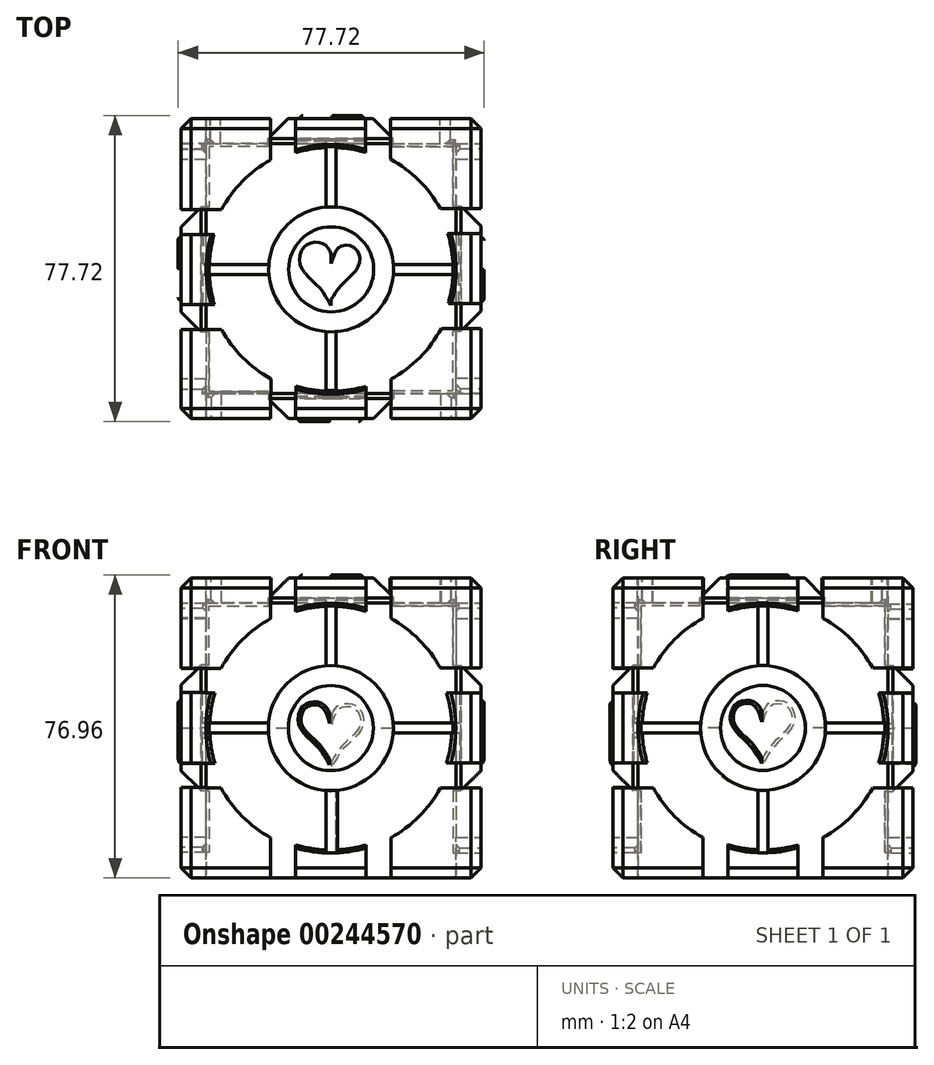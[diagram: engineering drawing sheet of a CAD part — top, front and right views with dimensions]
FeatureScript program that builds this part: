
annotation { "Feature Type Name" : "Feature", "Feature Type Description" : "" }
export const myFeature = defineFeature(function(context is Context, id is Id, definition is map)
    precondition{}
    {
        {
            var Q0;
            Q0=qCreatedBy(makeId("Front.planeOp"),FACE);
            var sketch = newSketch(context, id + "F0", { "sketchPlane" : qUnion([Q0])});
            skLineSegment(sketch, "E0.bottom", {"start": v(38.1, 38.1) * mm, "end": v(-38.1, 38.1) * mm});
            skLineSegment(sketch, "E0.top", {"start": v(38.1, -38.1) * mm, "end": v(-38.1, -38.1) * mm});
            skLineSegment(sketch, "E0.left", {"start": v(38.1, 38.1) * mm, "end": v(38.1, -38.1) * mm});
            skLineSegment(sketch, "E0.right", {"start": v(-38.1, 38.1) * mm, "end": v(-38.1, -38.1) * mm});
            skPoint(sketch, "E0.middle", {"position": v(0, 0) * mm});
            skSolve(sketch);
        }
        {
            var Q0;
            Q0=makeQuery(id+"F0.imprint","IMPRINT",FACE,{"disambiguationData":[TD([[makeQuery(id+"F0.imprint","IMPRINT",EDGE,{"derivedFrom":sQuery(id+"F0.wireOp",EDGE,"E0.bottom")}),1.0]])]});
            extrude(context, id + "F1", {"entities" : qUnion([Q0]), "depth" : 76.2 * mm});
        }
        {
            var Q0;
            Q0=makeQuery(id+"F1.opExtrude","SWEPT_FACE",FACE,{"disambiguationData":[OSD([sQuery(id+"F0.wireOp",EDGE,"E0.left")])]});
            var sketch = newSketch(context, id + "F2", { "sketchPlane" : qUnion([Q0])});
            skLineSegment(sketch, "E1.bottom", {"start": v(-76.2, 38.1) * mm, "end": v(-53.34, 38.1) * mm});
            skLineSegment(sketch, "E1.top", {"start": v(-76.2, 15.24) * mm, "end": v(-65.95, 15.24) * mm});
            skLineSegment(sketch, "E1.left", {"start": v(-76.2, 38.1) * mm, "end": v(-76.2, 15.24) * mm});
            skLineSegment(sketch, "E1.right", {"start": v(-53.34, 38.1) * mm, "end": v(-53.34, 27.85) * mm});
            skLineSegment(sketch, "E2.bottom", {"start": v(-76.2, 8.89) * mm, "end": v(-68.58, 8.89) * mm});
            skLineSegment(sketch, "E2.top", {"start": v(-76.2, -8.9) * mm, "end": v(-68.58, -8.9) * mm});
            skLineSegment(sketch, "E2.left", {"start": v(-76.2, 8.89) * mm, "end": v(-76.2, -8.9) * mm});
            skLineSegment(sketch, "E3.bottom", {"start": v(-76.2, -38.1) * mm, "end": v(-53.34, -38.1) * mm});
            skLineSegment(sketch, "E3.top", {"start": v(-76.2, -15.24) * mm, "end": v(-65.95, -15.24) * mm});
            skLineSegment(sketch, "E3.left", {"start": v(-76.2, -38.1) * mm, "end": v(-76.2, -15.24) * mm});
            skLineSegment(sketch, "E3.right", {"start": v(-53.34, -38.1) * mm, "end": v(-53.34, -27.85) * mm});
            skLineSegment(sketch, "E4.bottom", {"start": v(-47, 38.1) * mm, "end": v(-29.21, 38.1) * mm});
            skLineSegment(sketch, "E4.left", {"start": v(-47, 38.1) * mm, "end": v(-47, 30.48) * mm});
            skLineSegment(sketch, "E4.right", {"start": v(-29.21, 38.1) * mm, "end": v(-29.21, 30.48) * mm});
            skLineSegment(sketch, "E5.bottom", {"start": v(0, 38.1) * mm, "end": v(-22.86, 38.1) * mm});
            skLineSegment(sketch, "E5.top", {"start": v(0, 15.24) * mm, "end": v(-10.25, 15.24) * mm});
            skLineSegment(sketch, "E5.left", {"start": v(0, 38.1) * mm, "end": v(0, 15.24) * mm});
            skLineSegment(sketch, "E5.right", {"start": v(-22.86, 38.1) * mm, "end": v(-22.86, 27.85) * mm});
            skLineSegment(sketch, "E6.bottom", {"start": v(0, -38.1) * mm, "end": v(-22.86, -38.1) * mm});
            skLineSegment(sketch, "E6.top", {"start": v(0, -15.24) * mm, "end": v(-10.25, -15.24) * mm});
            skLineSegment(sketch, "E6.left", {"start": v(0, -38.1) * mm, "end": v(0, -15.24) * mm});
            skLineSegment(sketch, "E6.right", {"start": v(-22.86, -38.1) * mm, "end": v(-22.86, -27.85) * mm});
            skLineSegment(sketch, "E7.top", {"start": v(-47, -38.1) * mm, "end": v(-29.21, -38.1) * mm});
            skLineSegment(sketch, "E7.left", {"start": v(-47, -30.48) * mm, "end": v(-47, -38.1) * mm});
            skLineSegment(sketch, "E7.right", {"start": v(-29.21, -30.48) * mm, "end": v(-29.21, -38.1) * mm});
            skLineSegment(sketch, "E8.bottom", {"start": v(-7.62, 8.89) * mm, "end": v(0, 8.89) * mm});
            skLineSegment(sketch, "E8.top", {"start": v(-7.62, -8.9) * mm, "end": v(0, -8.9) * mm});
            skLineSegment(sketch, "E8.right", {"start": v(0, 8.89) * mm, "end": v(0, -8.9) * mm});
            skArc(sketch, "E9", {"start": v(-53.34, 27.85) * mm, "mid": v(-60.55, 22.45) * mm, "end": v(-65.95, 15.24) * mm});
            skCircle(sketch, "E10", {"center": v(-38.1, 0) * mm, "radius": 15.88 * mm});
            skLineSegment(sketch, "E11", {"start": v(-38.1, 15.88) * mm, "end": v(-38.1, -15.88) * mm, "construction": true});
            skArc(sketch, "E12.trimOffspring", {"start": v(-29.2, 30.48) * mm, "mid": v(-38.1, 31.75) * mm, "end": v(-47, 30.48) * mm});
            skArc(sketch, "E13.trimOffspring", {"start": v(-10.25, 15.24) * mm, "mid": v(-15.65, 22.45) * mm, "end": v(-22.86, 27.85) * mm});
            skArc(sketch, "E14.trimOffspring", {"start": v(-68.58, 8.89) * mm, "mid": v(-69.85, 0) * mm, "end": v(-68.58, -8.89) * mm});
            skArc(sketch, "E15.trimOffspring", {"start": v(-65.95, -15.24) * mm, "mid": v(-60.55, -22.45) * mm, "end": v(-53.34, -27.85) * mm});
            skArc(sketch, "E16.trimOffspring", {"start": v(-7.62, -8.9) * mm, "mid": v(-6.35, 0) * mm, "end": v(-7.62, 8.89) * mm});
            skArc(sketch, "E17.trimOffspring", {"start": v(-22.86, -27.85) * mm, "mid": v(-15.65, -22.45) * mm, "end": v(-10.25, -15.24) * mm});
            skArc(sketch, "E18.trimOffspring", {"start": v(-47, -30.48) * mm, "mid": v(-38.1, -31.75) * mm, "end": v(-29.21, -30.48) * mm});
            skSolve(sketch);
        }
        {
            var Q0;
            {var subQ20=sQuery(id+"F2.wireOp",EDGE,"E1.top");Q0=makeQuery(id+"F2.imprint","IMPRINT",FACE,{"disambiguationData":[TD([[makeQuery(id+"F2.imprint","IMPRINT",EDGE,{"derivedFrom":subQ20}),-1.0]])]});}
            extrude(context, id + "F3", {"entities" : qUnion([Q0]), "operationType" : NewBodyOperationType.REMOVE, "oppositeDirection" : true, "depth" : 6.35 * mm});
        }
        {
            var Q0;
            Q0=makeQuery(id+"F1.opExtrude","CAP_FACE",FACE,{"disambiguationData":[OSD([sQuery(id+"F0.wireOp",EDGE,"E0.bottom"),sQuery(id+"F0.wireOp",EDGE,"E0.top"),sQuery(id+"F0.wireOp",EDGE,"E0.left"),sQuery(id+"F0.wireOp",EDGE,"E0.right")])],"isStart":true});
            var sketch = newSketch(context, id + "F4", { "sketchPlane" : qUnion([Q0])});
            skLineSegment(sketch, "E19.bottom", {"start": v(-37.9, 38.1) * mm, "end": v(-15.05, 38.1) * mm});
            skLineSegment(sketch, "E19.left", {"start": v(-37.9, 38.1) * mm, "end": v(-37.9, 37.9) * mm});
            skLineSegment(sketch, "E19.right", {"start": v(-15.05, 38.1) * mm, "end": v(-15.05, 27.85) * mm});
            skLineSegment(sketch, "E20.left", {"start": v(-37.9, 8.89) * mm, "end": v(-37.9, 8.7) * mm});
            skLineSegment(sketch, "E21.bottom", {"start": v(-37.9, -38.1) * mm, "end": v(-15.05, -38.1) * mm});
            skLineSegment(sketch, "E21.left", {"start": v(-37.9, -15.43) * mm, "end": v(-37.9, -15.24) * mm});
            skLineSegment(sketch, "E21.right", {"start": v(-15.05, -38.1) * mm, "end": v(-15.05, -27.85) * mm});
            skLineSegment(sketch, "E22.bottom", {"start": v(-8.7, 38.1) * mm, "end": v(9.08, 38.1) * mm});
            skLineSegment(sketch, "E22.left", {"start": v(-8.7, 38.1) * mm, "end": v(-8.7, 30.48) * mm});
            skLineSegment(sketch, "E22.right", {"start": v(9.08, 38.1) * mm, "end": v(9.08, 30.48) * mm});
            skLineSegment(sketch, "E23.bottom", {"start": v(38.3, 38.1) * mm, "end": v(15.43, 38.1) * mm});
            skLineSegment(sketch, "E23.top", {"start": v(38.3, 15.24) * mm, "end": v(28.04, 15.24) * mm});
            skLineSegment(sketch, "E23.left", {"start": v(38.3, 38.1) * mm, "end": v(38.3, 15.24) * mm});
            skLineSegment(sketch, "E23.right", {"start": v(15.43, 38.1) * mm, "end": v(15.43, 27.85) * mm});
            skLineSegment(sketch, "E24.bottom", {"start": v(38.3, -38.1) * mm, "end": v(15.43, -38.1) * mm});
            skLineSegment(sketch, "E24.top", {"start": v(38.3, -15.24) * mm, "end": v(28.04, -15.24) * mm});
            skLineSegment(sketch, "E24.left", {"start": v(38.3, -38.1) * mm, "end": v(38.3, -15.24) * mm});
            skLineSegment(sketch, "E24.right", {"start": v(15.43, -38.1) * mm, "end": v(15.43, -27.85) * mm});
            skLineSegment(sketch, "E25.top", {"start": v(-8.7, -38.1) * mm, "end": v(9.08, -38.1) * mm});
            skLineSegment(sketch, "E25.left", {"start": v(-8.7, -30.48) * mm, "end": v(-8.7, -38.1) * mm});
            skLineSegment(sketch, "E25.right", {"start": v(9.08, -30.48) * mm, "end": v(9.08, -38.1) * mm});
            skLineSegment(sketch, "E26.bottom", {"start": v(30.67, 8.9) * mm, "end": v(38.3, 8.9) * mm});
            skLineSegment(sketch, "E26.top", {"start": v(30.67, -8.89) * mm, "end": v(38.3, -8.89) * mm});
            skLineSegment(sketch, "E26.right", {"start": v(38.3, 8.9) * mm, "end": v(38.3, -8.89) * mm});
            skArc(sketch, "E27", {"start": v(-15.05, 27.85) * mm, "mid": v(-22.26, 22.45) * mm, "end": v(-27.66, 15.24) * mm});
            skCircle(sketch, "E28", {"center": v(0.2, 0) * mm, "radius": 15.88 * mm});
            skLineSegment(sketch, "E29", {"start": v(0.2, 15.88) * mm, "end": v(0.2, -15.87) * mm, "construction": true});
            skArc(sketch, "E30.trimOffspring", {"start": v(9.08, 30.48) * mm, "mid": v(0.2, 31.75) * mm, "end": v(-8.7, 30.48) * mm});
            skArc(sketch, "E31.trimOffspring", {"start": v(28.04, 15.24) * mm, "mid": v(22.64, 22.45) * mm, "end": v(15.43, 27.85) * mm});
            skArc(sketch, "E32.trimOffspring", {"start": v(-30.29, 8.9) * mm, "mid": v(-31.56, 0) * mm, "end": v(-30.29, -8.89) * mm});
            skArc(sketch, "E33.trimOffspring", {"start": v(-27.66, -15.24) * mm, "mid": v(-22.26, -22.45) * mm, "end": v(-15.05, -27.85) * mm});
            skArc(sketch, "E34.trimOffspring", {"start": v(30.67, -8.89) * mm, "mid": v(31.94, 0) * mm, "end": v(30.67, 8.9) * mm});
            skArc(sketch, "E35.trimOffspring", {"start": v(15.43, -27.85) * mm, "mid": v(22.64, -22.45) * mm, "end": v(28.04, -15.24) * mm});
            skArc(sketch, "E36.trimOffspring", {"start": v(-8.7, -30.48) * mm, "mid": v(0.2, -31.75) * mm, "end": v(9.08, -30.48) * mm});
            skLineSegment(sketch, "E37.bottom", {"start": v(-37.9, 37.9) * mm, "end": v(-15.05, 37.9) * mm});
            skLineSegment(sketch, "E37.left", {"start": v(-37.9, 15.24) * mm, "end": v(-37.9, 15.05) * mm});
            skLineSegment(sketch, "E37.right", {"start": v(-15.05, 37.9) * mm, "end": v(-15.05, 27.66) * mm});
            skLineSegment(sketch, "E38.bottom", {"start": v(-30.34, 8.7) * mm, "end": v(-30.29, 8.7) * mm});
            skLineSegment(sketch, "E38.left", {"start": v(-37.9, -8.9) * mm, "end": v(-37.9, -9.08) * mm});
            skLineSegment(sketch, "E39.bottom", {"start": v(-37.9, -38.3) * mm, "end": v(-15.05, -38.3) * mm});
            skLineSegment(sketch, "E39.left", {"start": v(-37.9, -38.3) * mm, "end": v(-37.9, -38.1) * mm});
            skLineSegment(sketch, "E39.right", {"start": v(-15.05, -38.3) * mm, "end": v(-15.05, -28.04) * mm});
            skLineSegment(sketch, "E40.bottom", {"start": v(-8.7, 37.9) * mm, "end": v(9.08, 37.9) * mm});
            skLineSegment(sketch, "E40.left", {"start": v(-8.7, 37.9) * mm, "end": v(-8.7, 30.29) * mm});
            skLineSegment(sketch, "E40.right", {"start": v(9.08, 37.9) * mm, "end": v(9.08, 30.29) * mm});
            skLineSegment(sketch, "E41.bottom", {"start": v(38.3, 37.9) * mm, "end": v(15.43, 37.9) * mm});
            skLineSegment(sketch, "E41.top", {"start": v(38.3, 15.05) * mm, "end": v(28.04, 15.05) * mm});
            skLineSegment(sketch, "E41.left", {"start": v(38.3, 37.9) * mm, "end": v(38.3, 15.05) * mm});
            skLineSegment(sketch, "E41.right", {"start": v(15.43, 37.9) * mm, "end": v(15.43, 27.66) * mm});
            skLineSegment(sketch, "E42.bottom", {"start": v(38.3, -38.3) * mm, "end": v(15.43, -38.3) * mm});
            skLineSegment(sketch, "E42.top", {"start": v(38.3, -15.43) * mm, "end": v(28.04, -15.43) * mm});
            skLineSegment(sketch, "E42.left", {"start": v(38.3, -38.3) * mm, "end": v(38.3, -15.43) * mm});
            skLineSegment(sketch, "E42.right", {"start": v(15.43, -38.3) * mm, "end": v(15.43, -28.04) * mm});
            skLineSegment(sketch, "E43.top", {"start": v(-8.7, -38.3) * mm, "end": v(9.08, -38.3) * mm});
            skLineSegment(sketch, "E43.left", {"start": v(-8.7, -30.67) * mm, "end": v(-8.7, -38.3) * mm});
            skLineSegment(sketch, "E43.right", {"start": v(9.08, -30.67) * mm, "end": v(9.08, -38.3) * mm});
            skLineSegment(sketch, "E44.bottom", {"start": v(30.67, 8.7) * mm, "end": v(38.3, 8.7) * mm});
            skLineSegment(sketch, "E44.top", {"start": v(30.67, -9.08) * mm, "end": v(38.3, -9.08) * mm});
            skLineSegment(sketch, "E44.right", {"start": v(38.3, 8.7) * mm, "end": v(38.3, -9.08) * mm});
            skArc(sketch, "E45", {"start": v(-15.05, 27.66) * mm, "mid": v(-22.26, 22.26) * mm, "end": v(-27.66, 15.05) * mm});
            skCircle(sketch, "E46", {"center": v(0.2, -0.2) * mm, "radius": 15.88 * mm});
            skLineSegment(sketch, "E47", {"start": v(0.2, 15.68) * mm, "end": v(0.2, -16.07) * mm, "construction": true});
            skArc(sketch, "E48.trimOffspring", {"start": v(9.08, 30.29) * mm, "mid": v(0.2, 31.56) * mm, "end": v(-8.7, 30.29) * mm});
            skArc(sketch, "E49.trimOffspring", {"start": v(28.04, 15.05) * mm, "mid": v(22.64, 22.26) * mm, "end": v(15.43, 27.66) * mm});
            skArc(sketch, "E50.trimOffspring", {"start": v(-30.29, 8.7) * mm, "mid": v(-31.56, -0.2) * mm, "end": v(-30.29, -9.08) * mm});
            skArc(sketch, "E51.trimOffspring", {"start": v(-27.66, -15.43) * mm, "mid": v(-22.26, -22.64) * mm, "end": v(-15.05, -28.04) * mm});
            skArc(sketch, "E52.trimOffspring", {"start": v(30.67, -9.08) * mm, "mid": v(31.94, -0.2) * mm, "end": v(30.67, 8.7) * mm});
            skArc(sketch, "E53.trimOffspring", {"start": v(15.43, -28.04) * mm, "mid": v(22.64, -22.64) * mm, "end": v(28.04, -15.43) * mm});
            skArc(sketch, "E54.trimOffspring", {"start": v(-8.7, -30.67) * mm, "mid": v(0.2, -31.94) * mm, "end": v(9.08, -30.67) * mm});
            skPoint(sketch, "E19.top.start.orphan", {"position": v(-37.9, 15.24) * mm});
            skPoint(sketch, "E55.orphan", {"position": v(-37.9, -8.9) * mm});
            skLineSegment(sketch, "E56", {"start": v(-31.75, 8.9) * mm, "end": v(-30.29, 8.9) * mm});
            skLineSegment(sketch, "E57", {"start": v(-31.75, 15.24) * mm, "end": v(-27.66, 15.24) * mm});
            skLineSegment(sketch, "E58", {"start": v(-31.75, 8.9) * mm, "end": v(-31.75, 15.24) * mm});
            skLineSegment(sketch, "E59", {"start": v(-30.29, -8.89) * mm, "end": v(-31.75, -8.89) * mm});
            skLineSegment(sketch, "E60", {"start": v(-31.75, -8.89) * mm, "end": v(-31.75, -15.24) * mm});
            skLineSegment(sketch, "E61", {"start": v(-31.75, -15.24) * mm, "end": v(-27.66, -15.24) * mm});
            skSolve(sketch);
        }
        {
            var Q0;
            {var subQ58=sQuery(id+"F4.wireOp",EDGE,"E19.right");Q0=makeQuery(id+"F4.imprint","IMPRINT",FACE,{"disambiguationData":[TD([[makeQuery(id+"F4.imprint","IMPRINT",EDGE,{"derivedFrom":subQ58}),1.0]])]});}
            extrude(context, id + "F5", {"entities" : qUnion([Q0]), "operationType" : NewBodyOperationType.REMOVE, "oppositeDirection" : true, "depth" : 6.35 * mm});
        }
        {
            var Q0;
            Q0=makeQuery(id+"F1.opExtrude","SWEPT_FACE",FACE,{"disambiguationData":[OSD([sQuery(id+"F0.wireOp",EDGE,"E0.right")])]});
            var sketch = newSketch(context, id + "F6", { "sketchPlane" : qUnion([Q0])});
            skLineSegment(sketch, "E62", {"start": v(0, 0) * mm, "end": v(38.1, 0) * mm, "construction": true});
            skPoint(sketch, "E62.endSnap0", {"position": v(38.1, 38.1) * mm});
            skLineSegment(sketch, "E63.bottom", {"start": v(0.2, 38.18) * mm, "end": v(23.07, 38.18) * mm});
            skLineSegment(sketch, "E63.left", {"start": v(0.2, 38.18) * mm, "end": v(0.2, 37.99) * mm});
            skLineSegment(sketch, "E63.right", {"start": v(23.07, 38.18) * mm, "end": v(23.07, 27.93) * mm});
            skLineSegment(sketch, "E64.left", {"start": v(0.2, 8.97) * mm, "end": v(0.2, 8.78) * mm});
            skLineSegment(sketch, "E65.bottom", {"start": v(0.2, -38.02) * mm, "end": v(23.07, -38.02) * mm});
            skLineSegment(sketch, "E65.left", {"start": v(0.2, -15.35) * mm, "end": v(0.2, -15.16) * mm});
            skLineSegment(sketch, "E65.right", {"start": v(23.07, -38.02) * mm, "end": v(23.07, -27.77) * mm});
            skLineSegment(sketch, "E66.bottom", {"start": v(29.42, 38.18) * mm, "end": v(47.2, 38.18) * mm});
            skLineSegment(sketch, "E66.left", {"start": v(29.42, 38.18) * mm, "end": v(29.42, 30.56) * mm});
            skLineSegment(sketch, "E66.right", {"start": v(47.2, 38.18) * mm, "end": v(47.2, 30.56) * mm});
            skLineSegment(sketch, "E67.bottom", {"start": v(76.4, 38.18) * mm, "end": v(53.55, 38.18) * mm});
            skLineSegment(sketch, "E67.top", {"start": v(76.4, 15.32) * mm, "end": v(66.16, 15.32) * mm});
            skLineSegment(sketch, "E67.left", {"start": v(76.4, 38.18) * mm, "end": v(76.4, 15.32) * mm});
            skLineSegment(sketch, "E67.right", {"start": v(53.55, 38.18) * mm, "end": v(53.55, 27.93) * mm});
            skLineSegment(sketch, "E68.bottom", {"start": v(76.4, -38.02) * mm, "end": v(53.55, -38.02) * mm});
            skLineSegment(sketch, "E68.top", {"start": v(76.4, -15.16) * mm, "end": v(66.16, -15.16) * mm});
            skLineSegment(sketch, "E68.left", {"start": v(76.4, -38.02) * mm, "end": v(76.4, -15.16) * mm});
            skLineSegment(sketch, "E68.right", {"start": v(53.55, -38.02) * mm, "end": v(53.55, -27.77) * mm});
            skLineSegment(sketch, "E69.top", {"start": v(29.42, -38.02) * mm, "end": v(47.2, -38.02) * mm});
            skLineSegment(sketch, "E69.left", {"start": v(29.42, -30.4) * mm, "end": v(29.42, -38.02) * mm});
            skLineSegment(sketch, "E69.right", {"start": v(47.2, -30.4) * mm, "end": v(47.2, -38.02) * mm});
            skLineSegment(sketch, "E70.bottom", {"start": v(68.79, 8.97) * mm, "end": v(76.4, 8.97) * mm});
            skLineSegment(sketch, "E70.top", {"start": v(68.79, -8.81) * mm, "end": v(76.4, -8.81) * mm});
            skLineSegment(sketch, "E70.right", {"start": v(76.4, 8.97) * mm, "end": v(76.4, -8.81) * mm});
            skArc(sketch, "E71", {"start": v(23.07, 27.93) * mm, "mid": v(15.86, 22.53) * mm, "end": v(10.45, 15.32) * mm});
            skCircle(sketch, "E72", {"center": v(38.3, 0.08) * mm, "radius": 15.88 * mm});
            skLineSegment(sketch, "E73", {"start": v(38.3, 15.95) * mm, "end": v(38.3, -15.8) * mm, "construction": true});
            skArc(sketch, "E74.trimOffspring", {"start": v(47.2, 30.56) * mm, "mid": v(38.3, 31.83) * mm, "end": v(29.42, 30.56) * mm});
            skArc(sketch, "E75.trimOffspring", {"start": v(66.16, 15.32) * mm, "mid": v(60.76, 22.53) * mm, "end": v(53.55, 27.93) * mm});
            skArc(sketch, "E76.trimOffspring", {"start": v(7.83, 8.97) * mm, "mid": v(6.56, 0.08) * mm, "end": v(7.83, -8.81) * mm});
            skArc(sketch, "E77.trimOffspring", {"start": v(10.45, -15.16) * mm, "mid": v(15.86, -22.37) * mm, "end": v(23.07, -27.77) * mm});
            skArc(sketch, "E78.trimOffspring", {"start": v(68.79, -8.81) * mm, "mid": v(70.06, 0.08) * mm, "end": v(68.79, 8.97) * mm});
            skArc(sketch, "E79.trimOffspring", {"start": v(53.55, -27.77) * mm, "mid": v(60.76, -22.37) * mm, "end": v(66.16, -15.16) * mm});
            skArc(sketch, "E80.trimOffspring", {"start": v(29.42, -30.4) * mm, "mid": v(38.3, -31.67) * mm, "end": v(47.2, -30.4) * mm});
            skLineSegment(sketch, "E81.bottom", {"start": v(0.2, 37.99) * mm, "end": v(23.07, 37.99) * mm});
            skLineSegment(sketch, "E81.left", {"start": v(0.2, 15.32) * mm, "end": v(0.2, 15.13) * mm});
            skLineSegment(sketch, "E81.right", {"start": v(23.07, 37.99) * mm, "end": v(23.07, 27.74) * mm});
            skLineSegment(sketch, "E82.bottom", {"start": v(7.77, 8.78) * mm, "end": v(7.83, 8.78) * mm});
            skLineSegment(sketch, "E82.left", {"start": v(0.2, -8.81) * mm, "end": v(0.2, -9) * mm});
            skLineSegment(sketch, "E83.bottom", {"start": v(0.2, -38.21) * mm, "end": v(23.07, -38.21) * mm});
            skLineSegment(sketch, "E83.left", {"start": v(0.2, -38.21) * mm, "end": v(0.2, -38.02) * mm});
            skLineSegment(sketch, "E83.right", {"start": v(23.07, -38.21) * mm, "end": v(23.07, -27.96) * mm});
            skLineSegment(sketch, "E84.bottom", {"start": v(29.42, 37.99) * mm, "end": v(47.2, 37.99) * mm});
            skLineSegment(sketch, "E84.left", {"start": v(29.42, 37.99) * mm, "end": v(29.42, 30.37) * mm});
            skLineSegment(sketch, "E84.right", {"start": v(47.2, 37.99) * mm, "end": v(47.2, 30.37) * mm});
            skLineSegment(sketch, "E85.bottom", {"start": v(76.4, 37.99) * mm, "end": v(53.55, 37.99) * mm});
            skLineSegment(sketch, "E85.top", {"start": v(76.4, 15.13) * mm, "end": v(66.16, 15.13) * mm});
            skLineSegment(sketch, "E85.left", {"start": v(76.4, 37.99) * mm, "end": v(76.4, 15.13) * mm});
            skLineSegment(sketch, "E85.right", {"start": v(53.55, 37.99) * mm, "end": v(53.55, 27.74) * mm});
            skLineSegment(sketch, "E86.bottom", {"start": v(76.4, -38.21) * mm, "end": v(53.55, -38.21) * mm});
            skLineSegment(sketch, "E86.top", {"start": v(76.4, -15.35) * mm, "end": v(66.16, -15.35) * mm});
            skLineSegment(sketch, "E86.left", {"start": v(76.4, -38.21) * mm, "end": v(76.4, -15.35) * mm});
            skLineSegment(sketch, "E86.right", {"start": v(53.55, -38.21) * mm, "end": v(53.55, -27.96) * mm});
            skLineSegment(sketch, "E87.top", {"start": v(29.42, -38.21) * mm, "end": v(47.2, -38.21) * mm});
            skLineSegment(sketch, "E87.left", {"start": v(29.42, -30.6) * mm, "end": v(29.42, -38.21) * mm});
            skLineSegment(sketch, "E87.right", {"start": v(47.2, -30.6) * mm, "end": v(47.2, -38.21) * mm});
            skLineSegment(sketch, "E88.bottom", {"start": v(68.79, 8.78) * mm, "end": v(76.4, 8.78) * mm});
            skLineSegment(sketch, "E88.top", {"start": v(68.79, -9) * mm, "end": v(76.4, -9) * mm});
            skLineSegment(sketch, "E88.right", {"start": v(76.4, 8.78) * mm, "end": v(76.4, -9) * mm});
            skArc(sketch, "E89", {"start": v(23.07, 27.74) * mm, "mid": v(15.86, 22.34) * mm, "end": v(10.45, 15.13) * mm});
            skCircle(sketch, "E90", {"center": v(38.3, -0.11) * mm, "radius": 15.88 * mm});
            skLineSegment(sketch, "E91", {"start": v(38.3, 15.76) * mm, "end": v(38.3, -15.99) * mm, "construction": true});
            skArc(sketch, "E92.trimOffspring", {"start": v(47.2, 30.37) * mm, "mid": v(38.3, 31.64) * mm, "end": v(29.42, 30.37) * mm});
            skArc(sketch, "E93.trimOffspring", {"start": v(66.16, 15.13) * mm, "mid": v(60.76, 22.34) * mm, "end": v(53.55, 27.74) * mm});
            skArc(sketch, "E94.trimOffspring", {"start": v(7.83, 8.78) * mm, "mid": v(6.56, -0.11) * mm, "end": v(7.83, -9) * mm});
            skArc(sketch, "E95.trimOffspring", {"start": v(10.45, -15.35) * mm, "mid": v(15.86, -22.56) * mm, "end": v(23.07, -27.96) * mm});
            skArc(sketch, "E96.trimOffspring", {"start": v(68.79, -9) * mm, "mid": v(70.06, -0.11) * mm, "end": v(68.79, 8.78) * mm});
            skArc(sketch, "E97.trimOffspring", {"start": v(53.55, -27.96) * mm, "mid": v(60.76, -22.56) * mm, "end": v(66.16, -15.35) * mm});
            skArc(sketch, "E98.trimOffspring", {"start": v(29.42, -30.6) * mm, "mid": v(38.3, -31.86) * mm, "end": v(47.2, -30.6) * mm});
            skPoint(sketch, "E63.top.start.orphan", {"position": v(0.2, 15.32) * mm});
            skPoint(sketch, "E99.orphan", {"position": v(0.2, -8.81) * mm});
            skLineSegment(sketch, "E100", {"start": v(6.37, 8.97) * mm, "end": v(7.83, 8.97) * mm});
            skLineSegment(sketch, "E101", {"start": v(6.37, 15.32) * mm, "end": v(10.45, 15.32) * mm});
            skLineSegment(sketch, "E102", {"start": v(6.37, 8.97) * mm, "end": v(6.37, 15.32) * mm});
            skLineSegment(sketch, "E103", {"start": v(7.83, -8.81) * mm, "end": v(6.37, -8.81) * mm});
            skLineSegment(sketch, "E104", {"start": v(6.37, -8.81) * mm, "end": v(6.37, -15.16) * mm});
            skLineSegment(sketch, "E105", {"start": v(6.37, -15.16) * mm, "end": v(10.45, -15.16) * mm});
            skSolve(sketch);
        }
        {
            var Q0;
            {var subQ55=sQuery(id+"F6.wireOp",EDGE,"E65.right");Q0=makeQuery(id+"F6.imprint","IMPRINT",FACE,{"disambiguationData":[TD([[makeQuery(id+"F6.imprint","IMPRINT",EDGE,{"derivedFrom":subQ55}),-1.0]])]});}
            extrude(context, id + "F7", {"entities" : qUnion([Q0]), "operationType" : NewBodyOperationType.REMOVE, "oppositeDirection" : true, "depth" : 6.35 * mm});
        }
        {
            var Q0;
            Q0=makeQuery(id+"F1.opExtrude","CAP_FACE",FACE,{"disambiguationData":[OSD([sQuery(id+"F0.wireOp",EDGE,"E0.bottom"),sQuery(id+"F0.wireOp",EDGE,"E0.top"),sQuery(id+"F0.wireOp",EDGE,"E0.left"),sQuery(id+"F0.wireOp",EDGE,"E0.right")])],"isStart":false});
            var sketch = newSketch(context, id + "F8", { "sketchPlane" : qUnion([Q0])});
            skArc(sketch, "E106", {"start": v(-15.33, 27.8) * mm, "mid": v(-22.59, 22.36) * mm, "end": v(-28, 15.08) * mm});
            skCircle(sketch, "E107", {"center": v(-0.1, -0.05) * mm, "radius": 15.87 * mm});
            skLineSegment(sketch, "E108", {"start": v(-38.2, 38.05) * mm, "end": v(-15.33, 38.05) * mm});
            skLineSegment(sketch, "E109", {"start": v(38, 38.05) * mm, "end": v(15.15, 38.05) * mm});
            skLineSegment(sketch, "E110", {"start": v(-15.33, 38.05) * mm, "end": v(-15.33, 27.8) * mm});
            skLineSegment(sketch, "E111", {"start": v(15.15, 38.05) * mm, "end": v(15.15, 27.8) * mm});
            skLineSegment(sketch, "E112", {"start": v(-15.33, -27.9) * mm, "end": v(-15.33, -38.15) * mm});
            skLineSegment(sketch, "E113", {"start": v(-15.33, -38.15) * mm, "end": v(-38.2, -38.15) * mm});
            skLineSegment(sketch, "E114", {"start": v(15.15, -27.9) * mm, "end": v(15.15, -38.15) * mm});
            skLineSegment(sketch, "E115", {"start": v(15.15, -38.15) * mm, "end": v(38, -38.15) * mm});
            skLineSegment(sketch, "E116", {"start": v(-15.33, -38.15) * mm, "end": v(-8.98, -38.15) * mm});
            skLineSegment(sketch, "E117", {"start": v(-8.98, -38.15) * mm, "end": v(-8.98, -30.53) * mm});
            skLineSegment(sketch, "E118", {"start": v(-15.33, 38.05) * mm, "end": v(-8.98, 38.05) * mm});
            skLineSegment(sketch, "E119", {"start": v(-8.98, 38.05) * mm, "end": v(-8.98, 30.43) * mm});
            skLineSegment(sketch, "E120", {"start": v(15.15, 38.05) * mm, "end": v(8.8, 38.05) * mm});
            skLineSegment(sketch, "E121", {"start": v(8.8, 38.05) * mm, "end": v(8.8, 30.43) * mm});
            skLineSegment(sketch, "E122", {"start": v(15.15, -38.15) * mm, "end": v(8.8, -38.15) * mm});
            skLineSegment(sketch, "E123", {"start": v(8.8, -38.15) * mm, "end": v(8.8, -30.53) * mm});
            skLineSegment(sketch, "E124", {"start": v(-31.84, 15.08) * mm, "end": v(-28, 15.08) * mm});
            skLineSegment(sketch, "E125", {"start": v(-31.84, 8.92) * mm, "end": v(-31.84, 15.08) * mm});
            skLineSegment(sketch, "E126", {"start": v(-31.84, 8.92) * mm, "end": v(-30.55, 8.92) * mm});
            skLineSegment(sketch, "E127", {"start": v(-28, -15.2) * mm, "end": v(-31.84, -15.2) * mm});
            skLineSegment(sketch, "E128", {"start": v(-31.84, -15.2) * mm, "end": v(-31.84, -9.05) * mm});
            skLineSegment(sketch, "E129", {"start": v(-31.84, -9.05) * mm, "end": v(-30.54, -9.05) * mm});
            skLineSegment(sketch, "E130", {"start": v(27.76, 15.2) * mm, "end": v(31.66, 15.2) * mm});
            skLineSegment(sketch, "E131", {"start": v(31.66, 15.2) * mm, "end": v(31.66, 8.84) * mm});
            skLineSegment(sketch, "E132", {"start": v(31.66, 8.84) * mm, "end": v(30.39, 8.84) * mm});
            skLineSegment(sketch, "E133", {"start": v(27.76, -15.29) * mm, "end": v(31.66, -15.29) * mm});
            skLineSegment(sketch, "E134", {"start": v(31.66, -15.29) * mm, "end": v(31.66, -8.94) * mm});
            skLineSegment(sketch, "E135", {"start": v(31.66, -8.94) * mm, "end": v(30.39, -8.94) * mm});
            skArc(sketch, "E136.trimOffspring", {"start": v(8.8, 30.43) * mm, "mid": v(-0.1, 31.7) * mm, "end": v(-8.98, 30.43) * mm});
            skArc(sketch, "E137.trimOffspring", {"start": v(-30.55, 8.92) * mm, "mid": v(-31.84, -0.06) * mm, "end": v(-30.54, -9.05) * mm});
            skArc(sketch, "E138.trimOffspring", {"start": v(-28, -15.2) * mm, "mid": v(-22.58, -22.46) * mm, "end": v(-15.33, -27.9) * mm});
            skArc(sketch, "E139.trimOffspring", {"start": v(27.76, 15.2) * mm, "mid": v(22.36, 22.4) * mm, "end": v(15.15, 27.8) * mm});
            skArc(sketch, "E140.trimOffspring", {"start": v(-8.98, -30.53) * mm, "mid": v(-0.1, -31.8) * mm, "end": v(8.8, -30.53) * mm});
            skArc(sketch, "E141.trimOffspring", {"start": v(15.15, -27.9) * mm, "mid": v(22.36, -22.5) * mm, "end": v(27.76, -15.29) * mm});
            skArc(sketch, "E142.trimOffspring", {"start": v(30.39, -8.94) * mm, "mid": v(31.66, -0.05) * mm, "end": v(30.39, 8.84) * mm});
            skSolve(sketch);
        }
        {
            var Q0;
            {var subQ25=sQuery(id+"F8.wireOp",EDGE,"E106");Q0=makeQuery(id+"F8.imprint","IMPRINT",FACE,{"disambiguationData":[TD([[makeQuery(id+"F8.imprint","IMPRINT",EDGE,{"derivedFrom":subQ25}),1.0]])]});}
            extrude(context, id + "F9", {"entities" : qUnion([Q0]), "operationType" : NewBodyOperationType.REMOVE, "oppositeDirection" : true, "depth" : 6.35 * mm});
        }
        {
            var Q0;
            Q0=makeQuery(id+"F9.boolean.opBoolean","COPY",FACE,{"derivedFrom":makeQuery(id+"F9.opExtrude","SWEPT_FACE",FACE,{"disambiguationData":[OSD([sQuery(id+"F8.wireOp",EDGE,"E131")])]})});
            var sketch = newSketch(context, id + "F10", { "sketchPlane" : qUnion([Q0])});
            skLineSegment(sketch, "E143", {"start": v(69.85, 15.2) * mm, "end": v(76.2, 15.2) * mm});
            skLineSegment(sketch, "E144", {"start": v(76.2, 15.2) * mm, "end": v(76.2, 8.84) * mm});
            skLineSegment(sketch, "E145", {"start": v(76.2, 8.84) * mm, "end": v(69.85, 8.84) * mm});
            skLineSegment(sketch, "E146", {"start": v(69.85, 8.84) * mm, "end": v(69.85, 15.2) * mm});
            skSolve(sketch);
        }
        {
            var Q0;
            Q0=makeQuery(id+"F10.imprint","IMPRINT",FACE,{"disambiguationData":[TD([[makeQuery(id+"F10.imprint","IMPRINT",EDGE,{"derivedFrom":sQuery(id+"F10.wireOp",EDGE,"E143")}),-1.0]])]});
            var Q1;
            Q1 = qSketchRegion(id + "F10", true);
            extrude(context, id + "F11", {"entities" : qUnion([Q0, Q1]), "operationType" : NewBodyOperationType.REMOVE, "oppositeDirection" : true, "depth" : 25.4 * mm});
        }
        {
            var Q0;
            Q0=makeQuery(id+"F9.boolean.opBoolean","COPY",FACE,{"derivedFrom":makeQuery(id+"F9.opExtrude","SWEPT_FACE",FACE,{"disambiguationData":[OSD([sQuery(id+"F8.wireOp",EDGE,"E134")])]})});
            var sketch = newSketch(context, id + "F12", { "sketchPlane" : qUnion([Q0])});
            skLineSegment(sketch, "E147", {"start": v(69.85, -8.94) * mm, "end": v(76.2, -8.94) * mm});
            skLineSegment(sketch, "E148", {"start": v(76.2, -8.94) * mm, "end": v(76.2, -15.29) * mm});
            skLineSegment(sketch, "E149", {"start": v(76.2, -15.29) * mm, "end": v(69.85, -15.29) * mm});
            skLineSegment(sketch, "E150", {"start": v(69.85, -15.29) * mm, "end": v(69.85, -8.94) * mm});
            skSolve(sketch);
        }
        {
            var Q0;
            Q0=makeQuery(id+"F12.imprint","IMPRINT",FACE,{"disambiguationData":[TD([[makeQuery(id+"F12.imprint","IMPRINT",EDGE,{"derivedFrom":sQuery(id+"F12.wireOp",EDGE,"E147")}),-1.0]])]});
            extrude(context, id + "F13", {"entities" : qUnion([Q0]), "operationType" : NewBodyOperationType.REMOVE, "oppositeDirection" : true, "depth" : 25.4 * mm});
        }
        {
            var Q0;
            Q0=makeQuery(id+"F7.boolean.opBoolean","COPY",FACE,{"derivedFrom":makeQuery(id+"F7.opExtrude","SWEPT_FACE",FACE,{"disambiguationData":[OSD([sQuery(id+"F6.wireOp",EDGE,"E102")])]})});
            var sketch = newSketch(context, id + "F14", { "sketchPlane" : qUnion([Q0])});
            skLineSegment(sketch, "E151", {"start": v(-31.75, 15.32) * mm, "end": v(-38.1, 15.32) * mm});
            skLineSegment(sketch, "E152", {"start": v(-38.1, 15.32) * mm, "end": v(-38.1, 8.97) * mm});
            skLineSegment(sketch, "E153", {"start": v(-38.1, 8.97) * mm, "end": v(-31.75, 8.97) * mm});
            skLineSegment(sketch, "E154", {"start": v(-31.75, 8.97) * mm, "end": v(-31.75, 15.32) * mm});
            skSolve(sketch);
        }
        {
            var Q0;
            Q0=makeQuery(id+"F14.imprint","IMPRINT",FACE,{"disambiguationData":[TD([[makeQuery(id+"F14.imprint","IMPRINT",EDGE,{"derivedFrom":sQuery(id+"F14.wireOp",EDGE,"E151")}),1.0]])]});
            extrude(context, id + "F15", {"entities" : qUnion([Q0]), "operationType" : NewBodyOperationType.REMOVE, "oppositeDirection" : true, "depth" : 25.4 * mm});
        }
        {
            var Q0;
            Q0=makeQuery(id+"F7.boolean.opBoolean","COPY",FACE,{"derivedFrom":makeQuery(id+"F7.opExtrude","SWEPT_FACE",FACE,{"disambiguationData":[OSD([sQuery(id+"F6.wireOp",EDGE,"E104")])]})});
            var sketch = newSketch(context, id + "F16", { "sketchPlane" : qUnion([Q0])});
            skLineSegment(sketch, "E155", {"start": v(-38.1, -8.81) * mm, "end": v(-38.1, -15.16) * mm});
            skLineSegment(sketch, "E156", {"start": v(-38.1, -15.16) * mm, "end": v(-31.75, -15.16) * mm});
            skLineSegment(sketch, "E157", {"start": v(-31.75, -15.16) * mm, "end": v(-31.75, -8.81) * mm});
            skLineSegment(sketch, "E158", {"start": v(-31.75, -8.81) * mm, "end": v(-38.1, -8.81) * mm});
            skSolve(sketch);
        }
        {
            var Q0;
            Q0=makeQuery(id+"F16.imprint","IMPRINT",FACE,{"disambiguationData":[TD([[makeQuery(id+"F16.imprint","IMPRINT",EDGE,{"derivedFrom":sQuery(id+"F16.wireOp",EDGE,"E155")}),1.0]])]});
            extrude(context, id + "F17", {"entities" : qUnion([Q0]), "operationType" : NewBodyOperationType.REMOVE, "oppositeDirection" : true, "depth" : 25.4 * mm});
        }
        {
            var Q0;
            Q0=makeQuery(id+"F9.boolean.opBoolean","COPY",FACE,{"derivedFrom":makeQuery(id+"F9.opExtrude","SWEPT_FACE",FACE,{"disambiguationData":[OSD([sQuery(id+"F8.wireOp",EDGE,"E118")])]})});
            var sketch = newSketch(context, id + "F18", { "sketchPlane" : qUnion([Q0])});
            skLineSegment(sketch, "E159", {"start": v(-15.33, 76.2) * mm, "end": v(-15.33, 69.85) * mm});
            skLineSegment(sketch, "E160", {"start": v(-15.33, 69.85) * mm, "end": v(-8.98, 69.85) * mm});
            skLineSegment(sketch, "E161", {"start": v(-8.98, 69.85) * mm, "end": v(-8.98, 76.2) * mm});
            skLineSegment(sketch, "E162", {"start": v(-8.98, 76.2) * mm, "end": v(-15.33, 76.2) * mm});
            skSolve(sketch);
        }
        {
            var Q0;
            Q0=makeQuery(id+"F18.imprint","IMPRINT",FACE,{"disambiguationData":[TD([[makeQuery(id+"F18.imprint","IMPRINT",EDGE,{"derivedFrom":sQuery(id+"F18.wireOp",EDGE,"E159")}),-1.0]])]});
            extrude(context, id + "F19", {"entities" : qUnion([Q0]), "operationType" : NewBodyOperationType.REMOVE, "oppositeDirection" : true, "depth" : 25.4 * mm});
        }
        {
            var Q0;
            Q0=makeQuery(id+"F9.boolean.opBoolean","COPY",FACE,{"derivedFrom":makeQuery(id+"F9.opExtrude","SWEPT_FACE",FACE,{"disambiguationData":[OSD([sQuery(id+"F8.wireOp",EDGE,"E120")])]})});
            var sketch = newSketch(context, id + "F20", { "sketchPlane" : qUnion([Q0])});
            skLineSegment(sketch, "E163", {"start": v(8.8, 76.2) * mm, "end": v(8.8, 69.85) * mm});
            skLineSegment(sketch, "E164", {"start": v(8.8, 69.85) * mm, "end": v(15.15, 69.85) * mm});
            skLineSegment(sketch, "E165", {"start": v(15.15, 69.85) * mm, "end": v(15.15, 76.2) * mm});
            skLineSegment(sketch, "E166", {"start": v(15.15, 76.2) * mm, "end": v(8.8, 76.2) * mm});
            skSolve(sketch);
        }
        {
            var Q0;
            Q0=makeQuery(id+"F20.imprint","IMPRINT",FACE,{"disambiguationData":[TD([[makeQuery(id+"F20.imprint","IMPRINT",EDGE,{"derivedFrom":sQuery(id+"F20.wireOp",EDGE,"E163")}),-1.0]])]});
            extrude(context, id + "F21", {"entities" : qUnion([Q0]), "operationType" : NewBodyOperationType.REMOVE, "oppositeDirection" : true, "depth" : 25.4 * mm});
        }
        {
            var Q0;
            Q0=makeQuery(id+"F1.opExtrude","SWEPT_FACE",FACE,{"disambiguationData":[OSD([sQuery(id+"F0.wireOp",EDGE,"E0.bottom")])]});
            var sketch = newSketch(context, id + "F22", { "sketchPlane" : qUnion([Q0])});
            skLineSegment(sketch, "E167", {"start": v(0, -38.3) * mm, "end": v(0, 0) * mm, "construction": true});
            skPoint(sketch, "E167.startSnap0", {"position": v(-38.1, -38.3) * mm});
            skCircle(sketch, "E168", {"center": v(0.02, -38.25) * mm, "radius": 15.88 * mm});
            skPoint(sketch, "E168.centerSnap0", {"position": v(-38.08, -38.25) * mm});
            skArc(sketch, "E169", {"start": v(-15.32, -10.45) * mm, "mid": v(-22.47, -15.83) * mm, "end": v(-27.84, -23) * mm});
            skLineSegment(sketch, "E170", {"start": v(-15.32, -10.45) * mm, "end": v(-15.32, -6.7) * mm});
            skLineSegment(sketch, "E171", {"start": v(-15.32, -6.7) * mm, "end": v(-8.97, -6.7) * mm});
            skLineSegment(sketch, "E172", {"start": v(-8.97, -6.7) * mm, "end": v(-8.97, -7.8) * mm});
            skLineSegment(sketch, "E173", {"start": v(15.16, -10.34) * mm, "end": v(15.16, -6.7) * mm});
            skLineSegment(sketch, "E174", {"start": v(15.16, -6.7) * mm, "end": v(8.81, -6.7) * mm});
            skLineSegment(sketch, "E175", {"start": v(8.81, -6.7) * mm, "end": v(8.81, -7.74) * mm});
            skLineSegment(sketch, "E176", {"start": v(-30.46, -29.36) * mm, "end": v(-31.73, -29.36) * mm});
            skLineSegment(sketch, "E177", {"start": v(-31.73, -29.36) * mm, "end": v(-31.73, -23) * mm});
            skLineSegment(sketch, "E178", {"start": v(-31.73, -23) * mm, "end": v(-27.84, -23) * mm});
            skLineSegment(sketch, "E179", {"start": v(-30.46, -47.14) * mm, "end": v(-31.73, -47.14) * mm});
            skLineSegment(sketch, "E180", {"start": v(-31.73, -47.14) * mm, "end": v(-31.73, -53.49) * mm});
            skLineSegment(sketch, "E181", {"start": v(-31.73, -53.49) * mm, "end": v(-27.84, -53.49) * mm});
            skLineSegment(sketch, "E182", {"start": v(-15.41, -66) * mm, "end": v(-15.41, -70.2) * mm});
            skLineSegment(sketch, "E183", {"start": v(-15.41, -70.2) * mm, "end": v(-9.06, -70.2) * mm});
            skLineSegment(sketch, "E184", {"start": v(-9.06, -70.2) * mm, "end": v(-9.06, -68.67) * mm});
            skLineSegment(sketch, "E185", {"start": v(15.07, -66.2) * mm, "end": v(15.07, -70.2) * mm});
            skLineSegment(sketch, "E186", {"start": v(15.07, -70.2) * mm, "end": v(8.72, -70.2) * mm});
            skLineSegment(sketch, "E187", {"start": v(8.72, -70.2) * mm, "end": v(8.72, -68.78) * mm});
            skLineSegment(sketch, "E188", {"start": v(27.76, -53.7) * mm, "end": v(31.77, -53.7) * mm});
            skLineSegment(sketch, "E189", {"start": v(31.77, -53.7) * mm, "end": v(31.77, -47.35) * mm});
            skLineSegment(sketch, "E190", {"start": v(31.77, -47.35) * mm, "end": v(30.44, -47.35) * mm});
            skLineSegment(sketch, "E191", {"start": v(27.98, -23.22) * mm, "end": v(31.77, -23.22) * mm});
            skLineSegment(sketch, "E192", {"start": v(31.77, -23.22) * mm, "end": v(31.77, -29.57) * mm});
            skLineSegment(sketch, "E193", {"start": v(31.77, -29.57) * mm, "end": v(30.56, -29.57) * mm});
            skArc(sketch, "E194.trimOffspring", {"start": v(-30.46, -29.36) * mm, "mid": v(-31.73, -38.25) * mm, "end": v(-30.46, -47.14) * mm});
            skArc(sketch, "E195.trimOffspring", {"start": v(-27.84, -53.49) * mm, "mid": v(-22.5, -60.62) * mm, "end": v(-15.41, -66) * mm});
            skArc(sketch, "E196.trimOffspring", {"start": v(-9.06, -68.67) * mm, "mid": v(-0.18, -70) * mm, "end": v(8.72, -68.78) * mm});
            skArc(sketch, "E197.trimOffspring", {"start": v(15.07, -66.2) * mm, "mid": v(22.3, -60.86) * mm, "end": v(27.76, -53.7) * mm});
            skArc(sketch, "E198.trimOffspring", {"start": v(30.44, -47.35) * mm, "mid": v(31.77, -38.46) * mm, "end": v(30.56, -29.57) * mm});
            skArc(sketch, "E199.trimOffspring", {"start": v(27.98, -23.22) * mm, "mid": v(22.51, -15.84) * mm, "end": v(15.16, -10.34) * mm});
            skArc(sketch, "E200.trimOffspring", {"start": v(8.81, -7.74) * mm, "mid": v(-0.08, -6.5) * mm, "end": v(-8.97, -7.8) * mm});
            skSolve(sketch);
        }
        {
            var Q0;
            Q0=makeQuery(id+"F22.imprint","IMPRINT",FACE,{"disambiguationData":[TD([[makeQuery(id+"F22.imprint","IMPRINT",EDGE,{"derivedFrom":sQuery(id+"F22.wireOp",EDGE,"E168")}),-1.0]])]});
            extrude(context, id + "F23", {"entities" : qUnion([Q0]), "operationType" : NewBodyOperationType.ADD, "oppositeDirection" : true, "depth" : 6.35 * mm});
        }
        {
            var Q0;
            Q0=makeQuery(id+"F1.opExtrude","SWEPT_FACE",FACE,{"disambiguationData":[OSD([sQuery(id+"F0.wireOp",EDGE,"E0.bottom")])]});
            var sketch = newSketch(context, id + "F24", { "sketchPlane" : qUnion([Q0])});
            skCircle(sketch, "E201", {"center": v(0, -38.3) * mm, "radius": 15.88 * mm});
            skPoint(sketch, "E201.centerSnap0", {"position": v(-37.63, -38.3) * mm});
            skArc(sketch, "E202", {"start": v(-15.4, -10.55) * mm, "mid": v(-22.52, -15.93) * mm, "end": v(-27.86, -23.08) * mm});
            skLineSegment(sketch, "E203", {"start": v(-15.4, -10.55) * mm, "end": v(-15.4, -6.33) * mm});
            skLineSegment(sketch, "E204", {"start": v(-15.4, -6.33) * mm, "end": v(-9.05, -6.33) * mm});
            skLineSegment(sketch, "E205", {"start": v(-9.05, -6.33) * mm, "end": v(-9.05, -7.88) * mm});
            skLineSegment(sketch, "E206", {"start": v(15.04, -10.35) * mm, "end": v(15.04, -6.37) * mm});
            skLineSegment(sketch, "E207", {"start": v(15.04, -6.37) * mm, "end": v(8.73, -6.37) * mm});
            skLineSegment(sketch, "E208", {"start": v(8.73, -6.37) * mm, "end": v(8.73, -7.78) * mm});
            skLineSegment(sketch, "E209", {"start": v(-30.48, -29.43) * mm, "end": v(-31.76, -29.43) * mm});
            skLineSegment(sketch, "E210", {"start": v(-31.76, -29.43) * mm, "end": v(-31.76, -23.08) * mm});
            skLineSegment(sketch, "E211", {"start": v(-31.76, -23.08) * mm, "end": v(-27.86, -23.08) * mm});
            skLineSegment(sketch, "E212", {"start": v(-30.48, -47.21) * mm, "end": v(-31.76, -47.21) * mm});
            skLineSegment(sketch, "E213", {"start": v(-31.76, -47.21) * mm, "end": v(-31.76, -53.56) * mm});
            skLineSegment(sketch, "E214", {"start": v(-31.76, -53.56) * mm, "end": v(-27.85, -53.56) * mm});
            skLineSegment(sketch, "E215", {"start": v(-15.32, -66.12) * mm, "end": v(-15.32, -69.76) * mm});
            skLineSegment(sketch, "E216", {"start": v(-15.32, -69.76) * mm, "end": v(-8.98, -69.76) * mm});
            skLineSegment(sketch, "E217", {"start": v(-8.98, -69.76) * mm, "end": v(-8.98, -68.76) * mm});
            skLineSegment(sketch, "E218", {"start": v(15.15, -66.21) * mm, "end": v(15.15, -69.8) * mm});
            skLineSegment(sketch, "E219", {"start": v(15.15, -69.8) * mm, "end": v(8.8, -69.8) * mm});
            skLineSegment(sketch, "E220", {"start": v(8.8, -69.8) * mm, "end": v(8.8, -68.81) * mm});
            skLineSegment(sketch, "E221", {"start": v(27.99, -53.3) * mm, "end": v(31.75, -53.3) * mm});
            skLineSegment(sketch, "E222", {"start": v(31.75, -53.3) * mm, "end": v(31.75, -46.98) * mm});
            skLineSegment(sketch, "E223", {"start": v(31.75, -46.98) * mm, "end": v(30.54, -46.98) * mm});
            skLineSegment(sketch, "E224", {"start": v(27.73, -22.84) * mm, "end": v(31.78, -22.84) * mm});
            skLineSegment(sketch, "E225", {"start": v(31.78, -22.84) * mm, "end": v(31.78, -29.2) * mm});
            skLineSegment(sketch, "E226", {"start": v(31.78, -29.2) * mm, "end": v(30.41, -29.2) * mm});
            skArc(sketch, "E227.trimOffspring", {"start": v(-30.48, -29.43) * mm, "mid": v(-31.75, -38.32) * mm, "end": v(-30.48, -47.21) * mm});
            skArc(sketch, "E228.trimOffspring", {"start": v(-27.85, -53.56) * mm, "mid": v(-22.48, -60.73) * mm, "end": v(-15.32, -66.12) * mm});
            skArc(sketch, "E229.trimOffspring", {"start": v(-8.98, -68.76) * mm, "mid": v(-0.1, -70.06) * mm, "end": v(8.8, -68.81) * mm});
            skArc(sketch, "E230.trimOffspring", {"start": v(15.15, -66.21) * mm, "mid": v(22.51, -60.7) * mm, "end": v(27.99, -53.3) * mm});
            skArc(sketch, "E231.trimOffspring", {"start": v(30.54, -46.98) * mm, "mid": v(31.75, -38.08) * mm, "end": v(30.41, -29.2) * mm});
            skArc(sketch, "E232.trimOffspring", {"start": v(27.73, -22.84) * mm, "mid": v(22.28, -15.69) * mm, "end": v(15.04, -10.35) * mm});
            skArc(sketch, "E233.trimOffspring", {"start": v(8.73, -7.78) * mm, "mid": v(-0.17, -6.56) * mm, "end": v(-9.05, -7.88) * mm});
            skPoint(sketch, "E234", {"position": v(-38.1, -38.3) * mm});
            skSolve(sketch);
        }
        {
            var Q0;
            Q0=makeQuery(id+"F24.imprint","IMPRINT",FACE,{"disambiguationData":[TD([[makeQuery(id+"F24.imprint","IMPRINT",EDGE,{"derivedFrom":sQuery(id+"F24.wireOp",EDGE,"E201")}),-1.0]])]});
            extrude(context, id + "F25", {"entities" : qUnion([Q0]), "operationType" : NewBodyOperationType.REMOVE, "oppositeDirection" : true, "depth" : 6.35 * mm});
        }
        {
            var Q0;
            Q0=makeQuery(id+"F25.boolean.opBoolean","COPY",FACE,{"derivedFrom":makeQuery(id+"F25.opExtrude","SWEPT_FACE",FACE,{"disambiguationData":[OSD([sQuery(id+"F24.wireOp",EDGE,"E216")])]})});
            var sketch = newSketch(context, id + "F26", { "sketchPlane" : qUnion([Q0])});
            skLineSegment(sketch, "E235", {"start": v(15.32, 38.1) * mm, "end": v(15.32, 31.75) * mm});
            skLineSegment(sketch, "E236", {"start": v(15.32, 31.75) * mm, "end": v(8.98, 31.75) * mm});
            skLineSegment(sketch, "E237", {"start": v(8.98, 31.75) * mm, "end": v(8.98, 38.1) * mm});
            skLineSegment(sketch, "E238", {"start": v(8.98, 38.1) * mm, "end": v(15.32, 38.1) * mm});
            skSolve(sketch);
        }
        {
            var Q0;
            Q0=makeQuery(id+"F26.imprint","IMPRINT",FACE,{"disambiguationData":[TD([[makeQuery(id+"F26.imprint","IMPRINT",EDGE,{"derivedFrom":sQuery(id+"F26.wireOp",EDGE,"E235")}),1.0]])]});
            extrude(context, id + "F27", {"entities" : qUnion([Q0]), "operationType" : NewBodyOperationType.REMOVE, "oppositeDirection" : true, "depth" : 25.4 * mm});
        }
        {
            var Q0;
            Q0=makeQuery(id+"F25.boolean.opBoolean","COPY",FACE,{"derivedFrom":makeQuery(id+"F25.opExtrude","SWEPT_FACE",FACE,{"disambiguationData":[OSD([sQuery(id+"F24.wireOp",EDGE,"E219")])]})});
            var sketch = newSketch(context, id + "F28", { "sketchPlane" : qUnion([Q0])});
            skLineSegment(sketch, "E239", {"start": v(-15.15, 38.1) * mm, "end": v(-15.15, 31.75) * mm});
            skLineSegment(sketch, "E240", {"start": v(-15.15, 31.75) * mm, "end": v(-8.8, 31.75) * mm});
            skLineSegment(sketch, "E241", {"start": v(-8.8, 31.75) * mm, "end": v(-8.8, 38.1) * mm});
            skLineSegment(sketch, "E242", {"start": v(-8.8, 38.1) * mm, "end": v(-15.15, 38.1) * mm});
            skSolve(sketch);
        }
        {
            var Q0;
            Q0=makeQuery(id+"F28.imprint","IMPRINT",FACE,{"disambiguationData":[TD([[makeQuery(id+"F28.imprint","IMPRINT",EDGE,{"derivedFrom":sQuery(id+"F28.wireOp",EDGE,"E239")}),-1.0]])]});
            extrude(context, id + "F29", {"entities" : qUnion([Q0]), "operationType" : NewBodyOperationType.REMOVE, "oppositeDirection" : true, "depth" : 25.4 * mm});
        }
        {
            var Q0;
            Q0=makeQuery(id+"F25.boolean.opBoolean","COPY",FACE,{"derivedFrom":makeQuery(id+"F25.opExtrude","SWEPT_FACE",FACE,{"disambiguationData":[OSD([sQuery(id+"F24.wireOp",EDGE,"E207")])]})});
            var sketch = newSketch(context, id + "F30", { "sketchPlane" : qUnion([Q0])});
            skLineSegment(sketch, "E243", {"start": v(8.73, 31.75) * mm, "end": v(8.73, 38.1) * mm});
            skLineSegment(sketch, "E244", {"start": v(8.73, 38.1) * mm, "end": v(15, 38.1) * mm});
            skLineSegment(sketch, "E245", {"start": v(15, 38.1) * mm, "end": v(15, 31.75) * mm});
            skLineSegment(sketch, "E246", {"start": v(15, 31.75) * mm, "end": v(8.73, 31.75) * mm});
            skSolve(sketch);
        }
        {
            var Q0;
            Q0=makeQuery(id+"F30.imprint","IMPRINT",FACE,{"disambiguationData":[TD([[makeQuery(id+"F30.imprint","IMPRINT",EDGE,{"derivedFrom":sQuery(id+"F30.wireOp",EDGE,"E243")}),-1.0]])]});
            extrude(context, id + "F31", {"entities" : qUnion([Q0]), "operationType" : NewBodyOperationType.REMOVE, "oppositeDirection" : true, "depth" : 25.4 * mm});
        }
        {
            var Q0;
            {var subQ0=sQuery(id+"F0.wireOp",EDGE,"E0.bottom");var subQ1=sQuery(id+"F0.wireOp",EDGE,"E0.right");Q0=makeQuery(id+"F7.boolean.opBoolean","SPLIT",EDGE,{"disambiguationData":[TD([makeQuery(id+"F1.opExtrude","SWEPT_FACE",FACE,{"disambiguationData":[OSD([subQ0])]})])],"derivedFrom":makeQuery(id+"F1.opExtrude","CAP_EDGE",EDGE,{"disambiguationData":[OSD([subQ1])],"isStart":false})});}
            var Q1;
            {var subQ0=sQuery(id+"F0.wireOp",EDGE,"E0.right");Q1=makeQuery(id+"F7.boolean.opBoolean","SPLIT",EDGE,{"disambiguationData":[TD([makeQuery(id+"F7.opExtrude","SWEPT_FACE",FACE,{"disambiguationData":[OSD([sQuery(id+"F6.wireOp",EDGE,"E70.bottom")])]})])],"derivedFrom":makeQuery(id+"F1.opExtrude","CAP_EDGE",EDGE,{"disambiguationData":[OSD([subQ0])],"isStart":false})});}
            var Q2;
            {var subQ0=sQuery(id+"F0.wireOp",EDGE,"E0.right");var subQ1=sQuery(id+"F0.wireOp",EDGE,"E0.top");Q2=makeQuery(id+"F7.boolean.opBoolean","SPLIT",EDGE,{"disambiguationData":[TD([makeQuery(id+"F1.opExtrude","SWEPT_FACE",FACE,{"disambiguationData":[OSD([subQ1])]})])],"derivedFrom":makeQuery(id+"F1.opExtrude","CAP_EDGE",EDGE,{"disambiguationData":[OSD([subQ0])],"isStart":false})});}
            var Q3;
            {var subQ0=sQuery(id+"F0.wireOp",EDGE,"E0.right");var subQ1=sQuery(id+"F0.wireOp",EDGE,"E0.bottom");Q3=makeQuery(id+"F19.boolean.opBoolean","SPLIT",EDGE,{"disambiguationData":[TD([makeQuery(id+"F1.opExtrude","SWEPT_FACE",FACE,{"disambiguationData":[OSD([subQ0])]})])],"derivedFrom":makeQuery(id+"F1.opExtrude","CAP_EDGE",EDGE,{"disambiguationData":[OSD([subQ1])],"isStart":false})});}
            var Q4;
            {var subQ0=sQuery(id+"F0.wireOp",EDGE,"E0.bottom");var subQ1=sQuery(id+"F0.wireOp",EDGE,"E0.right");Q4=makeQuery(id+"F7.boolean.opBoolean","SPLIT",EDGE,{"disambiguationData":[TD([makeQuery(id+"F7.opExtrude","SWEPT_FACE",FACE,{"disambiguationData":[OSD([sQuery(id+"F6.wireOp",EDGE,"E67.right"),sQuery(id+"F6.wireOp",EDGE,"E85.right")])]})])],"derivedFrom":makeQuery(id+"F1.opExtrude","SWEPT_EDGE",EDGE,{"disambiguationData":[OSD([subQ0,subQ1])]})});}
            var Q5;
            {var subQ0=makeQuery(id+"F9.boolean.opBoolean","COPY",FACE,{"derivedFrom":makeQuery(id+"F9.opExtrude","SWEPT_FACE",FACE,{"disambiguationData":[OSD([sQuery(id+"F8.wireOp",EDGE,"E119")])]})});var subQ1=sQuery(id+"F0.wireOp",EDGE,"E0.left");var subQ2=sQuery(id+"F0.wireOp",EDGE,"E0.bottom");Q5=makeQuery(id+"F21.boolean.opBoolean","SPLIT",EDGE,{"disambiguationData":[TD([subQ0])],"derivedFrom":makeQuery(id+"F19.boolean.opBoolean","SPLIT",EDGE,{"disambiguationData":[TD([makeQuery(id+"F1.opExtrude","SWEPT_FACE",FACE,{"disambiguationData":[OSD([subQ1])]})])],"derivedFrom":makeQuery(id+"F1.opExtrude","CAP_EDGE",EDGE,{"disambiguationData":[OSD([subQ2])],"isStart":false})})});}
            var Q6;
            {var subQ0=sQuery(id+"F0.wireOp",EDGE,"E0.left");var subQ1=makeQuery(id+"F1.opExtrude","SWEPT_FACE",FACE,{"disambiguationData":[OSD([subQ0])]});var subQ2=sQuery(id+"F0.wireOp",EDGE,"E0.bottom");Q6=makeQuery(id+"F21.boolean.opBoolean","SPLIT",EDGE,{"disambiguationData":[TD([subQ1])],"derivedFrom":makeQuery(id+"F19.boolean.opBoolean","SPLIT",EDGE,{"disambiguationData":[TD([subQ1])],"derivedFrom":makeQuery(id+"F1.opExtrude","CAP_EDGE",EDGE,{"disambiguationData":[OSD([subQ2])],"isStart":false})})});}
            var Q7;
            {var subQ0=sQuery(id+"F0.wireOp",EDGE,"E0.bottom");var subQ1=sQuery(id+"F0.wireOp",EDGE,"E0.right");Q7=makeQuery(id+"F7.boolean.opBoolean","SPLIT",EDGE,{"disambiguationData":[TD([makeQuery(id+"F7.opExtrude","SWEPT_FACE",FACE,{"disambiguationData":[OSD([sQuery(id+"F6.wireOp",EDGE,"E66.left"),sQuery(id+"F6.wireOp",EDGE,"E84.left")])]})])],"derivedFrom":makeQuery(id+"F1.opExtrude","SWEPT_EDGE",EDGE,{"disambiguationData":[OSD([subQ0,subQ1])]})});}
            var Q8;
            {var subQ0=sQuery(id+"F0.wireOp",EDGE,"E0.bottom");var subQ1=sQuery(id+"F0.wireOp",EDGE,"E0.right");Q8=makeQuery(id+"F7.boolean.opBoolean","SPLIT",EDGE,{"disambiguationData":[TD([makeQuery(id+"F7.opExtrude","SWEPT_FACE",FACE,{"disambiguationData":[OSD([sQuery(id+"F6.wireOp",EDGE,"E63.right"),sQuery(id+"F6.wireOp",EDGE,"E81.right")])]})])],"derivedFrom":makeQuery(id+"F1.opExtrude","SWEPT_EDGE",EDGE,{"disambiguationData":[OSD([subQ0,subQ1])]})});}
            var Q9;
            {var subQ0=sQuery(id+"F0.wireOp",EDGE,"E0.right");Q9=makeQuery(id+"F5.boolean.opBoolean","SPLIT",EDGE,{"disambiguationData":[TD([makeQuery(id+"F5.opExtrude","SWEPT_FACE",FACE,{"disambiguationData":[OSD([sQuery(id+"F4.wireOp",EDGE,"E26.bottom")])]})])],"derivedFrom":makeQuery(id+"F1.opExtrude","CAP_EDGE",EDGE,{"disambiguationData":[OSD([subQ0])],"isStart":true})});}
            var Q10;
            {var subQ0=sQuery(id+"F0.wireOp",EDGE,"E0.right");var subQ1=sQuery(id+"F0.wireOp",EDGE,"E0.top");Q10=makeQuery(id+"F5.boolean.opBoolean","SPLIT",EDGE,{"disambiguationData":[TD([makeQuery(id+"F1.opExtrude","SWEPT_FACE",FACE,{"disambiguationData":[OSD([subQ1])]})])],"derivedFrom":makeQuery(id+"F1.opExtrude","CAP_EDGE",EDGE,{"disambiguationData":[OSD([subQ0])],"isStart":true})});}
            var Q11;
            {var subQ0=sQuery(id+"F0.wireOp",EDGE,"E0.top");var subQ1=sQuery(id+"F0.wireOp",EDGE,"E0.right");Q11=makeQuery(id+"F7.boolean.opBoolean","SPLIT",EDGE,{"disambiguationData":[TD([makeQuery(id+"F7.opExtrude","SWEPT_FACE",FACE,{"disambiguationData":[OSD([sQuery(id+"F6.wireOp",EDGE,"E69.left"),sQuery(id+"F6.wireOp",EDGE,"E87.left")])]})])],"derivedFrom":makeQuery(id+"F1.opExtrude","SWEPT_EDGE",EDGE,{"disambiguationData":[OSD([subQ0,subQ1])]})});}
            var Q12;
            {var subQ0=sQuery(id+"F0.wireOp",EDGE,"E0.right");var subQ1=sQuery(id+"F0.wireOp",EDGE,"E0.top");Q12=makeQuery(id+"F7.boolean.opBoolean","SPLIT",EDGE,{"disambiguationData":[TD([makeQuery(id+"F7.opExtrude","SWEPT_FACE",FACE,{"disambiguationData":[OSD([sQuery(id+"F6.wireOp",EDGE,"E68.right"),sQuery(id+"F6.wireOp",EDGE,"E86.right")])]})])],"derivedFrom":makeQuery(id+"F1.opExtrude","SWEPT_EDGE",EDGE,{"disambiguationData":[OSD([subQ1,subQ0])]})});}
            var Q13;
            {var subQ0=sQuery(id+"F0.wireOp",EDGE,"E0.right");var subQ1=sQuery(id+"F0.wireOp",EDGE,"E0.top");Q13=makeQuery(id+"F9.boolean.opBoolean","SPLIT",EDGE,{"disambiguationData":[TD([makeQuery(id+"F1.opExtrude","SWEPT_FACE",FACE,{"disambiguationData":[OSD([subQ0])]})])],"derivedFrom":makeQuery(id+"F1.opExtrude","CAP_EDGE",EDGE,{"disambiguationData":[OSD([subQ1])],"isStart":false})});}
            var Q14;
            {var subQ0=sQuery(id+"F0.wireOp",EDGE,"E0.right");var subQ1=sQuery(id+"F0.wireOp",EDGE,"E0.top");Q14=makeQuery(id+"F7.boolean.opBoolean","SPLIT",EDGE,{"disambiguationData":[TD([makeQuery(id+"F7.opExtrude","SWEPT_FACE",FACE,{"disambiguationData":[OSD([sQuery(id+"F6.wireOp",EDGE,"E65.right"),sQuery(id+"F6.wireOp",EDGE,"E83.right")])]})])],"derivedFrom":makeQuery(id+"F1.opExtrude","SWEPT_EDGE",EDGE,{"disambiguationData":[OSD([subQ1,subQ0])]})});}
            var Q15;
            {var subQ0=sQuery(id+"F0.wireOp",EDGE,"E0.top");Q15=makeQuery(id+"F9.boolean.opBoolean","SPLIT",EDGE,{"disambiguationData":[TD([makeQuery(id+"F9.opExtrude","SWEPT_FACE",FACE,{"disambiguationData":[OSD([sQuery(id+"F8.wireOp",EDGE,"E117")])]})])],"derivedFrom":makeQuery(id+"F1.opExtrude","CAP_EDGE",EDGE,{"disambiguationData":[OSD([subQ0])],"isStart":false})});}
            var Q16;
            {var subQ0=sQuery(id+"F0.wireOp",EDGE,"E0.left");var subQ1=sQuery(id+"F0.wireOp",EDGE,"E0.top");Q16=makeQuery(id+"F9.boolean.opBoolean","SPLIT",EDGE,{"disambiguationData":[TD([makeQuery(id+"F1.opExtrude","SWEPT_FACE",FACE,{"disambiguationData":[OSD([subQ0])]})])],"derivedFrom":makeQuery(id+"F1.opExtrude","CAP_EDGE",EDGE,{"disambiguationData":[OSD([subQ1])],"isStart":false})});}
            var Q17;
            {var subQ0=sQuery(id+"F0.wireOp",EDGE,"E0.left");var subQ1=sQuery(id+"F0.wireOp",EDGE,"E0.top");Q17=makeQuery(id+"F3.boolean.opBoolean","SPLIT",EDGE,{"disambiguationData":[TD([makeQuery(id+"F1.opExtrude","SWEPT_FACE",FACE,{"disambiguationData":[OSD([subQ1])]})])],"derivedFrom":makeQuery(id+"F1.opExtrude","CAP_EDGE",EDGE,{"disambiguationData":[OSD([subQ0])],"isStart":false})});}
            var Q18;
            {var subQ0=sQuery(id+"F0.wireOp",EDGE,"E0.left");Q18=makeQuery(id+"F3.boolean.opBoolean","SPLIT",EDGE,{"disambiguationData":[TD([makeQuery(id+"F3.opExtrude","SWEPT_FACE",FACE,{"disambiguationData":[OSD([sQuery(id+"F2.wireOp",EDGE,"E2.bottom")])]})])],"derivedFrom":makeQuery(id+"F1.opExtrude","CAP_EDGE",EDGE,{"disambiguationData":[OSD([subQ0])],"isStart":false})});}
            var Q19;
            {var subQ0=sQuery(id+"F0.wireOp",EDGE,"E0.bottom");var subQ1=sQuery(id+"F0.wireOp",EDGE,"E0.left");Q19=makeQuery(id+"F3.boolean.opBoolean","SPLIT",EDGE,{"disambiguationData":[TD([makeQuery(id+"F1.opExtrude","SWEPT_FACE",FACE,{"disambiguationData":[OSD([subQ0])]})])],"derivedFrom":makeQuery(id+"F1.opExtrude","CAP_EDGE",EDGE,{"disambiguationData":[OSD([subQ1])],"isStart":false})});}
            var Q20;
            {var subQ0=sQuery(id+"F0.wireOp",EDGE,"E0.left");var subQ1=sQuery(id+"F0.wireOp",EDGE,"E0.top");Q20=makeQuery(id+"F3.boolean.opBoolean","SPLIT",EDGE,{"disambiguationData":[TD([makeQuery(id+"F3.opExtrude","SWEPT_FACE",FACE,{"disambiguationData":[OSD([sQuery(id+"F2.wireOp",EDGE,"E3.right")])]})])],"derivedFrom":makeQuery(id+"F1.opExtrude","SWEPT_EDGE",EDGE,{"disambiguationData":[OSD([subQ1,subQ0])]})});}
            var Q21;
            {var subQ0=sQuery(id+"F0.wireOp",EDGE,"E0.bottom");var subQ1=sQuery(id+"F0.wireOp",EDGE,"E0.left");Q21=makeQuery(id+"F3.boolean.opBoolean","SPLIT",EDGE,{"disambiguationData":[TD([makeQuery(id+"F3.opExtrude","SWEPT_FACE",FACE,{"disambiguationData":[OSD([sQuery(id+"F2.wireOp",EDGE,"E1.right")])]})])],"derivedFrom":makeQuery(id+"F1.opExtrude","SWEPT_EDGE",EDGE,{"disambiguationData":[OSD([subQ0,subQ1])]})});}
            var Q22;
            {var subQ0=sQuery(id+"F0.wireOp",EDGE,"E0.bottom");var subQ1=sQuery(id+"F0.wireOp",EDGE,"E0.left");Q22=makeQuery(id+"F3.boolean.opBoolean","SPLIT",EDGE,{"disambiguationData":[TD([makeQuery(id+"F3.opExtrude","SWEPT_FACE",FACE,{"disambiguationData":[OSD([sQuery(id+"F2.wireOp",EDGE,"E4.left")])]})])],"derivedFrom":makeQuery(id+"F1.opExtrude","SWEPT_EDGE",EDGE,{"disambiguationData":[OSD([subQ0,subQ1])]})});}
            var Q23;
            {var subQ0=sQuery(id+"F0.wireOp",EDGE,"E0.bottom");var subQ1=sQuery(id+"F0.wireOp",EDGE,"E0.left");Q23=makeQuery(id+"F3.boolean.opBoolean","SPLIT",EDGE,{"disambiguationData":[TD([makeQuery(id+"F3.opExtrude","SWEPT_FACE",FACE,{"disambiguationData":[OSD([sQuery(id+"F2.wireOp",EDGE,"E5.right")])]})])],"derivedFrom":makeQuery(id+"F1.opExtrude","SWEPT_EDGE",EDGE,{"disambiguationData":[OSD([subQ0,subQ1])]})});}
            var Q24;
            {var subQ0=sQuery(id+"F0.wireOp",EDGE,"E0.bottom");var subQ1=sQuery(id+"F0.wireOp",EDGE,"E0.left");Q24=makeQuery(id+"F3.boolean.opBoolean","SPLIT",EDGE,{"disambiguationData":[TD([makeQuery(id+"F1.opExtrude","SWEPT_FACE",FACE,{"disambiguationData":[OSD([subQ0])]})])],"derivedFrom":makeQuery(id+"F1.opExtrude","CAP_EDGE",EDGE,{"disambiguationData":[OSD([subQ1])],"isStart":true})});}
            var Q25;
            {var subQ0=sQuery(id+"F0.wireOp",EDGE,"E0.bottom");var subQ1=sQuery(id+"F0.wireOp",EDGE,"E0.left");Q25=makeQuery(id+"F5.boolean.opBoolean","SPLIT",EDGE,{"disambiguationData":[TD([makeQuery(id+"F1.opExtrude","SWEPT_FACE",FACE,{"disambiguationData":[OSD([subQ1])]})])],"derivedFrom":makeQuery(id+"F1.opExtrude","CAP_EDGE",EDGE,{"disambiguationData":[OSD([subQ0])],"isStart":true})});}
            var Q26;
            {var subQ0=sQuery(id+"F0.wireOp",EDGE,"E0.left");Q26=makeQuery(id+"F3.boolean.opBoolean","SPLIT",EDGE,{"disambiguationData":[TD([makeQuery(id+"F3.opExtrude","SWEPT_FACE",FACE,{"disambiguationData":[OSD([sQuery(id+"F2.wireOp",EDGE,"E8.bottom")])]})])],"derivedFrom":makeQuery(id+"F1.opExtrude","CAP_EDGE",EDGE,{"disambiguationData":[OSD([subQ0])],"isStart":true})});}
            var Q27;
            {var subQ0=sQuery(id+"F0.wireOp",EDGE,"E0.left");var subQ1=sQuery(id+"F0.wireOp",EDGE,"E0.top");Q27=makeQuery(id+"F3.boolean.opBoolean","SPLIT",EDGE,{"disambiguationData":[TD([makeQuery(id+"F1.opExtrude","SWEPT_FACE",FACE,{"disambiguationData":[OSD([subQ1])]})])],"derivedFrom":makeQuery(id+"F1.opExtrude","CAP_EDGE",EDGE,{"disambiguationData":[OSD([subQ0])],"isStart":true})});}
            var Q28;
            {var subQ0=sQuery(id+"F0.wireOp",EDGE,"E0.left");var subQ1=sQuery(id+"F0.wireOp",EDGE,"E0.top");Q28=makeQuery(id+"F3.boolean.opBoolean","SPLIT",EDGE,{"disambiguationData":[TD([makeQuery(id+"F3.opExtrude","SWEPT_FACE",FACE,{"disambiguationData":[OSD([sQuery(id+"F2.wireOp",EDGE,"E6.right")])]})])],"derivedFrom":makeQuery(id+"F1.opExtrude","SWEPT_EDGE",EDGE,{"disambiguationData":[OSD([subQ1,subQ0])]})});}
            var Q29;
            {var subQ0=sQuery(id+"F0.wireOp",EDGE,"E0.left");var subQ1=sQuery(id+"F0.wireOp",EDGE,"E0.top");Q29=makeQuery(id+"F5.boolean.opBoolean","SPLIT",EDGE,{"disambiguationData":[TD([makeQuery(id+"F1.opExtrude","SWEPT_FACE",FACE,{"disambiguationData":[OSD([subQ0])]})])],"derivedFrom":makeQuery(id+"F1.opExtrude","CAP_EDGE",EDGE,{"disambiguationData":[OSD([subQ1])],"isStart":true})});}
            var Q30;
            {var subQ0=sQuery(id+"F0.wireOp",EDGE,"E0.top");var subQ1=sQuery(id+"F0.wireOp",EDGE,"E0.left");Q30=makeQuery(id+"F3.boolean.opBoolean","SPLIT",EDGE,{"disambiguationData":[TD([makeQuery(id+"F3.opExtrude","SWEPT_FACE",FACE,{"disambiguationData":[OSD([sQuery(id+"F2.wireOp",EDGE,"E7.left")])]})])],"derivedFrom":makeQuery(id+"F1.opExtrude","SWEPT_EDGE",EDGE,{"disambiguationData":[OSD([subQ0,subQ1])]})});}
            var Q31;
            {var subQ0=sQuery(id+"F0.wireOp",EDGE,"E0.top");Q31=makeQuery(id+"F5.boolean.opBoolean","SPLIT",EDGE,{"disambiguationData":[TD([makeQuery(id+"F5.opExtrude","SWEPT_FACE",FACE,{"disambiguationData":[OSD([sQuery(id+"F4.wireOp",EDGE,"E25.left"),sQuery(id+"F4.wireOp",EDGE,"E43.left")])]})])],"derivedFrom":makeQuery(id+"F1.opExtrude","CAP_EDGE",EDGE,{"disambiguationData":[OSD([subQ0])],"isStart":true})});}
            var Q32;
            {var subQ0=sQuery(id+"F0.wireOp",EDGE,"E0.right");var subQ1=sQuery(id+"F0.wireOp",EDGE,"E0.top");Q32=makeQuery(id+"F5.boolean.opBoolean","SPLIT",EDGE,{"disambiguationData":[TD([makeQuery(id+"F1.opExtrude","SWEPT_FACE",FACE,{"disambiguationData":[OSD([subQ0])]})])],"derivedFrom":makeQuery(id+"F1.opExtrude","CAP_EDGE",EDGE,{"disambiguationData":[OSD([subQ1])],"isStart":true})});}
            var Q33;
            {var subQ0=sQuery(id+"F0.wireOp",EDGE,"E0.bottom");var subQ1=sQuery(id+"F0.wireOp",EDGE,"E0.right");Q33=makeQuery(id+"F5.boolean.opBoolean","SPLIT",EDGE,{"disambiguationData":[TD([makeQuery(id+"F1.opExtrude","SWEPT_FACE",FACE,{"disambiguationData":[OSD([subQ0])]})])],"derivedFrom":makeQuery(id+"F1.opExtrude","CAP_EDGE",EDGE,{"disambiguationData":[OSD([subQ1])],"isStart":true})});}
            var Q34;
            {var subQ0=sQuery(id+"F0.wireOp",EDGE,"E0.bottom");var subQ1=sQuery(id+"F0.wireOp",EDGE,"E0.right");Q34=makeQuery(id+"F5.boolean.opBoolean","SPLIT",EDGE,{"disambiguationData":[TD([makeQuery(id+"F1.opExtrude","SWEPT_FACE",FACE,{"disambiguationData":[OSD([subQ1])]})])],"derivedFrom":makeQuery(id+"F1.opExtrude","CAP_EDGE",EDGE,{"disambiguationData":[OSD([subQ0])],"isStart":true})});}
            var Q35;
            {var subQ0=sQuery(id+"F0.wireOp",EDGE,"E0.bottom");Q35=makeQuery(id+"F5.boolean.opBoolean","SPLIT",EDGE,{"disambiguationData":[TD([makeQuery(id+"F5.opExtrude","SWEPT_FACE",FACE,{"disambiguationData":[OSD([sQuery(id+"F4.wireOp",EDGE,"E22.left"),sQuery(id+"F4.wireOp",EDGE,"E40.left")])]})])],"derivedFrom":makeQuery(id+"F1.opExtrude","CAP_EDGE",EDGE,{"disambiguationData":[OSD([subQ0])],"isStart":true})});}
            chamfer(context, id + "F32", {"entities" : qUnion([Q0, Q1, Q2, Q3, Q4, Q5, Q6, Q7, Q8, Q9, Q10, Q11, Q12, Q13, Q14, Q15, Q16, Q17, Q18, Q19, Q20, Q21, Q22, Q23, Q24, Q25, Q26, Q27, Q28, Q29, Q30, Q31, Q32, Q33, Q34, Q35]), "width" : 2.54 * mm, "tangentPropagation" : true});
        }
        {
            var Q0;
            Q0=makeQuery(id+"F25.boolean.opBoolean","SPLIT",FACE,{"disambiguationData":[TD([makeQuery(id+"F25.opExtrude","SWEPT_FACE",FACE,{"disambiguationData":[OSD([sQuery(id+"F24.wireOp",EDGE,"E201")])]})])],"derivedFrom":makeQuery(id+"F1.opExtrude","SWEPT_FACE",FACE,{"disambiguationData":[OSD([sQuery(id+"F0.wireOp",EDGE,"E0.bottom")])]})});
            var sketch = newSketch(context, id + "F33", { "sketchPlane" : qUnion([Q0])});
            skLineSegment(sketch, "E247", {"start": v(0, 0) * mm, "end": v(0, -76.54) * mm, "construction": true});
            skLineSegment(sketch, "E248", {"start": v(0, -38.3) * mm, "end": v(38.35, -38.3) * mm, "construction": true});
            skLineSegment(sketch, "E249", {"start": v(0, -28.66) * mm, "end": v(0, -50.25) * mm, "construction": true});
            skFitSpline(sketch, "E250", {"points": [v(0, -34.43) * mm, v(-1.02, -32.59) * mm, v(-2.74, -31.55) * mm, v(-5.28, -31.62) * mm, v(-7.4, -33.37) * mm, v(-7.96, -36.93) * mm, v(-5.55, -40.48) * mm, v(-2.4, -43.66) * mm, v(0, -47.5) * mm], "startDerivative": vector(-5.07, 15.4) * mm, "endDerivative": vector(17.71, -27.95) * mm});
            skFitSpline(sketch, "E251.MirrorCS", {"points": [v(0, -34.43) * mm, v(1.02, -32.59) * mm, v(2.74, -31.55) * mm, v(5.28, -31.62) * mm, v(7.4, -33.37) * mm, v(7.96, -36.93) * mm, v(5.55, -40.48) * mm, v(2.4, -43.66) * mm, v(0, -47.5) * mm], "startDerivative": vector(5.07, 15.4) * mm, "endDerivative": vector(-17.71, -27.95) * mm});
            skSolve(sketch);
        }
        {
            var Q0;
            Q0 = qSketchRegion(id + "F33", true);
            extrude(context, id + "F34", {"entities" : qUnion([Q0]), "operationType" : NewBodyOperationType.ADD, "depth" : 0.76 * mm});
        }
        {
            var Q0;
            Q0=makeQuery(id+"F9.boolean.opBoolean","SPLIT",FACE,{"disambiguationData":[TD([makeQuery(id+"F9.opExtrude","SWEPT_FACE",FACE,{"disambiguationData":[OSD([sQuery(id+"F8.wireOp",EDGE,"E107")])]})])],"derivedFrom":makeQuery(id+"F1.opExtrude","CAP_FACE",FACE,{"disambiguationData":[OSD([sQuery(id+"F0.wireOp",EDGE,"E0.bottom"),sQuery(id+"F0.wireOp",EDGE,"E0.top"),sQuery(id+"F0.wireOp",EDGE,"E0.left"),sQuery(id+"F0.wireOp",EDGE,"E0.right")])],"isStart":false})});
            var sketch = newSketch(context, id + "F35", { "sketchPlane" : qUnion([Q0])});
            skLineSegment(sketch, "E252", {"start": v(-0.38, 9.4) * mm, "end": v(-0.38, -12.19) * mm, "construction": true});
            skFitSpline(sketch, "E253", {"points": [v(-0.38, 3.63) * mm, v(-1.4, 5.47) * mm, v(-3.12, 6.5) * mm, v(-5.67, 6.44) * mm, v(-7.79, 4.69) * mm, v(-8.34, 1.13) * mm, v(-5.93, -2.42) * mm, v(-2.78, -5.6) * mm, v(-0.38, -9.44) * mm], "startDerivative": vector(-5.07, 15.4) * mm, "endDerivative": vector(17.71, -27.95) * mm});
            skFitSpline(sketch, "E254.MirrorCS", {"points": [v(-0.38, 3.63) * mm, v(0.64, 5.47) * mm, v(2.36, 6.5) * mm, v(4.9, 6.44) * mm, v(7.02, 4.69) * mm, v(7.58, 1.13) * mm, v(5.16, -2.42) * mm, v(2.02, -5.6) * mm, v(-0.38, -9.44) * mm], "startDerivative": vector(5.07, 15.4) * mm, "endDerivative": vector(-17.71, -27.95) * mm});
            skSolve(sketch);
        }
        {
            var Q0;
            Q0=makeQuery(id+"F35.imprint","IMPRINT",FACE,{"disambiguationData":[TD([[makeQuery(id+"F35.imprint","IMPRINT",EDGE,{"derivedFrom":sQuery(id+"F35.wireOp",EDGE,"E253")}),1.0]])]});
            extrude(context, id + "F36", {"entities" : qUnion([Q0]), "operationType" : NewBodyOperationType.ADD, "depth" : 0.76 * mm});
        }
        {
            var Q0;
            Q0=makeQuery(id+"F5.boolean.opBoolean","SPLIT",FACE,{"disambiguationData":[TD([makeQuery(id+"F5.opExtrude","SWEPT_FACE",FACE,{"disambiguationData":[OSD([sQuery(id+"F4.wireOp",EDGE,"E28")])]})])],"derivedFrom":makeQuery(id+"F1.opExtrude","CAP_FACE",FACE,{"disambiguationData":[OSD([sQuery(id+"F0.wireOp",EDGE,"E0.bottom"),sQuery(id+"F0.wireOp",EDGE,"E0.top"),sQuery(id+"F0.wireOp",EDGE,"E0.left"),sQuery(id+"F0.wireOp",EDGE,"E0.right")])],"isStart":true})});
            var sketch = newSketch(context, id + "F37", { "sketchPlane" : qUnion([Q0])});
            skLineSegment(sketch, "E255", {"start": v(-0.18, 9.04) * mm, "end": v(-0.18, -12.55) * mm, "construction": true});
            skFitSpline(sketch, "E256", {"points": [v(-0.18, 3.27) * mm, v(-1.2, 5.1) * mm, v(-2.93, 6.15) * mm, v(-5.47, 6.08) * mm, v(-7.59, 4.33) * mm, v(-8.14, 0.77) * mm, v(-5.73, -2.78) * mm, v(-2.58, -5.96) * mm, v(-0.18, -9.8) * mm], "startDerivative": vector(-5.07, 15.4) * mm, "endDerivative": vector(17.71, -27.95) * mm});
            skFitSpline(sketch, "E257.MirrorCS", {"points": [v(-0.18, 3.27) * mm, v(0.84, 5.1) * mm, v(2.56, 6.15) * mm, v(5.1, 6.08) * mm, v(7.22, 4.33) * mm, v(7.77, 0.77) * mm, v(5.36, -2.78) * mm, v(2.21, -5.96) * mm, v(-0.18, -9.8) * mm], "startDerivative": vector(5.07, 15.4) * mm, "endDerivative": vector(-17.71, -27.95) * mm});
            skSolve(sketch);
        }
        {
            var Q0;
            Q0=makeQuery(id+"F37.imprint","IMPRINT",FACE,{"disambiguationData":[TD([[makeQuery(id+"F37.imprint","IMPRINT",EDGE,{"derivedFrom":sQuery(id+"F37.wireOp",EDGE,"E256")}),1.0]])]});
            extrude(context, id + "F38", {"entities" : qUnion([Q0]), "operationType" : NewBodyOperationType.ADD, "depth" : 0.76 * mm});
        }
        {
            var Q0;
            Q0=makeQuery(id+"F3.boolean.opBoolean","SPLIT",FACE,{"disambiguationData":[TD([makeQuery(id+"F3.opExtrude","SWEPT_FACE",FACE,{"disambiguationData":[OSD([sQuery(id+"F2.wireOp",EDGE,"E10")])]})])],"derivedFrom":makeQuery(id+"F1.opExtrude","SWEPT_FACE",FACE,{"disambiguationData":[OSD([sQuery(id+"F0.wireOp",EDGE,"E0.left")])]})});
            var sketch = newSketch(context, id + "F39", { "sketchPlane" : qUnion([Q0])});
            skLineSegment(sketch, "E258", {"start": v(-38.36, 9.78) * mm, "end": v(-38.36, -11.81) * mm, "construction": true});
            skFitSpline(sketch, "E259", {"points": [v(-38.36, 4) * mm, v(-39.38, 5.85) * mm, v(-41.1, 6.88) * mm, v(-43.64, 6.82) * mm, v(-45.76, 5.06) * mm, v(-46.32, 1.5) * mm, v(-43.9, -2.05) * mm, v(-40.76, -5.23) * mm, v(-38.36, -9.07) * mm], "startDerivative": vector(-5.07, 15.4) * mm, "endDerivative": vector(17.71, -27.95) * mm});
            skFitSpline(sketch, "E260.MirrorCS", {"points": [v(-38.36, 4) * mm, v(-37.34, 5.85) * mm, v(-35.62, 6.88) * mm, v(-33.07, 6.82) * mm, v(-30.95, 5.06) * mm, v(-30.4, 1.5) * mm, v(-32.81, -2.05) * mm, v(-35.96, -5.23) * mm, v(-38.36, -9.07) * mm], "startDerivative": vector(5.07, 15.4) * mm, "endDerivative": vector(-17.71, -27.95) * mm});
            skSolve(sketch);
        }
        {
            var Q0;
            Q0=makeQuery(id+"F39.imprint","IMPRINT",FACE,{"disambiguationData":[TD([[makeQuery(id+"F39.imprint","IMPRINT",EDGE,{"derivedFrom":sQuery(id+"F39.wireOp",EDGE,"E259")}),1.0]])]});
            extrude(context, id + "F40", {"entities" : qUnion([Q0]), "operationType" : NewBodyOperationType.ADD, "depth" : 0.76 * mm});
        }
        {
            var Q0;
            Q0=makeQuery(id+"F7.boolean.opBoolean","SPLIT",FACE,{"disambiguationData":[TD([makeQuery(id+"F7.opExtrude","SWEPT_FACE",FACE,{"disambiguationData":[OSD([sQuery(id+"F6.wireOp",EDGE,"E72")])]})])],"derivedFrom":makeQuery(id+"F1.opExtrude","SWEPT_FACE",FACE,{"disambiguationData":[OSD([sQuery(id+"F0.wireOp",EDGE,"E0.right")])]})});
            var sketch = newSketch(context, id + "F41", { "sketchPlane" : qUnion([Q0])});
            skLineSegment(sketch, "E261", {"start": v(38.12, 9.76) * mm, "end": v(38.12, -11.83) * mm, "construction": true});
            skFitSpline(sketch, "E262", {"points": [v(38.12, 4) * mm, v(37.1, 5.83) * mm, v(35.38, 6.87) * mm, v(32.84, 6.8) * mm, v(30.72, 5.05) * mm, v(30.16, 1.5) * mm, v(32.58, -2.06) * mm, v(35.73, -5.24) * mm, v(38.12, -9.08) * mm], "startDerivative": vector(-5.07, 15.4) * mm, "endDerivative": vector(17.71, -27.95) * mm});
            skFitSpline(sketch, "E263.MirrorCS", {"points": [v(38.12, 4) * mm, v(39.15, 5.83) * mm, v(40.87, 6.87) * mm, v(43.4, 6.8) * mm, v(45.53, 5.05) * mm, v(46.08, 1.5) * mm, v(43.67, -2.06) * mm, v(40.52, -5.24) * mm, v(38.12, -9.08) * mm], "startDerivative": vector(5.07, 15.4) * mm, "endDerivative": vector(-17.71, -27.95) * mm});
            skSolve(sketch);
        }
        {
            var Q0;
            Q0=makeQuery(id+"F41.imprint","IMPRINT",FACE,{"disambiguationData":[TD([[makeQuery(id+"F41.imprint","IMPRINT",EDGE,{"derivedFrom":sQuery(id+"F41.wireOp",EDGE,"E262")}),1.0]])]});
            extrude(context, id + "F42", {"entities" : qUnion([Q0]), "operationType" : NewBodyOperationType.ADD, "depth" : 0.76 * mm});
        }
        {
            var Q0;
            Q0=makeQuery(id+"F42.opExtrude","CAP_FACE",FACE,{"disambiguationData":[OSD([sQuery(id+"F41.wireOp",EDGE,"E262"),sQuery(id+"F41.wireOp",EDGE,"E263.MirrorCS")])],"isStart":false});
            fillet(context, id + "F43", {"entities" : qUnion([Q0]), "radius" : 0.76 * mm, "tangentPropagation" : true, "allowEdgeOverflow" : false});
        }
        {
            var Q0;
            Q0=makeQuery(id+"F40.opExtrude","CAP_FACE",FACE,{"disambiguationData":[OSD([sQuery(id+"F39.wireOp",EDGE,"E259"),sQuery(id+"F39.wireOp",EDGE,"E260.MirrorCS")])],"isStart":false});
            fillet(context, id + "F44", {"entities" : qUnion([Q0]), "radius" : 0.76 * mm, "tangentPropagation" : true, "allowEdgeOverflow" : false});
        }
        {
            var Q0;
            Q0=makeQuery(id+"F38.opExtrude","CAP_FACE",FACE,{"disambiguationData":[OSD([sQuery(id+"F37.wireOp",EDGE,"E256"),sQuery(id+"F37.wireOp",EDGE,"E257.MirrorCS")])],"isStart":false});
            fillet(context, id + "F45", {"entities" : qUnion([Q0]), "radius" : 0.76 * mm, "tangentPropagation" : true, "allowEdgeOverflow" : false});
        }
        {
            var Q0;
            Q0=makeQuery(id+"F36.opExtrude","CAP_FACE",FACE,{"disambiguationData":[OSD([sQuery(id+"F35.wireOp",EDGE,"E253"),sQuery(id+"F35.wireOp",EDGE,"E254.MirrorCS")])],"isStart":false});
            fillet(context, id + "F46", {"entities" : qUnion([Q0]), "radius" : 0.76 * mm, "tangentPropagation" : true, "allowEdgeOverflow" : false});
        }
        {
            var Q0;
            Q0=makeQuery(id+"F21.boolean.opBoolean","MERGE",FACE,{"derivedFrom":[makeQuery(id+"F19.boolean.opBoolean","MERGE",FACE,{"derivedFrom":[makeQuery(id+"F13.boolean.opBoolean","MERGE",FACE,{"derivedFrom":[makeQuery(id+"F11.boolean.opBoolean","MERGE",FACE,{"derivedFrom":[makeQuery(id+"F9.boolean.opBoolean","COPY",FACE,{"derivedFrom":makeQuery(id+"F9.opExtrude","CAP_FACE",FACE,{"disambiguationData":[OSD([sQuery(id+"F0.wireOp",EDGE,"E0.top"),sQuery(id+"F0.wireOp",EDGE,"E0.right"),sQuery(id+"F6.wireOp",EDGE,"E68.top"),sQuery(id+"F6.wireOp",EDGE,"E70.bottom"),sQuery(id+"F8.wireOp",EDGE,"E106"),sQuery(id+"F8.wireOp",EDGE,"E107"),sQuery(id+"F8.wireOp",EDGE,"E110"),sQuery(id+"F8.wireOp",EDGE,"E111"),sQuery(id+"F8.wireOp",EDGE,"E112"),sQuery(id+"F8.wireOp",EDGE,"E114"),sQuery(id+"F8.wireOp",EDGE,"E117"),sQuery(id+"F8.wireOp",EDGE,"E118"),sQuery(id+"F8.wireOp",EDGE,"E119"),sQuery(id+"F8.wireOp",EDGE,"E120"),sQuery(id+"F8.wireOp",EDGE,"E121"),sQuery(id+"F8.wireOp",EDGE,"E123"),sQuery(id+"F8.wireOp",EDGE,"E124"),sQuery(id+"F8.wireOp",EDGE,"E125"),sQuery(id+"F8.wireOp",EDGE,"E126"),sQuery(id+"F8.wireOp",EDGE,"E127"),sQuery(id+"F8.wireOp",EDGE,"E128"),sQuery(id+"F8.wireOp",EDGE,"E129"),sQuery(id+"F8.wireOp",EDGE,"E130"),sQuery(id+"F8.wireOp",EDGE,"E131"),sQuery(id+"F8.wireOp",EDGE,"E132"),sQuery(id+"F8.wireOp",EDGE,"E133"),sQuery(id+"F8.wireOp",EDGE,"E134"),sQuery(id+"F8.wireOp",EDGE,"E135"),sQuery(id+"F8.wireOp",EDGE,"E136.trimOffspring"),sQuery(id+"F8.wireOp",EDGE,"E137.trimOffspring"),sQuery(id+"F8.wireOp",EDGE,"E138.trimOffspring"),sQuery(id+"F8.wireOp",EDGE,"E139.trimOffspring"),sQuery(id+"F8.wireOp",EDGE,"E140.trimOffspring"),sQuery(id+"F8.wireOp",EDGE,"E141.trimOffspring"),sQuery(id+"F8.wireOp",EDGE,"E142.trimOffspring")])],"isStart":false})}),makeQuery(id+"F11.opExtrude","SWEPT_FACE",FACE,{"disambiguationData":[OSD([sQuery(id+"F10.wireOp",EDGE,"E146")])]})]}),makeQuery(id+"F13.opExtrude","SWEPT_FACE",FACE,{"disambiguationData":[OSD([sQuery(id+"F12.wireOp",EDGE,"E150")])]})]}),makeQuery(id+"F19.opExtrude","SWEPT_FACE",FACE,{"disambiguationData":[OSD([sQuery(id+"F18.wireOp",EDGE,"E160")])]})]}),makeQuery(id+"F21.opExtrude","SWEPT_FACE",FACE,{"disambiguationData":[OSD([sQuery(id+"F20.wireOp",EDGE,"E164")])]})]});
            var sketch = newSketch(context, id + "F47", { "sketchPlane" : qUnion([Q0])});
            skLineSegment(sketch, "E264", {"start": v(-31.75, 1.27) * mm, "end": v(-15.91, 1.27) * mm});
            skLineSegment(sketch, "E265", {"start": v(-15.92, -1.27) * mm, "end": v(-31.75, -1.27) * mm});
            skArc(sketch, "E266", {"start": v(-15.91, 1.27) * mm, "mid": v(-15.97, 0) * mm, "end": v(-15.92, -1.27) * mm});
            skPoint(sketch, "E267.end.orphan", {"position": v(-31.75, 0) * mm});
            skLineSegment(sketch, "E268", {"start": v(-31.75, -1.27) * mm, "end": v(-31.75, 1.27) * mm});
            skSolve(sketch);
        }
        {
            var Q0;
            Q0=makeQuery(id+"F47.imprint","IMPRINT",FACE,{"disambiguationData":[TD([[makeQuery(id+"F47.imprint","IMPRINT",EDGE,{"derivedFrom":sQuery(id+"F47.wireOp",EDGE,"E264")}),-1.0]])]});
            extrude(context, id + "F48", {"entities" : qUnion([Q0]), "operationType" : NewBodyOperationType.REMOVE, "oppositeDirection" : true, "depth" : 0.5 * mm});
        }
        {
            var Q0;
            Q0=makeQuery(id+"F21.boolean.opBoolean","MERGE",FACE,{"derivedFrom":[makeQuery(id+"F19.boolean.opBoolean","MERGE",FACE,{"derivedFrom":[makeQuery(id+"F13.boolean.opBoolean","MERGE",FACE,{"derivedFrom":[makeQuery(id+"F11.boolean.opBoolean","MERGE",FACE,{"derivedFrom":[makeQuery(id+"F9.boolean.opBoolean","COPY",FACE,{"derivedFrom":makeQuery(id+"F9.opExtrude","CAP_FACE",FACE,{"disambiguationData":[OSD([sQuery(id+"F0.wireOp",EDGE,"E0.top"),sQuery(id+"F0.wireOp",EDGE,"E0.right"),sQuery(id+"F6.wireOp",EDGE,"E68.top"),sQuery(id+"F6.wireOp",EDGE,"E70.bottom"),sQuery(id+"F8.wireOp",EDGE,"E106"),sQuery(id+"F8.wireOp",EDGE,"E107"),sQuery(id+"F8.wireOp",EDGE,"E110"),sQuery(id+"F8.wireOp",EDGE,"E111"),sQuery(id+"F8.wireOp",EDGE,"E112"),sQuery(id+"F8.wireOp",EDGE,"E114"),sQuery(id+"F8.wireOp",EDGE,"E117"),sQuery(id+"F8.wireOp",EDGE,"E118"),sQuery(id+"F8.wireOp",EDGE,"E119"),sQuery(id+"F8.wireOp",EDGE,"E120"),sQuery(id+"F8.wireOp",EDGE,"E121"),sQuery(id+"F8.wireOp",EDGE,"E123"),sQuery(id+"F8.wireOp",EDGE,"E124"),sQuery(id+"F8.wireOp",EDGE,"E125"),sQuery(id+"F8.wireOp",EDGE,"E126"),sQuery(id+"F8.wireOp",EDGE,"E127"),sQuery(id+"F8.wireOp",EDGE,"E128"),sQuery(id+"F8.wireOp",EDGE,"E129"),sQuery(id+"F8.wireOp",EDGE,"E130"),sQuery(id+"F8.wireOp",EDGE,"E131"),sQuery(id+"F8.wireOp",EDGE,"E132"),sQuery(id+"F8.wireOp",EDGE,"E133"),sQuery(id+"F8.wireOp",EDGE,"E134"),sQuery(id+"F8.wireOp",EDGE,"E135"),sQuery(id+"F8.wireOp",EDGE,"E136.trimOffspring"),sQuery(id+"F8.wireOp",EDGE,"E137.trimOffspring"),sQuery(id+"F8.wireOp",EDGE,"E138.trimOffspring"),sQuery(id+"F8.wireOp",EDGE,"E139.trimOffspring"),sQuery(id+"F8.wireOp",EDGE,"E140.trimOffspring"),sQuery(id+"F8.wireOp",EDGE,"E141.trimOffspring"),sQuery(id+"F8.wireOp",EDGE,"E142.trimOffspring")])],"isStart":false})}),makeQuery(id+"F11.opExtrude","SWEPT_FACE",FACE,{"disambiguationData":[OSD([sQuery(id+"F10.wireOp",EDGE,"E146")])]})]}),makeQuery(id+"F13.opExtrude","SWEPT_FACE",FACE,{"disambiguationData":[OSD([sQuery(id+"F12.wireOp",EDGE,"E150")])]})]}),makeQuery(id+"F19.opExtrude","SWEPT_FACE",FACE,{"disambiguationData":[OSD([sQuery(id+"F18.wireOp",EDGE,"E160")])]})]}),makeQuery(id+"F21.opExtrude","SWEPT_FACE",FACE,{"disambiguationData":[OSD([sQuery(id+"F20.wireOp",EDGE,"E164")])]})]});
            var sketch = newSketch(context, id + "F49", { "sketchPlane" : qUnion([Q0])});
            skLineSegment(sketch, "E269", {"start": v(0, 15.83) * mm, "end": v(1.27, 15.77) * mm});
            skLineSegment(sketch, "E270", {"start": v(0, 15.83) * mm, "end": v(-1.27, 15.79) * mm});
            skLineSegment(sketch, "E271", {"start": v(-1.27, 15.79) * mm, "end": v(-1.27, 31.68) * mm});
            skLineSegment(sketch, "E272", {"start": v(-1.27, 31.68) * mm, "end": v(1.27, 31.68) * mm});
            skLineSegment(sketch, "E273", {"start": v(1.27, 31.68) * mm, "end": v(1.27, 15.77) * mm});
            skLineSegment(sketch, "E274", {"start": v(15.73, -1.27) * mm, "end": v(31.63, -1.27) * mm});
            skLineSegment(sketch, "E275", {"start": v(15.73, 1.27) * mm, "end": v(31.63, 1.27) * mm});
            skArc(sketch, "E276", {"start": v(15.73, -1.27) * mm, "mid": v(15.78, 0) * mm, "end": v(15.73, 1.27) * mm});
            skPoint(sketch, "E277.end.orphan", {"position": v(31.71, 0) * mm});
            skLineSegment(sketch, "E278", {"start": v(31.63, -1.27) * mm, "end": v(31.66, 0) * mm});
            skLineSegment(sketch, "E279", {"start": v(31.66, 0) * mm, "end": v(31.63, 1.27) * mm});
            skLineSegment(sketch, "E280", {"start": v(-1.27, -15.88) * mm, "end": v(-1.27, -31.75) * mm});
            skLineSegment(sketch, "E281", {"start": v(-1.27, -31.75) * mm, "end": v(1.6, -31.75) * mm});
            skLineSegment(sketch, "E282", {"start": v(1.6, -31.75) * mm, "end": v(1.6, -15.83) * mm});
            skPoint(sketch, "E283.end.orphan", {"position": v(0, -16) * mm});
            skArc(sketch, "E284", {"start": v(-1.27, -15.88) * mm, "mid": v(0.17, -15.92) * mm, "end": v(1.6, -15.83) * mm});
            skLineSegment(sketch, "E285", {"start": v(-1.27, -31.75) * mm, "end": v(0.17, -31.75) * mm});
            skLineSegment(sketch, "E286", {"start": v(0.17, -31.75) * mm, "end": v(1.6, -31.75) * mm});
            skSolve(sketch);
        }
        {
            var Q0;
            {var subQ5=sQuery(id+"F49.wireOp",EDGE,"E271");Q0=makeQuery(id+"F49.imprint","IMPRINT",FACE,{"disambiguationData":[TD([[makeQuery(id+"F49.imprint","IMPRINT",EDGE,{"derivedFrom":subQ5}),-1.0]])]});}
            var Q1;
            {var subQ1=sQuery(id+"F49.wireOp",EDGE,"E274");Q1=makeQuery(id+"F49.imprint","IMPRINT",FACE,{"disambiguationData":[TD([[makeQuery(id+"F49.imprint","IMPRINT",EDGE,{"derivedFrom":subQ1}),1.0]])]});}
            var Q2;
            {var subQ1=sQuery(id+"F49.wireOp",EDGE,"E280");Q2=makeQuery(id+"F49.imprint","IMPRINT",FACE,{"disambiguationData":[TD([[makeQuery(id+"F49.imprint","IMPRINT",EDGE,{"derivedFrom":subQ1}),1.0]])]});}
            extrude(context, id + "F50", {"entities" : qUnion([Q0, Q1, Q2]), "operationType" : NewBodyOperationType.REMOVE, "oppositeDirection" : true, "depth" : 0.76 * mm});
        }
        {
            var Q0;
            Q0=makeQuery(id+"F3.boolean.opBoolean","COPY",FACE,{"derivedFrom":makeQuery(id+"F3.opExtrude","CAP_FACE",FACE,{"disambiguationData":[OSD([sQuery(id+"F0.wireOp",EDGE,"E0.bottom"),sQuery(id+"F0.wireOp",EDGE,"E0.top"),sQuery(id+"F0.wireOp",EDGE,"E0.left"),sQuery(id+"F2.wireOp",EDGE,"E1.top"),sQuery(id+"F2.wireOp",EDGE,"E1.right"),sQuery(id+"F2.wireOp",EDGE,"E2.bottom"),sQuery(id+"F2.wireOp",EDGE,"E2.top"),sQuery(id+"F2.wireOp",EDGE,"E3.top"),sQuery(id+"F2.wireOp",EDGE,"E3.right"),sQuery(id+"F2.wireOp",EDGE,"E4.left"),sQuery(id+"F2.wireOp",EDGE,"E4.right"),sQuery(id+"F2.wireOp",EDGE,"E5.top"),sQuery(id+"F2.wireOp",EDGE,"E5.right"),sQuery(id+"F2.wireOp",EDGE,"E6.top"),sQuery(id+"F2.wireOp",EDGE,"E6.right"),sQuery(id+"F2.wireOp",EDGE,"E7.left"),sQuery(id+"F2.wireOp",EDGE,"E7.right"),sQuery(id+"F2.wireOp",EDGE,"E8.bottom"),sQuery(id+"F2.wireOp",EDGE,"E8.top"),sQuery(id+"F2.wireOp",EDGE,"E9"),sQuery(id+"F2.wireOp",EDGE,"E10"),sQuery(id+"F2.wireOp",EDGE,"E12.trimOffspring"),sQuery(id+"F2.wireOp",EDGE,"E13.trimOffspring"),sQuery(id+"F2.wireOp",EDGE,"E14.trimOffspring"),sQuery(id+"F2.wireOp",EDGE,"E15.trimOffspring"),sQuery(id+"F2.wireOp",EDGE,"E16.trimOffspring"),sQuery(id+"F2.wireOp",EDGE,"E17.trimOffspring"),sQuery(id+"F2.wireOp",EDGE,"E18.trimOffspring")])],"isStart":false})});
            var sketch = newSketch(context, id + "F51", { "sketchPlane" : qUnion([Q0])});
            skLineSegment(sketch, "E287", {"start": v(-69.85, 0) * mm, "end": v(-69.82, 1.27) * mm});
            skLineSegment(sketch, "E288", {"start": v(-69.82, 1.27) * mm, "end": v(-53.92, 1.27) * mm});
            skLineSegment(sketch, "E289", {"start": v(-53.92, -1.27) * mm, "end": v(-69.82, -1.27) * mm});
            skLineSegment(sketch, "E290", {"start": v(-69.82, -1.27) * mm, "end": v(-69.85, 0) * mm});
            skLineSegment(sketch, "E291", {"start": v(-39.37, -15.82) * mm, "end": v(-39.37, -31.72) * mm});
            skPoint(sketch, "E292.endSnap0", {"position": v(-38.1, -31.75) * mm});
            skLineSegment(sketch, "E293", {"start": v(-36.83, -31.72) * mm, "end": v(-36.83, -15.82) * mm});
            skArc(sketch, "E294", {"start": v(-39.37, -15.82) * mm, "mid": v(-38.1, -15.88) * mm, "end": v(-36.83, -15.82) * mm});
            skArc(sketch, "E295", {"start": v(-53.92, 1.27) * mm, "mid": v(-53.98, 0) * mm, "end": v(-53.92, -1.27) * mm});
            skLineSegment(sketch, "E296", {"start": v(-22.23, 0) * mm, "end": v(-22.28, 1.27) * mm});
            skLineSegment(sketch, "E297", {"start": v(-22.28, 1.27) * mm, "end": v(-6.38, 1.27) * mm});
            skLineSegment(sketch, "E298", {"start": v(-6.38, 1.27) * mm, "end": v(-6.38, -1.27) * mm});
            skLineSegment(sketch, "E299", {"start": v(-6.38, -1.27) * mm, "end": v(-22.28, -1.27) * mm});
            skLineSegment(sketch, "E300", {"start": v(-22.28, -1.27) * mm, "end": v(-22.23, 0) * mm});
            skLineSegment(sketch, "E301", {"start": v(-39.37, 31.72) * mm, "end": v(-39.37, 15.82) * mm});
            skLineSegment(sketch, "E302", {"start": v(-36.83, 15.82) * mm, "end": v(-36.83, 31.72) * mm});
            skArc(sketch, "E303", {"start": v(-36.83, 15.82) * mm, "mid": v(-38.1, 15.88) * mm, "end": v(-39.37, 15.82) * mm});
            skPoint(sketch, "E304.end.orphan", {"position": v(-38.1, 31.75) * mm});
            skArc(sketch, "E305", {"start": v(-39.37, 31.72) * mm, "mid": v(-38.1, 31.7) * mm, "end": v(-36.83, 31.72) * mm});
            skPoint(sketch, "E306.start.orphan", {"position": v(-38.1, -31.78) * mm});
            skArc(sketch, "E307", {"start": v(-36.83, -31.72) * mm, "mid": v(-38.1, -31.7) * mm, "end": v(-39.37, -31.72) * mm});
            skSolve(sketch);
        }
        {
            var Q0;
            Q0=makeQuery(id+"F51.imprint","IMPRINT",FACE,{"disambiguationData":[TD([[makeQuery(id+"F51.imprint","IMPRINT",EDGE,{"derivedFrom":sQuery(id+"F51.wireOp",EDGE,"E287")}),-1.0]])]});
            var Q1;
            Q1=makeQuery(id+"F51.imprint","IMPRINT",FACE,{"disambiguationData":[TD([[makeQuery(id+"F51.imprint","IMPRINT",EDGE,{"derivedFrom":sQuery(id+"F51.wireOp",EDGE,"E291")}),1.0]])]});
            var Q2;
            {var subQ4=sQuery(id+"F51.wireOp",EDGE,"E297");Q2=makeQuery(id+"F51.imprint","IMPRINT",FACE,{"disambiguationData":[TD([[makeQuery(id+"F51.imprint","IMPRINT",EDGE,{"derivedFrom":subQ4}),-1.0]])]});}
            var Q3;
            Q3=makeQuery(id+"F51.imprint","IMPRINT",FACE,{"disambiguationData":[TD([[makeQuery(id+"F51.imprint","IMPRINT",EDGE,{"derivedFrom":sQuery(id+"F51.wireOp",EDGE,"E301")}),1.0]])]});
            extrude(context, id + "F52", {"entities" : qUnion([Q0, Q1, Q2, Q3]), "operationType" : NewBodyOperationType.REMOVE, "oppositeDirection" : true, "depth" : 0.76 * mm});
        }
        {
            var Q0;
            Q0=makeQuery(id+"F5.boolean.opBoolean","COPY",FACE,{"derivedFrom":makeQuery(id+"F5.opExtrude","CAP_FACE",FACE,{"disambiguationData":[OSD([sQuery(id+"F0.wireOp",EDGE,"E0.bottom"),sQuery(id+"F0.wireOp",EDGE,"E0.top"),sQuery(id+"F0.wireOp",EDGE,"E0.right"),sQuery(id+"F4.wireOp",EDGE,"E19.right"),sQuery(id+"F4.wireOp",EDGE,"E21.right"),sQuery(id+"F4.wireOp",EDGE,"E22.left"),sQuery(id+"F4.wireOp",EDGE,"E22.right"),sQuery(id+"F4.wireOp",EDGE,"E23.right"),sQuery(id+"F4.wireOp",EDGE,"E24.top"),sQuery(id+"F4.wireOp",EDGE,"E24.right"),sQuery(id+"F4.wireOp",EDGE,"E25.left"),sQuery(id+"F4.wireOp",EDGE,"E25.right"),sQuery(id+"F4.wireOp",EDGE,"E26.bottom"),sQuery(id+"F4.wireOp",EDGE,"E26.top"),sQuery(id+"F4.wireOp",EDGE,"E27"),sQuery(id+"F4.wireOp",EDGE,"E28"),sQuery(id+"F4.wireOp",EDGE,"E32.trimOffspring"),sQuery(id+"F4.wireOp",EDGE,"E33.trimOffspring"),sQuery(id+"F4.wireOp",EDGE,"E34.trimOffspring"),sQuery(id+"F4.wireOp",EDGE,"E35.trimOffspring"),sQuery(id+"F4.wireOp",EDGE,"E36.trimOffspring"),sQuery(id+"F4.wireOp",EDGE,"E37.right"),sQuery(id+"F4.wireOp",EDGE,"E38.bottom"),sQuery(id+"F4.wireOp",EDGE,"E39.right"),sQuery(id+"F4.wireOp",EDGE,"E40.left"),sQuery(id+"F4.wireOp",EDGE,"E40.right"),sQuery(id+"F4.wireOp",EDGE,"E41.top"),sQuery(id+"F4.wireOp",EDGE,"E41.right"),sQuery(id+"F4.wireOp",EDGE,"E42.right"),sQuery(id+"F4.wireOp",EDGE,"E43.left"),sQuery(id+"F4.wireOp",EDGE,"E43.right"),sQuery(id+"F4.wireOp",EDGE,"E44.bottom"),sQuery(id+"F4.wireOp",EDGE,"E44.top"),sQuery(id+"F4.wireOp",EDGE,"E46"),sQuery(id+"F4.wireOp",EDGE,"E48.trimOffspring"),sQuery(id+"F4.wireOp",EDGE,"E49.trimOffspring"),sQuery(id+"F4.wireOp",EDGE,"E50.trimOffspring"),sQuery(id+"F4.wireOp",EDGE,"E52.trimOffspring"),sQuery(id+"F4.wireOp",EDGE,"E56"),sQuery(id+"F4.wireOp",EDGE,"E57"),sQuery(id+"F4.wireOp",EDGE,"E58"),sQuery(id+"F4.wireOp",EDGE,"E59"),sQuery(id+"F4.wireOp",EDGE,"E60"),sQuery(id+"F4.wireOp",EDGE,"E61")])],"isStart":false})});
            var sketch = newSketch(context, id + "F53", { "sketchPlane" : qUnion([Q0])});
            skLineSegment(sketch, "E308", {"start": v(0.2, 15.88) * mm, "end": v(1.46, 15.82) * mm});
            skLineSegment(sketch, "E309", {"start": v(1.46, 15.82) * mm, "end": v(1.46, 31.53) * mm});
            skLineSegment(sketch, "E310", {"start": v(-1.08, 31.53) * mm, "end": v(-1.08, 15.82) * mm});
            skLineSegment(sketch, "E311", {"start": v(-1.08, 15.82) * mm, "end": v(0.2, 15.88) * mm});
            skLineSegment(sketch, "E312", {"start": v(16.07, -0.1) * mm, "end": v(16.02, 1.17) * mm});
            skLineSegment(sketch, "E313", {"start": v(16.02, 1.17) * mm, "end": v(31.91, 1.17) * mm});
            skLineSegment(sketch, "E314", {"start": v(31.91, 1.17) * mm, "end": v(31.91, -1.36) * mm});
            skLineSegment(sketch, "E315", {"start": v(31.91, -1.36) * mm, "end": v(16.02, -1.36) * mm});
            skLineSegment(sketch, "E316", {"start": v(16.02, -1.36) * mm, "end": v(16.07, -0.1) * mm});
            skLineSegment(sketch, "E317", {"start": v(0, -16.06) * mm, "end": v(1.27, -16.03) * mm});
            skLineSegment(sketch, "E318", {"start": v(1.27, -16.03) * mm, "end": v(1.27, -31.6) * mm});
            skLineSegment(sketch, "E319", {"start": v(-1.27, -31.6) * mm, "end": v(-1.27, -16) * mm});
            skLineSegment(sketch, "E320", {"start": v(-1.27, -31.6) * mm, "end": v(1.27, -31.6) * mm});
            skPoint(sketch, "E321.orphan", {"position": v(1.27, -31.73) * mm});
            skLineSegment(sketch, "E322", {"start": v(-1.27, -16) * mm, "end": v(0, -16.06) * mm});
            skLineSegment(sketch, "E323", {"start": v(-15.68, -0.1) * mm, "end": v(-15.64, 1.17) * mm});
            skLineSegment(sketch, "E324", {"start": v(-15.64, 1.17) * mm, "end": v(-31.53, 1.17) * mm});
            skLineSegment(sketch, "E325", {"start": v(-31.53, 1.17) * mm, "end": v(-31.53, -1.36) * mm});
            skLineSegment(sketch, "E326", {"start": v(-31.53, -1.36) * mm, "end": v(-15.64, -1.36) * mm});
            skLineSegment(sketch, "E327", {"start": v(-15.64, -1.36) * mm, "end": v(-15.68, -0.1) * mm});
            skArc(sketch, "E328", {"start": v(-1.08, 31.53) * mm, "mid": v(0.2, 31.51) * mm, "end": v(1.46, 31.53) * mm});
            skSolve(sketch);
        }
        {
            var Q0;
            {var subQ4=sQuery(id+"F53.wireOp",EDGE,"E309");Q0=makeQuery(id+"F53.imprint","IMPRINT",FACE,{"disambiguationData":[TD([[makeQuery(id+"F53.imprint","IMPRINT",EDGE,{"derivedFrom":subQ4}),1.0]])]});}
            var Q1;
            {var subQ4=sQuery(id+"F53.wireOp",EDGE,"E318");Q1=makeQuery(id+"F53.imprint","IMPRINT",FACE,{"disambiguationData":[TD([[makeQuery(id+"F53.imprint","IMPRINT",EDGE,{"derivedFrom":subQ4}),-1.0]])]});}
            var Q2;
            {var subQ5=sQuery(id+"F53.wireOp",EDGE,"E313");Q2=makeQuery(id+"F53.imprint","IMPRINT",FACE,{"disambiguationData":[TD([[makeQuery(id+"F53.imprint","IMPRINT",EDGE,{"derivedFrom":subQ5}),-1.0]])]});}
            var Q3;
            {var subQ5=sQuery(id+"F53.wireOp",EDGE,"E324");Q3=makeQuery(id+"F53.imprint","IMPRINT",FACE,{"disambiguationData":[TD([[makeQuery(id+"F53.imprint","IMPRINT",EDGE,{"derivedFrom":subQ5}),1.0]])]});}
            extrude(context, id + "F54", {"entities" : qUnion([Q0, Q1, Q2, Q3]), "operationType" : NewBodyOperationType.REMOVE, "oppositeDirection" : true, "depth" : 0.76 * mm});
        }
        {
            var Q0;
            Q0=makeQuery(id+"F17.boolean.opBoolean","MERGE",FACE,{"derivedFrom":[makeQuery(id+"F15.boolean.opBoolean","MERGE",FACE,{"derivedFrom":[makeQuery(id+"F7.boolean.opBoolean","COPY",FACE,{"derivedFrom":makeQuery(id+"F7.opExtrude","CAP_FACE",FACE,{"disambiguationData":[OSD([sQuery(id+"F0.wireOp",EDGE,"E0.bottom"),sQuery(id+"F0.wireOp",EDGE,"E0.top"),sQuery(id+"F0.wireOp",EDGE,"E0.right"),sQuery(id+"F6.wireOp",EDGE,"E63.right"),sQuery(id+"F6.wireOp",EDGE,"E65.right"),sQuery(id+"F6.wireOp",EDGE,"E66.left"),sQuery(id+"F6.wireOp",EDGE,"E66.right"),sQuery(id+"F6.wireOp",EDGE,"E67.right"),sQuery(id+"F6.wireOp",EDGE,"E68.top"),sQuery(id+"F6.wireOp",EDGE,"E68.right"),sQuery(id+"F6.wireOp",EDGE,"E69.left"),sQuery(id+"F6.wireOp",EDGE,"E69.right"),sQuery(id+"F6.wireOp",EDGE,"E70.bottom"),sQuery(id+"F6.wireOp",EDGE,"E70.top"),sQuery(id+"F6.wireOp",EDGE,"E71"),sQuery(id+"F6.wireOp",EDGE,"E72"),sQuery(id+"F6.wireOp",EDGE,"E76.trimOffspring"),sQuery(id+"F6.wireOp",EDGE,"E77.trimOffspring"),sQuery(id+"F6.wireOp",EDGE,"E78.trimOffspring"),sQuery(id+"F6.wireOp",EDGE,"E79.trimOffspring"),sQuery(id+"F6.wireOp",EDGE,"E80.trimOffspring"),sQuery(id+"F6.wireOp",EDGE,"E81.right"),sQuery(id+"F6.wireOp",EDGE,"E82.bottom"),sQuery(id+"F6.wireOp",EDGE,"E83.right"),sQuery(id+"F6.wireOp",EDGE,"E84.left"),sQuery(id+"F6.wireOp",EDGE,"E84.right"),sQuery(id+"F6.wireOp",EDGE,"E85.top"),sQuery(id+"F6.wireOp",EDGE,"E85.right"),sQuery(id+"F6.wireOp",EDGE,"E86.right"),sQuery(id+"F6.wireOp",EDGE,"E87.left"),sQuery(id+"F6.wireOp",EDGE,"E87.right"),sQuery(id+"F6.wireOp",EDGE,"E88.bottom"),sQuery(id+"F6.wireOp",EDGE,"E88.top"),sQuery(id+"F6.wireOp",EDGE,"E90"),sQuery(id+"F6.wireOp",EDGE,"E92.trimOffspring"),sQuery(id+"F6.wireOp",EDGE,"E93.trimOffspring"),sQuery(id+"F6.wireOp",EDGE,"E94.trimOffspring"),sQuery(id+"F6.wireOp",EDGE,"E96.trimOffspring"),sQuery(id+"F6.wireOp",EDGE,"E100"),sQuery(id+"F6.wireOp",EDGE,"E101"),sQuery(id+"F6.wireOp",EDGE,"E102"),sQuery(id+"F6.wireOp",EDGE,"E103"),sQuery(id+"F6.wireOp",EDGE,"E104"),sQuery(id+"F6.wireOp",EDGE,"E105")])],"isStart":false})}),makeQuery(id+"F15.opExtrude","SWEPT_FACE",FACE,{"disambiguationData":[OSD([sQuery(id+"F14.wireOp",EDGE,"E154")])]})]}),makeQuery(id+"F17.opExtrude","SWEPT_FACE",FACE,{"disambiguationData":[OSD([sQuery(id+"F16.wireOp",EDGE,"E157")])]})]});
            var sketch = newSketch(context, id + "F55", { "sketchPlane" : qUnion([Q0])});
            skLineSegment(sketch, "E329", {"start": v(7.11, 1.17) * mm, "end": v(22.47, 1.17) * mm});
            skLineSegment(sketch, "E330", {"start": v(7.11, -1.36) * mm, "end": v(7.11, 1.17) * mm});
            skLineSegment(sketch, "E331", {"start": v(7.11, -1.36) * mm, "end": v(22.48, -1.36) * mm});
            skArc(sketch, "E332", {"start": v(22.47, 1.17) * mm, "mid": v(22.38, -0.1) * mm, "end": v(22.48, -1.36) * mm});
            skLineSegment(sketch, "E333", {"start": v(38.3, -15.99) * mm, "end": v(39.58, -15.94) * mm});
            skLineSegment(sketch, "E334", {"start": v(39.58, -15.94) * mm, "end": v(39.58, -31.64) * mm});
            skLineSegment(sketch, "E335", {"start": v(39.58, -31.64) * mm, "end": v(37.04, -31.64) * mm});
            skLineSegment(sketch, "E336", {"start": v(37.04, -31.64) * mm, "end": v(37.04, -15.94) * mm});
            skLineSegment(sketch, "E337", {"start": v(37.04, -15.94) * mm, "end": v(38.3, -15.99) * mm});
            skLineSegment(sketch, "E338", {"start": v(69.34, 0) * mm, "end": v(69.34, 1.27) * mm});
            skLineSegment(sketch, "E339", {"start": v(69.34, 1.27) * mm, "end": v(54.14, 1.27) * mm});
            skLineSegment(sketch, "E340", {"start": v(54.18, -1.27) * mm, "end": v(69.34, -1.27) * mm});
            skLineSegment(sketch, "E341", {"start": v(69.34, -1.27) * mm, "end": v(69.34, 0) * mm});
            skArc(sketch, "E342", {"start": v(54.18, -1.27) * mm, "mid": v(54.2, 0) * mm, "end": v(54.14, 1.27) * mm});
            skLineSegment(sketch, "E343", {"start": v(38.3, 15.95) * mm, "end": v(39.58, 15.9) * mm});
            skLineSegment(sketch, "E344", {"start": v(39.58, 15.9) * mm, "end": v(39.58, 31.61) * mm});
            skLineSegment(sketch, "E345", {"start": v(39.58, 31.61) * mm, "end": v(37.04, 31.61) * mm});
            skLineSegment(sketch, "E346", {"start": v(37.04, 31.61) * mm, "end": v(37.04, 15.9) * mm});
            skLineSegment(sketch, "E347", {"start": v(37.04, 15.9) * mm, "end": v(38.3, 15.95) * mm});
            skSolve(sketch);
        }
        {
            var Q0;
            Q0=makeQuery(id+"F55.imprint","IMPRINT",FACE,{"disambiguationData":[TD([[makeQuery(id+"F55.imprint","IMPRINT",EDGE,{"derivedFrom":sQuery(id+"F55.wireOp",EDGE,"E329")}),-1.0]])]});
            var Q1;
            {var subQ5=sQuery(id+"F55.wireOp",EDGE,"E334");Q1=makeQuery(id+"F55.imprint","IMPRINT",FACE,{"disambiguationData":[TD([[makeQuery(id+"F55.imprint","IMPRINT",EDGE,{"derivedFrom":subQ5}),-1.0]])]});}
            var Q2;
            Q2=makeQuery(id+"F55.imprint","IMPRINT",FACE,{"disambiguationData":[TD([[makeQuery(id+"F55.imprint","IMPRINT",EDGE,{"derivedFrom":sQuery(id+"F55.wireOp",EDGE,"E338")}),1.0]])]});
            var Q3;
            {var subQ5=sQuery(id+"F55.wireOp",EDGE,"E344");Q3=makeQuery(id+"F55.imprint","IMPRINT",FACE,{"disambiguationData":[TD([[makeQuery(id+"F55.imprint","IMPRINT",EDGE,{"derivedFrom":subQ5}),1.0]])]});}
            extrude(context, id + "F56", {"entities" : qUnion([Q0, Q1, Q2, Q3]), "operationType" : NewBodyOperationType.REMOVE, "oppositeDirection" : true, "depth" : 0.76 * mm});
        }
        {
            var Q0;
            Q0=makeQuery(id+"F31.boolean.opBoolean","MERGE",FACE,{"derivedFrom":[makeQuery(id+"F29.boolean.opBoolean","MERGE",FACE,{"derivedFrom":[makeQuery(id+"F27.boolean.opBoolean","MERGE",FACE,{"derivedFrom":[makeQuery(id+"F25.boolean.opBoolean","COPY",FACE,{"derivedFrom":makeQuery(id+"F25.opExtrude","CAP_FACE",FACE,{"disambiguationData":[OSD([sQuery(id+"F0.wireOp",EDGE,"E0.bottom"),sQuery(id+"F0.wireOp",EDGE,"E0.left"),sQuery(id+"F0.wireOp",EDGE,"E0.right"),sQuery(id+"F2.wireOp",EDGE,"E5.bottom"),sQuery(id+"F2.wireOp",EDGE,"E5.right"),sQuery(id+"F4.wireOp",EDGE,"E22.bottom"),sQuery(id+"F4.wireOp",EDGE,"E22.right"),sQuery(id+"F6.wireOp",EDGE,"E66.left"),sQuery(id+"F6.wireOp",EDGE,"E67.right"),sQuery(id+"F24.wireOp",EDGE,"E201"),sQuery(id+"F24.wireOp",EDGE,"E202"),sQuery(id+"F24.wireOp",EDGE,"E203"),sQuery(id+"F24.wireOp",EDGE,"E204"),sQuery(id+"F24.wireOp",EDGE,"E205"),sQuery(id+"F24.wireOp",EDGE,"E206"),sQuery(id+"F24.wireOp",EDGE,"E207"),sQuery(id+"F24.wireOp",EDGE,"E208"),sQuery(id+"F24.wireOp",EDGE,"E209"),sQuery(id+"F24.wireOp",EDGE,"E210"),sQuery(id+"F24.wireOp",EDGE,"E211"),sQuery(id+"F24.wireOp",EDGE,"E212"),sQuery(id+"F24.wireOp",EDGE,"E213"),sQuery(id+"F24.wireOp",EDGE,"E214"),sQuery(id+"F24.wireOp",EDGE,"E215"),sQuery(id+"F24.wireOp",EDGE,"E216"),sQuery(id+"F24.wireOp",EDGE,"E217"),sQuery(id+"F24.wireOp",EDGE,"E218"),sQuery(id+"F24.wireOp",EDGE,"E219"),sQuery(id+"F24.wireOp",EDGE,"E220"),sQuery(id+"F24.wireOp",EDGE,"E221"),sQuery(id+"F24.wireOp",EDGE,"E222"),sQuery(id+"F24.wireOp",EDGE,"E223"),sQuery(id+"F24.wireOp",EDGE,"E224"),sQuery(id+"F24.wireOp",EDGE,"E225"),sQuery(id+"F24.wireOp",EDGE,"E226"),sQuery(id+"F24.wireOp",EDGE,"E227.trimOffspring"),sQuery(id+"F24.wireOp",EDGE,"E228.trimOffspring"),sQuery(id+"F24.wireOp",EDGE,"E229.trimOffspring"),sQuery(id+"F24.wireOp",EDGE,"E230.trimOffspring"),sQuery(id+"F24.wireOp",EDGE,"E231.trimOffspring"),sQuery(id+"F24.wireOp",EDGE,"E232.trimOffspring"),sQuery(id+"F24.wireOp",EDGE,"E233.trimOffspring")])],"isStart":false})}),makeQuery(id+"F27.opExtrude","SWEPT_FACE",FACE,{"disambiguationData":[OSD([sQuery(id+"F26.wireOp",EDGE,"E236")])]})]}),makeQuery(id+"F29.opExtrude","SWEPT_FACE",FACE,{"disambiguationData":[OSD([sQuery(id+"F28.wireOp",EDGE,"E240")])]})]}),makeQuery(id+"F31.opExtrude","SWEPT_FACE",FACE,{"disambiguationData":[OSD([sQuery(id+"F30.wireOp",EDGE,"E246")])]})]});
            var sketch = newSketch(context, id + "F57", { "sketchPlane" : qUnion([Q0])});
            skLineSegment(sketch, "E348", {"start": v(0, -22.43) * mm, "end": v(1.27, -22.48) * mm});
            skLineSegment(sketch, "E349", {"start": v(1.27, -22.48) * mm, "end": v(1.27, -6.58) * mm});
            skLineSegment(sketch, "E350", {"start": v(1.27, -6.58) * mm, "end": v(-1.27, -6.58) * mm});
            skLineSegment(sketch, "E351", {"start": v(-1.27, -6.58) * mm, "end": v(-1.27, -22.48) * mm});
            skLineSegment(sketch, "E352", {"start": v(-1.27, -22.48) * mm, "end": v(0, -22.43) * mm});
            skLineSegment(sketch, "E353", {"start": v(0, -38.3) * mm, "end": v(31.75, -38.3) * mm, "construction": true});
            skLineSegment(sketch, "E354", {"start": v(31.72, -37.04) * mm, "end": v(15.82, -37.04) * mm});
            skLineSegment(sketch, "E355", {"start": v(15.82, -37.04) * mm, "end": v(15.82, -39.58) * mm});
            skLineSegment(sketch, "E356", {"start": v(15.82, -39.58) * mm, "end": v(31.72, -39.58) * mm});
            skLineSegment(sketch, "E357", {"start": v(-15.87, -38.3) * mm, "end": v(-15.82, -37.04) * mm});
            skLineSegment(sketch, "E358", {"start": v(-15.82, -37.04) * mm, "end": v(-31.72, -37.04) * mm});
            skLineSegment(sketch, "E359", {"start": v(-31.72, -37.04) * mm, "end": v(-31.72, -39.58) * mm});
            skLineSegment(sketch, "E360", {"start": v(-31.72, -39.58) * mm, "end": v(-15.82, -39.58) * mm});
            skLineSegment(sketch, "E361", {"start": v(-15.82, -39.58) * mm, "end": v(-15.88, -38.3) * mm});
            skLineSegment(sketch, "E362", {"start": v(0, -54.18) * mm, "end": v(1.27, -54.13) * mm});
            skLineSegment(sketch, "E363", {"start": v(1.27, -54.13) * mm, "end": v(1.27, -70.03) * mm});
            skLineSegment(sketch, "E364", {"start": v(1.27, -70.03) * mm, "end": v(-1.27, -70.03) * mm});
            skLineSegment(sketch, "E365", {"start": v(-1.27, -70.03) * mm, "end": v(-1.27, -54.13) * mm});
            skLineSegment(sketch, "E366", {"start": v(-1.27, -54.13) * mm, "end": v(0, -54.18) * mm});
            skArc(sketch, "E367", {"start": v(31.72, -37.04) * mm, "mid": v(31.68, -38.3) * mm, "end": v(31.72, -39.58) * mm});
            skSolve(sketch);
        }
        {
            var Q0;
            {var subQ4=sQuery(id+"F57.wireOp",EDGE,"E358");Q0=makeQuery(id+"F57.imprint","IMPRINT",FACE,{"disambiguationData":[TD([[makeQuery(id+"F57.imprint","IMPRINT",EDGE,{"derivedFrom":subQ4}),1.0]])]});}
            var Q1;
            {var subQ4=sQuery(id+"F57.wireOp",EDGE,"E363");Q1=makeQuery(id+"F57.imprint","IMPRINT",FACE,{"disambiguationData":[TD([[makeQuery(id+"F57.imprint","IMPRINT",EDGE,{"derivedFrom":subQ4}),-1.0]])]});}
            var Q2;
            {var subQ0=sQuery(id+"F57.wireOp",EDGE,"E354");Q2=makeQuery(id+"F57.imprint","IMPRINT",FACE,{"disambiguationData":[TD([[makeQuery(id+"F57.imprint","IMPRINT",EDGE,{"derivedFrom":subQ0}),1.0]])]});}
            var Q3;
            {var subQ4=sQuery(id+"F57.wireOp",EDGE,"E349");Q3=makeQuery(id+"F57.imprint","IMPRINT",FACE,{"disambiguationData":[TD([[makeQuery(id+"F57.imprint","IMPRINT",EDGE,{"derivedFrom":subQ4}),1.0]])]});}
            extrude(context, id + "F58", {"entities" : qUnion([Q0, Q1, Q2, Q3]), "operationType" : NewBodyOperationType.REMOVE, "oppositeDirection" : true, "depth" : 0.76 * mm});
        }
        {
            var Q0;
            Q0=makeQuery(id+"F7.boolean.opBoolean","COPY",EDGE,{"derivedFrom":makeQuery(id+"F7.opExtrude","CAP_EDGE",EDGE,{"disambiguationData":[OSD([sQuery(id+"F6.wireOp",EDGE,"E94.trimOffspring")])],"isStart":false})});
            var Q1;
            {var subQ0=sQuery(id+"F6.wireOp",EDGE,"E76.trimOffspring");Q1=makeQuery(id+"F7.boolean.opBoolean","COPY",EDGE,{"derivedFrom":makeQuery(id+"F7.opExtrude","CAP_EDGE",EDGE,{"disambiguationData":[OSD([subQ0]),TDD([makeQuery(id+"F6.imprint","IMPRINT",EDGE,{"disambiguationData":[TD([[makeQuery(id+"F6.imprint","INTERSECT",VERTEX,{"derivedFrom":[subQ0,sQuery(id+"F6.wireOp",EDGE,"E103")]}),1.0]])],"derivedFrom":subQ0})])],"isStart":false})});}
            var Q2;
            {var subQ0=sQuery(id+"F4.wireOp",EDGE,"E52.trimOffspring");var subQ1=sQuery(id+"F4.wireOp",EDGE,"E44.bottom");var subQ3=makeQuery(id+"F4.imprint","IMPRINT",EDGE,{"disambiguationData":[TD([[makeQuery(id+"F4.imprint","INTERSECT",VERTEX,{"derivedFrom":[subQ1,subQ0]}),1.0]])],"derivedFrom":subQ0});Q2=makeQuery(id+"F54.boolean.opBoolean","SPLIT",EDGE,{"disambiguationData":[TD([makeQuery(id+"F5.boolean.opBoolean","COPY",FACE,{"derivedFrom":makeQuery(id+"F5.opExtrude","SWEPT_FACE",FACE,{"disambiguationData":[OSD([subQ1])]})})])],"derivedFrom":makeQuery(id+"F5.boolean.opBoolean","COPY",EDGE,{"derivedFrom":makeQuery(id+"F5.opExtrude","CAP_EDGE",EDGE,{"disambiguationData":[OSD([subQ0]),TDD([subQ3])],"isStart":false})})});}
            var Q3;
            {var subQ0=sQuery(id+"F4.wireOp",EDGE,"E34.trimOffspring");var subQ1=sQuery(id+"F4.wireOp",EDGE,"E26.top");var subQ3=makeQuery(id+"F4.imprint","IMPRINT",EDGE,{"disambiguationData":[TD([[makeQuery(id+"F4.imprint","INTERSECT",VERTEX,{"derivedFrom":[subQ1,subQ0]}),-1.0]])],"derivedFrom":subQ0});Q3=makeQuery(id+"F54.boolean.opBoolean","SPLIT",EDGE,{"disambiguationData":[TD([makeQuery(id+"F5.boolean.opBoolean","COPY",FACE,{"derivedFrom":makeQuery(id+"F5.opExtrude","SWEPT_FACE",FACE,{"disambiguationData":[OSD([subQ1])]})})])],"derivedFrom":makeQuery(id+"F5.boolean.opBoolean","COPY",EDGE,{"derivedFrom":makeQuery(id+"F5.opExtrude","CAP_EDGE",EDGE,{"disambiguationData":[OSD([subQ0]),TDD([subQ3])],"isStart":false})})});}
            var Q4;
            {var subQ0=sQuery(id+"F4.wireOp",EDGE,"E50.trimOffspring");var subQ1=sQuery(id+"F4.wireOp",EDGE,"E38.bottom");Q4=makeQuery(id+"F54.boolean.opBoolean","SPLIT",EDGE,{"disambiguationData":[TD([makeQuery(id+"F5.boolean.opBoolean","COPY",FACE,{"derivedFrom":makeQuery(id+"F5.opExtrude","SWEPT_FACE",FACE,{"disambiguationData":[OSD([subQ1])]})})])],"derivedFrom":makeQuery(id+"F5.boolean.opBoolean","COPY",EDGE,{"derivedFrom":makeQuery(id+"F5.opExtrude","CAP_EDGE",EDGE,{"disambiguationData":[OSD([subQ0])],"isStart":false})})});}
            var Q5;
            {var subQ0=sQuery(id+"F4.wireOp",EDGE,"E59");var subQ1=sQuery(id+"F4.wireOp",EDGE,"E32.trimOffspring");var subQ3=makeQuery(id+"F4.imprint","IMPRINT",EDGE,{"disambiguationData":[TD([[makeQuery(id+"F4.imprint","INTERSECT",VERTEX,{"derivedFrom":[subQ1,subQ0]}),1.0]])],"derivedFrom":subQ1});Q5=makeQuery(id+"F54.boolean.opBoolean","SPLIT",EDGE,{"disambiguationData":[TD([makeQuery(id+"F3.boolean.opBoolean","COPY",FACE,{"derivedFrom":makeQuery(id+"F3.opExtrude","SWEPT_FACE",FACE,{"disambiguationData":[OSD([sQuery(id+"F2.wireOp",EDGE,"E8.top")])]})})])],"derivedFrom":makeQuery(id+"F5.boolean.opBoolean","COPY",EDGE,{"derivedFrom":makeQuery(id+"F5.opExtrude","CAP_EDGE",EDGE,{"disambiguationData":[OSD([subQ1]),TDD([subQ3])],"isStart":false})})});}
            var Q6;
            {var subQ0=sQuery(id+"F2.wireOp",EDGE,"E16.trimOffspring");var subQ1=sQuery(id+"F2.wireOp",EDGE,"E8.bottom");Q6=makeQuery(id+"F52.boolean.opBoolean","SPLIT",EDGE,{"disambiguationData":[TD([makeQuery(id+"F3.boolean.opBoolean","COPY",FACE,{"derivedFrom":makeQuery(id+"F3.opExtrude","CAP_FACE",FACE,{"disambiguationData":[OSD([sQuery(id+"F0.wireOp",EDGE,"E0.bottom"),sQuery(id+"F0.wireOp",EDGE,"E0.top"),sQuery(id+"F0.wireOp",EDGE,"E0.left"),sQuery(id+"F2.wireOp",EDGE,"E1.top"),sQuery(id+"F2.wireOp",EDGE,"E1.right"),sQuery(id+"F2.wireOp",EDGE,"E2.bottom"),sQuery(id+"F2.wireOp",EDGE,"E2.top"),sQuery(id+"F2.wireOp",EDGE,"E3.top"),sQuery(id+"F2.wireOp",EDGE,"E3.right"),sQuery(id+"F2.wireOp",EDGE,"E4.left"),sQuery(id+"F2.wireOp",EDGE,"E4.right"),sQuery(id+"F2.wireOp",EDGE,"E5.top"),sQuery(id+"F2.wireOp",EDGE,"E5.right"),sQuery(id+"F2.wireOp",EDGE,"E6.top"),sQuery(id+"F2.wireOp",EDGE,"E6.right"),sQuery(id+"F2.wireOp",EDGE,"E7.left"),sQuery(id+"F2.wireOp",EDGE,"E7.right"),subQ1,sQuery(id+"F2.wireOp",EDGE,"E8.top"),sQuery(id+"F2.wireOp",EDGE,"E9"),sQuery(id+"F2.wireOp",EDGE,"E10"),sQuery(id+"F2.wireOp",EDGE,"E12.trimOffspring"),sQuery(id+"F2.wireOp",EDGE,"E13.trimOffspring"),sQuery(id+"F2.wireOp",EDGE,"E14.trimOffspring"),sQuery(id+"F2.wireOp",EDGE,"E15.trimOffspring"),subQ0,sQuery(id+"F2.wireOp",EDGE,"E17.trimOffspring"),sQuery(id+"F2.wireOp",EDGE,"E18.trimOffspring")])],"isStart":false})}),makeQuery(id+"F3.boolean.opBoolean","COPY",FACE,{"derivedFrom":makeQuery(id+"F3.opExtrude","SWEPT_FACE",FACE,{"disambiguationData":[OSD([subQ1])]})}),makeQuery(id+"F3.boolean.opBoolean","COPY",FACE,{"derivedFrom":makeQuery(id+"F3.opExtrude","SWEPT_FACE",FACE,{"disambiguationData":[OSD([subQ0])]})}),makeQuery(id+"F5.opExtrude","SWEPT_FACE",FACE,{"disambiguationData":[OSD([sQuery(id+"F4.wireOp",EDGE,"E56")])]}),makeQuery(id+"F52.opExtrude","SWEPT_FACE",FACE,{"disambiguationData":[OSD([sQuery(id+"F51.wireOp",EDGE,"E297")])]}),makeQuery(id+"F52.opExtrude","SWEPT_FACE",FACE,{"disambiguationData":[OSD([sQuery(id+"F51.wireOp",EDGE,"E298")])]})])],"derivedFrom":makeQuery(id+"F3.boolean.opBoolean","COPY",EDGE,{"derivedFrom":makeQuery(id+"F3.opExtrude","CAP_EDGE",EDGE,{"disambiguationData":[OSD([subQ0])],"isStart":false})})});}
            var Q7;
            {var subQ0=sQuery(id+"F2.wireOp",EDGE,"E16.trimOffspring");var subQ1=sQuery(id+"F2.wireOp",EDGE,"E8.top");Q7=makeQuery(id+"F52.boolean.opBoolean","SPLIT",EDGE,{"disambiguationData":[TD([makeQuery(id+"F3.boolean.opBoolean","COPY",FACE,{"derivedFrom":makeQuery(id+"F3.opExtrude","CAP_FACE",FACE,{"disambiguationData":[OSD([sQuery(id+"F0.wireOp",EDGE,"E0.bottom"),sQuery(id+"F0.wireOp",EDGE,"E0.top"),sQuery(id+"F0.wireOp",EDGE,"E0.left"),sQuery(id+"F2.wireOp",EDGE,"E1.top"),sQuery(id+"F2.wireOp",EDGE,"E1.right"),sQuery(id+"F2.wireOp",EDGE,"E2.bottom"),sQuery(id+"F2.wireOp",EDGE,"E2.top"),sQuery(id+"F2.wireOp",EDGE,"E3.top"),sQuery(id+"F2.wireOp",EDGE,"E3.right"),sQuery(id+"F2.wireOp",EDGE,"E4.left"),sQuery(id+"F2.wireOp",EDGE,"E4.right"),sQuery(id+"F2.wireOp",EDGE,"E5.top"),sQuery(id+"F2.wireOp",EDGE,"E5.right"),sQuery(id+"F2.wireOp",EDGE,"E6.top"),sQuery(id+"F2.wireOp",EDGE,"E6.right"),sQuery(id+"F2.wireOp",EDGE,"E7.left"),sQuery(id+"F2.wireOp",EDGE,"E7.right"),sQuery(id+"F2.wireOp",EDGE,"E8.bottom"),subQ1,sQuery(id+"F2.wireOp",EDGE,"E9"),sQuery(id+"F2.wireOp",EDGE,"E10"),sQuery(id+"F2.wireOp",EDGE,"E12.trimOffspring"),sQuery(id+"F2.wireOp",EDGE,"E13.trimOffspring"),sQuery(id+"F2.wireOp",EDGE,"E14.trimOffspring"),sQuery(id+"F2.wireOp",EDGE,"E15.trimOffspring"),subQ0,sQuery(id+"F2.wireOp",EDGE,"E17.trimOffspring"),sQuery(id+"F2.wireOp",EDGE,"E18.trimOffspring")])],"isStart":false})}),makeQuery(id+"F3.boolean.opBoolean","COPY",FACE,{"derivedFrom":makeQuery(id+"F3.opExtrude","SWEPT_FACE",FACE,{"disambiguationData":[OSD([subQ1])]})}),makeQuery(id+"F3.boolean.opBoolean","COPY",FACE,{"derivedFrom":makeQuery(id+"F3.opExtrude","SWEPT_FACE",FACE,{"disambiguationData":[OSD([subQ0])]})}),makeQuery(id+"F5.opExtrude","SWEPT_FACE",FACE,{"disambiguationData":[OSD([sQuery(id+"F4.wireOp",EDGE,"E59")])]}),makeQuery(id+"F52.opExtrude","SWEPT_FACE",FACE,{"disambiguationData":[OSD([sQuery(id+"F51.wireOp",EDGE,"E298")])]}),makeQuery(id+"F52.opExtrude","SWEPT_FACE",FACE,{"disambiguationData":[OSD([sQuery(id+"F51.wireOp",EDGE,"E299")])]})])],"derivedFrom":makeQuery(id+"F3.boolean.opBoolean","COPY",EDGE,{"derivedFrom":makeQuery(id+"F3.opExtrude","CAP_EDGE",EDGE,{"disambiguationData":[OSD([subQ0])],"isStart":false})})});}
            var Q8;
            {var subQ0=sQuery(id+"F2.wireOp",EDGE,"E14.trimOffspring");var subQ1=sQuery(id+"F2.wireOp",EDGE,"E2.top");Q8=makeQuery(id+"F52.boolean.opBoolean","SPLIT",EDGE,{"disambiguationData":[TD([makeQuery(id+"F3.boolean.opBoolean","COPY",FACE,{"derivedFrom":makeQuery(id+"F3.opExtrude","CAP_FACE",FACE,{"disambiguationData":[OSD([sQuery(id+"F0.wireOp",EDGE,"E0.bottom"),sQuery(id+"F0.wireOp",EDGE,"E0.top"),sQuery(id+"F0.wireOp",EDGE,"E0.left"),sQuery(id+"F2.wireOp",EDGE,"E1.top"),sQuery(id+"F2.wireOp",EDGE,"E1.right"),sQuery(id+"F2.wireOp",EDGE,"E2.bottom"),subQ1,sQuery(id+"F2.wireOp",EDGE,"E3.top"),sQuery(id+"F2.wireOp",EDGE,"E3.right"),sQuery(id+"F2.wireOp",EDGE,"E4.left"),sQuery(id+"F2.wireOp",EDGE,"E4.right"),sQuery(id+"F2.wireOp",EDGE,"E5.top"),sQuery(id+"F2.wireOp",EDGE,"E5.right"),sQuery(id+"F2.wireOp",EDGE,"E6.top"),sQuery(id+"F2.wireOp",EDGE,"E6.right"),sQuery(id+"F2.wireOp",EDGE,"E7.left"),sQuery(id+"F2.wireOp",EDGE,"E7.right"),sQuery(id+"F2.wireOp",EDGE,"E8.bottom"),sQuery(id+"F2.wireOp",EDGE,"E8.top"),sQuery(id+"F2.wireOp",EDGE,"E9"),sQuery(id+"F2.wireOp",EDGE,"E10"),sQuery(id+"F2.wireOp",EDGE,"E12.trimOffspring"),sQuery(id+"F2.wireOp",EDGE,"E13.trimOffspring"),subQ0,sQuery(id+"F2.wireOp",EDGE,"E15.trimOffspring"),sQuery(id+"F2.wireOp",EDGE,"E16.trimOffspring"),sQuery(id+"F2.wireOp",EDGE,"E17.trimOffspring"),sQuery(id+"F2.wireOp",EDGE,"E18.trimOffspring")])],"isStart":false})}),makeQuery(id+"F3.boolean.opBoolean","COPY",FACE,{"derivedFrom":makeQuery(id+"F3.opExtrude","SWEPT_FACE",FACE,{"disambiguationData":[OSD([subQ1])]})}),makeQuery(id+"F3.boolean.opBoolean","COPY",FACE,{"derivedFrom":makeQuery(id+"F3.opExtrude","SWEPT_FACE",FACE,{"disambiguationData":[OSD([subQ0])]})}),makeQuery(id+"F52.opExtrude","SWEPT_FACE",FACE,{"disambiguationData":[OSD([sQuery(id+"F51.wireOp",EDGE,"E289")])]}),makeQuery(id+"F52.opExtrude","SWEPT_FACE",FACE,{"disambiguationData":[OSD([sQuery(id+"F51.wireOp",EDGE,"E290")])]})])],"derivedFrom":makeQuery(id+"F3.boolean.opBoolean","COPY",EDGE,{"derivedFrom":makeQuery(id+"F3.opExtrude","CAP_EDGE",EDGE,{"disambiguationData":[OSD([subQ0])],"isStart":false})})});}
            var Q9;
            {var subQ0=sQuery(id+"F2.wireOp",EDGE,"E2.bottom");var subQ1=sQuery(id+"F2.wireOp",EDGE,"E14.trimOffspring");Q9=makeQuery(id+"F52.boolean.opBoolean","SPLIT",EDGE,{"disambiguationData":[TD([makeQuery(id+"F3.boolean.opBoolean","COPY",FACE,{"derivedFrom":makeQuery(id+"F3.opExtrude","CAP_FACE",FACE,{"disambiguationData":[OSD([sQuery(id+"F0.wireOp",EDGE,"E0.bottom"),sQuery(id+"F0.wireOp",EDGE,"E0.top"),sQuery(id+"F0.wireOp",EDGE,"E0.left"),sQuery(id+"F2.wireOp",EDGE,"E1.top"),sQuery(id+"F2.wireOp",EDGE,"E1.right"),subQ0,sQuery(id+"F2.wireOp",EDGE,"E2.top"),sQuery(id+"F2.wireOp",EDGE,"E3.top"),sQuery(id+"F2.wireOp",EDGE,"E3.right"),sQuery(id+"F2.wireOp",EDGE,"E4.left"),sQuery(id+"F2.wireOp",EDGE,"E4.right"),sQuery(id+"F2.wireOp",EDGE,"E5.top"),sQuery(id+"F2.wireOp",EDGE,"E5.right"),sQuery(id+"F2.wireOp",EDGE,"E6.top"),sQuery(id+"F2.wireOp",EDGE,"E6.right"),sQuery(id+"F2.wireOp",EDGE,"E7.left"),sQuery(id+"F2.wireOp",EDGE,"E7.right"),sQuery(id+"F2.wireOp",EDGE,"E8.bottom"),sQuery(id+"F2.wireOp",EDGE,"E8.top"),sQuery(id+"F2.wireOp",EDGE,"E9"),sQuery(id+"F2.wireOp",EDGE,"E10"),sQuery(id+"F2.wireOp",EDGE,"E12.trimOffspring"),sQuery(id+"F2.wireOp",EDGE,"E13.trimOffspring"),subQ1,sQuery(id+"F2.wireOp",EDGE,"E15.trimOffspring"),sQuery(id+"F2.wireOp",EDGE,"E16.trimOffspring"),sQuery(id+"F2.wireOp",EDGE,"E17.trimOffspring"),sQuery(id+"F2.wireOp",EDGE,"E18.trimOffspring")])],"isStart":false})}),makeQuery(id+"F3.boolean.opBoolean","COPY",FACE,{"derivedFrom":makeQuery(id+"F3.opExtrude","SWEPT_FACE",FACE,{"disambiguationData":[OSD([subQ0])]})}),makeQuery(id+"F3.boolean.opBoolean","COPY",FACE,{"derivedFrom":makeQuery(id+"F3.opExtrude","SWEPT_FACE",FACE,{"disambiguationData":[OSD([subQ1])]})}),makeQuery(id+"F50.boolean.opBoolean","COPY",FACE,{"derivedFrom":makeQuery(id+"F50.opExtrude","SWEPT_FACE",FACE,{"disambiguationData":[OSD([sQuery(id+"F49.wireOp",EDGE,"E275")])]})}),makeQuery(id+"F52.opExtrude","SWEPT_FACE",FACE,{"disambiguationData":[OSD([sQuery(id+"F51.wireOp",EDGE,"E287")])]}),makeQuery(id+"F52.opExtrude","SWEPT_FACE",FACE,{"disambiguationData":[OSD([sQuery(id+"F51.wireOp",EDGE,"E288")])]})])],"derivedFrom":makeQuery(id+"F3.boolean.opBoolean","COPY",EDGE,{"derivedFrom":makeQuery(id+"F3.opExtrude","CAP_EDGE",EDGE,{"disambiguationData":[OSD([subQ1])],"isStart":false})})});}
            var Q10;
            {var subQ0=sQuery(id+"F8.wireOp",EDGE,"E142.trimOffspring");var subQ1=sQuery(id+"F8.wireOp",EDGE,"E132");Q10=makeQuery(id+"F50.boolean.opBoolean","SPLIT",EDGE,{"disambiguationData":[TD([makeQuery(id+"F9.boolean.opBoolean","COPY",FACE,{"derivedFrom":makeQuery(id+"F9.opExtrude","CAP_FACE",FACE,{"disambiguationData":[OSD([sQuery(id+"F0.wireOp",EDGE,"E0.top"),sQuery(id+"F0.wireOp",EDGE,"E0.right"),sQuery(id+"F6.wireOp",EDGE,"E68.top"),sQuery(id+"F6.wireOp",EDGE,"E70.bottom"),sQuery(id+"F8.wireOp",EDGE,"E106"),sQuery(id+"F8.wireOp",EDGE,"E107"),sQuery(id+"F8.wireOp",EDGE,"E110"),sQuery(id+"F8.wireOp",EDGE,"E111"),sQuery(id+"F8.wireOp",EDGE,"E112"),sQuery(id+"F8.wireOp",EDGE,"E114"),sQuery(id+"F8.wireOp",EDGE,"E117"),sQuery(id+"F8.wireOp",EDGE,"E118"),sQuery(id+"F8.wireOp",EDGE,"E119"),sQuery(id+"F8.wireOp",EDGE,"E120"),sQuery(id+"F8.wireOp",EDGE,"E121"),sQuery(id+"F8.wireOp",EDGE,"E123"),sQuery(id+"F8.wireOp",EDGE,"E124"),sQuery(id+"F8.wireOp",EDGE,"E125"),sQuery(id+"F8.wireOp",EDGE,"E126"),sQuery(id+"F8.wireOp",EDGE,"E127"),sQuery(id+"F8.wireOp",EDGE,"E128"),sQuery(id+"F8.wireOp",EDGE,"E129"),sQuery(id+"F8.wireOp",EDGE,"E130"),sQuery(id+"F8.wireOp",EDGE,"E131"),subQ1,sQuery(id+"F8.wireOp",EDGE,"E133"),sQuery(id+"F8.wireOp",EDGE,"E134"),sQuery(id+"F8.wireOp",EDGE,"E135"),sQuery(id+"F8.wireOp",EDGE,"E136.trimOffspring"),sQuery(id+"F8.wireOp",EDGE,"E137.trimOffspring"),sQuery(id+"F8.wireOp",EDGE,"E138.trimOffspring"),sQuery(id+"F8.wireOp",EDGE,"E139.trimOffspring"),sQuery(id+"F8.wireOp",EDGE,"E140.trimOffspring"),sQuery(id+"F8.wireOp",EDGE,"E141.trimOffspring"),subQ0])],"isStart":false})}),makeQuery(id+"F9.boolean.opBoolean","COPY",FACE,{"derivedFrom":makeQuery(id+"F9.opExtrude","SWEPT_FACE",FACE,{"disambiguationData":[OSD([subQ1])]})}),makeQuery(id+"F9.boolean.opBoolean","COPY",FACE,{"derivedFrom":makeQuery(id+"F9.opExtrude","SWEPT_FACE",FACE,{"disambiguationData":[OSD([subQ0])]})}),makeQuery(id+"F11.opExtrude","SWEPT_FACE",FACE,{"disambiguationData":[OSD([sQuery(id+"F10.wireOp",EDGE,"E145")])]}),makeQuery(id+"F11.opExtrude","SWEPT_FACE",FACE,{"disambiguationData":[OSD([sQuery(id+"F10.wireOp",EDGE,"E146")])]}),makeQuery(id+"F13.opExtrude","SWEPT_FACE",FACE,{"disambiguationData":[OSD([sQuery(id+"F12.wireOp",EDGE,"E150")])]}),makeQuery(id+"F19.opExtrude","SWEPT_FACE",FACE,{"disambiguationData":[OSD([sQuery(id+"F18.wireOp",EDGE,"E160")])]}),makeQuery(id+"F21.opExtrude","SWEPT_FACE",FACE,{"disambiguationData":[OSD([sQuery(id+"F20.wireOp",EDGE,"E164")])]}),makeQuery(id+"F50.opExtrude","SWEPT_FACE",FACE,{"disambiguationData":[OSD([sQuery(id+"F49.wireOp",EDGE,"E275")])]}),makeQuery(id+"F50.opExtrude","SWEPT_FACE",FACE,{"disambiguationData":[OSD([sQuery(id+"F49.wireOp",EDGE,"E279")])]})])],"derivedFrom":makeQuery(id+"F9.boolean.opBoolean","COPY",EDGE,{"derivedFrom":makeQuery(id+"F9.opExtrude","CAP_EDGE",EDGE,{"disambiguationData":[OSD([subQ0])],"isStart":false})})});}
            var Q11;
            {var subQ0=sQuery(id+"F8.wireOp",EDGE,"E142.trimOffspring");var subQ1=sQuery(id+"F8.wireOp",EDGE,"E135");Q11=makeQuery(id+"F50.boolean.opBoolean","SPLIT",EDGE,{"disambiguationData":[TD([makeQuery(id+"F9.boolean.opBoolean","COPY",FACE,{"derivedFrom":makeQuery(id+"F9.opExtrude","CAP_FACE",FACE,{"disambiguationData":[OSD([sQuery(id+"F0.wireOp",EDGE,"E0.top"),sQuery(id+"F0.wireOp",EDGE,"E0.right"),sQuery(id+"F6.wireOp",EDGE,"E68.top"),sQuery(id+"F6.wireOp",EDGE,"E70.bottom"),sQuery(id+"F8.wireOp",EDGE,"E106"),sQuery(id+"F8.wireOp",EDGE,"E107"),sQuery(id+"F8.wireOp",EDGE,"E110"),sQuery(id+"F8.wireOp",EDGE,"E111"),sQuery(id+"F8.wireOp",EDGE,"E112"),sQuery(id+"F8.wireOp",EDGE,"E114"),sQuery(id+"F8.wireOp",EDGE,"E117"),sQuery(id+"F8.wireOp",EDGE,"E118"),sQuery(id+"F8.wireOp",EDGE,"E119"),sQuery(id+"F8.wireOp",EDGE,"E120"),sQuery(id+"F8.wireOp",EDGE,"E121"),sQuery(id+"F8.wireOp",EDGE,"E123"),sQuery(id+"F8.wireOp",EDGE,"E124"),sQuery(id+"F8.wireOp",EDGE,"E125"),sQuery(id+"F8.wireOp",EDGE,"E126"),sQuery(id+"F8.wireOp",EDGE,"E127"),sQuery(id+"F8.wireOp",EDGE,"E128"),sQuery(id+"F8.wireOp",EDGE,"E129"),sQuery(id+"F8.wireOp",EDGE,"E130"),sQuery(id+"F8.wireOp",EDGE,"E131"),sQuery(id+"F8.wireOp",EDGE,"E132"),sQuery(id+"F8.wireOp",EDGE,"E133"),sQuery(id+"F8.wireOp",EDGE,"E134"),subQ1,sQuery(id+"F8.wireOp",EDGE,"E136.trimOffspring"),sQuery(id+"F8.wireOp",EDGE,"E137.trimOffspring"),sQuery(id+"F8.wireOp",EDGE,"E138.trimOffspring"),sQuery(id+"F8.wireOp",EDGE,"E139.trimOffspring"),sQuery(id+"F8.wireOp",EDGE,"E140.trimOffspring"),sQuery(id+"F8.wireOp",EDGE,"E141.trimOffspring"),subQ0])],"isStart":false})}),makeQuery(id+"F9.boolean.opBoolean","COPY",FACE,{"derivedFrom":makeQuery(id+"F9.opExtrude","SWEPT_FACE",FACE,{"disambiguationData":[OSD([subQ1])]})}),makeQuery(id+"F9.boolean.opBoolean","COPY",FACE,{"derivedFrom":makeQuery(id+"F9.opExtrude","SWEPT_FACE",FACE,{"disambiguationData":[OSD([subQ0])]})}),makeQuery(id+"F11.opExtrude","SWEPT_FACE",FACE,{"disambiguationData":[OSD([sQuery(id+"F10.wireOp",EDGE,"E146")])]}),makeQuery(id+"F13.opExtrude","SWEPT_FACE",FACE,{"disambiguationData":[OSD([sQuery(id+"F12.wireOp",EDGE,"E147")])]}),makeQuery(id+"F13.opExtrude","SWEPT_FACE",FACE,{"disambiguationData":[OSD([sQuery(id+"F12.wireOp",EDGE,"E150")])]}),makeQuery(id+"F19.opExtrude","SWEPT_FACE",FACE,{"disambiguationData":[OSD([sQuery(id+"F18.wireOp",EDGE,"E160")])]}),makeQuery(id+"F21.opExtrude","SWEPT_FACE",FACE,{"disambiguationData":[OSD([sQuery(id+"F20.wireOp",EDGE,"E164")])]}),makeQuery(id+"F50.opExtrude","SWEPT_FACE",FACE,{"disambiguationData":[OSD([sQuery(id+"F49.wireOp",EDGE,"E274")])]}),makeQuery(id+"F50.opExtrude","SWEPT_FACE",FACE,{"disambiguationData":[OSD([sQuery(id+"F49.wireOp",EDGE,"E278")])]})])],"derivedFrom":makeQuery(id+"F9.boolean.opBoolean","COPY",EDGE,{"derivedFrom":makeQuery(id+"F9.opExtrude","CAP_EDGE",EDGE,{"disambiguationData":[OSD([subQ0])],"isStart":false})})});}
            chamfer(context, id + "F59", {"entities" : qUnion([Q0, Q1, Q2, Q3, Q4, Q5, Q6, Q7, Q8, Q9, Q10, Q11]), "width" : 1.02 * mm, "tangentPropagation" : true});
        }
        {
            var Q0;
            Q0=makeQuery(id+"F9.boolean.opBoolean","COPY",FACE,{"derivedFrom":makeQuery(id+"F9.opExtrude","SWEPT_FACE",FACE,{"disambiguationData":[OSD([sQuery(id+"F8.wireOp",EDGE,"E126")])]})});
            var sketch = newSketch(context, id + "F60", { "sketchPlane" : qUnion([Q0])});
            skLineSegment(sketch, "E368", {"start": v(-30.55, -69.85) * mm, "end": v(-29.53, -69.85) * mm});
            skLineSegment(sketch, "E369", {"start": v(-29.53, -69.85) * mm, "end": v(-30.55, -70.87) * mm});
            skLineSegment(sketch, "E370", {"start": v(-30.55, -70.87) * mm, "end": v(-30.55, -69.85) * mm});
            skSolve(sketch);
        }
        {
            var Q0;
            Q0=makeQuery(id+"F60.imprint","IMPRINT",FACE,{"disambiguationData":[TD([[makeQuery(id+"F60.imprint","IMPRINT",EDGE,{"derivedFrom":sQuery(id+"F60.wireOp",EDGE,"E368")}),-1.0]])]});
            var Q1;
            {var subQ4=sQuery(id+"F8.wireOp",EDGE,"E137.trimOffspring");var subQ5=sQuery(id+"F8.wireOp",EDGE,"E126");Q1=makeQuery(id+"F9.boolean.opBoolean","COPY",EDGE,{"disambiguationData":[TD([makeQuery(id+"F9.opExtrude","SWEPT_FACE",FACE,{"disambiguationData":[OSD([subQ5])]})])],"derivedFrom":makeQuery(id+"F9.opExtrude","CAP_EDGE",EDGE,{"disambiguationData":[OSD([subQ4])],"isStart":false})});}
            var Q2;
            {var subQ0=sQuery(id+"F8.wireOp",EDGE,"E137.trimOffspring");var subQ1=sQuery(id+"F6.wireOp",EDGE,"E70.bottom");var subQ2=sQuery(id+"F6.wireOp",EDGE,"E68.top");var subQ3=sQuery(id+"F0.wireOp",EDGE,"E0.right");var subQ4=sQuery(id+"F0.wireOp",EDGE,"E0.top");var subQ5=makeQuery(id+"F9.opExtrude","CAP_FACE",FACE,{"disambiguationData":[OSD([subQ4,subQ3,subQ2,subQ1,sQuery(id+"F8.wireOp",EDGE,"E106"),sQuery(id+"F8.wireOp",EDGE,"E107"),sQuery(id+"F8.wireOp",EDGE,"E110"),sQuery(id+"F8.wireOp",EDGE,"E111"),sQuery(id+"F8.wireOp",EDGE,"E112"),sQuery(id+"F8.wireOp",EDGE,"E114"),sQuery(id+"F8.wireOp",EDGE,"E117"),sQuery(id+"F8.wireOp",EDGE,"E118"),sQuery(id+"F8.wireOp",EDGE,"E119"),sQuery(id+"F8.wireOp",EDGE,"E120"),sQuery(id+"F8.wireOp",EDGE,"E121"),sQuery(id+"F8.wireOp",EDGE,"E123"),sQuery(id+"F8.wireOp",EDGE,"E124"),sQuery(id+"F8.wireOp",EDGE,"E125"),sQuery(id+"F8.wireOp",EDGE,"E126"),sQuery(id+"F8.wireOp",EDGE,"E127"),sQuery(id+"F8.wireOp",EDGE,"E128"),sQuery(id+"F8.wireOp",EDGE,"E129"),sQuery(id+"F8.wireOp",EDGE,"E130"),sQuery(id+"F8.wireOp",EDGE,"E131"),sQuery(id+"F8.wireOp",EDGE,"E132"),sQuery(id+"F8.wireOp",EDGE,"E133"),sQuery(id+"F8.wireOp",EDGE,"E134"),sQuery(id+"F8.wireOp",EDGE,"E135"),sQuery(id+"F8.wireOp",EDGE,"E136.trimOffspring"),subQ0,sQuery(id+"F8.wireOp",EDGE,"E138.trimOffspring"),sQuery(id+"F8.wireOp",EDGE,"E139.trimOffspring"),sQuery(id+"F8.wireOp",EDGE,"E140.trimOffspring"),sQuery(id+"F8.wireOp",EDGE,"E141.trimOffspring"),sQuery(id+"F8.wireOp",EDGE,"E142.trimOffspring")])],"isStart":false});var subQ6=makeQuery(id+"F7.boolean.opBoolean","COPY",FACE,{"derivedFrom":makeQuery(id+"F7.opExtrude","CAP_FACE",FACE,{"disambiguationData":[OSD([sQuery(id+"F0.wireOp",EDGE,"E0.bottom"),subQ4,subQ3,sQuery(id+"F6.wireOp",EDGE,"E63.right"),sQuery(id+"F6.wireOp",EDGE,"E65.right"),sQuery(id+"F6.wireOp",EDGE,"E66.left"),sQuery(id+"F6.wireOp",EDGE,"E66.right"),sQuery(id+"F6.wireOp",EDGE,"E67.right"),subQ2,sQuery(id+"F6.wireOp",EDGE,"E68.right"),sQuery(id+"F6.wireOp",EDGE,"E69.left"),sQuery(id+"F6.wireOp",EDGE,"E69.right"),subQ1,sQuery(id+"F6.wireOp",EDGE,"E70.top"),sQuery(id+"F6.wireOp",EDGE,"E71"),sQuery(id+"F6.wireOp",EDGE,"E72"),sQuery(id+"F6.wireOp",EDGE,"E76.trimOffspring"),sQuery(id+"F6.wireOp",EDGE,"E77.trimOffspring"),sQuery(id+"F6.wireOp",EDGE,"E78.trimOffspring"),sQuery(id+"F6.wireOp",EDGE,"E79.trimOffspring"),sQuery(id+"F6.wireOp",EDGE,"E80.trimOffspring"),sQuery(id+"F6.wireOp",EDGE,"E81.right"),sQuery(id+"F6.wireOp",EDGE,"E82.bottom"),sQuery(id+"F6.wireOp",EDGE,"E83.right"),sQuery(id+"F6.wireOp",EDGE,"E84.left"),sQuery(id+"F6.wireOp",EDGE,"E84.right"),sQuery(id+"F6.wireOp",EDGE,"E85.top"),sQuery(id+"F6.wireOp",EDGE,"E85.right"),sQuery(id+"F6.wireOp",EDGE,"E86.right"),sQuery(id+"F6.wireOp",EDGE,"E87.left"),sQuery(id+"F6.wireOp",EDGE,"E87.right"),sQuery(id+"F6.wireOp",EDGE,"E88.bottom"),sQuery(id+"F6.wireOp",EDGE,"E88.top"),sQuery(id+"F6.wireOp",EDGE,"E90"),sQuery(id+"F6.wireOp",EDGE,"E92.trimOffspring"),sQuery(id+"F6.wireOp",EDGE,"E93.trimOffspring"),sQuery(id+"F6.wireOp",EDGE,"E94.trimOffspring"),sQuery(id+"F6.wireOp",EDGE,"E96.trimOffspring"),sQuery(id+"F6.wireOp",EDGE,"E100"),sQuery(id+"F6.wireOp",EDGE,"E101"),sQuery(id+"F6.wireOp",EDGE,"E102"),sQuery(id+"F6.wireOp",EDGE,"E103"),sQuery(id+"F6.wireOp",EDGE,"E104"),sQuery(id+"F6.wireOp",EDGE,"E105")])],"isStart":false})});Q2=makeQuery(id+"F48.boolean.opBoolean","SPLIT",EDGE,{"disambiguationData":[TD([makeQuery(id+"F48.opExtrude","SWEPT_FACE",FACE,{"disambiguationData":[OSD([sQuery(id+"F47.wireOp",EDGE,"E264")])]})])],"derivedFrom":makeQuery(id+"F9.boolean.opBoolean","INTERSECT",EDGE,{"derivedFrom":[subQ6,subQ5]})});}
            sweep(context, id + "F61", {"operationType" : NewBodyOperationType.ADD, "profiles" : qUnion([Q0]), "path" : qUnion([Q1, Q2])});
        }
        {
            var Q0;
            Q0=makeQuery(id+"F9.boolean.opBoolean","COPY",FACE,{"derivedFrom":makeQuery(id+"F9.opExtrude","SWEPT_FACE",FACE,{"disambiguationData":[OSD([sQuery(id+"F8.wireOp",EDGE,"E129")])]})});
            var sketch = newSketch(context, id + "F62", { "sketchPlane" : qUnion([Q0])});
            skLineSegment(sketch, "E371", {"start": v(-30.54, 69.85) * mm, "end": v(-29.52, 69.85) * mm});
            skLineSegment(sketch, "E372", {"start": v(-29.52, 69.85) * mm, "end": v(-30.54, 70.87) * mm});
            skLineSegment(sketch, "E373", {"start": v(-30.54, 70.87) * mm, "end": v(-30.54, 69.85) * mm});
            skSolve(sketch);
        }
        {
            var Q0;
            Q0=makeQuery(id+"F62.imprint","IMPRINT",FACE,{"disambiguationData":[TD([[makeQuery(id+"F62.imprint","IMPRINT",EDGE,{"derivedFrom":sQuery(id+"F62.wireOp",EDGE,"E371")}),1.0]])]});
            var Q1;
            {var subQ4=sQuery(id+"F8.wireOp",EDGE,"E137.trimOffspring");var subQ5=sQuery(id+"F8.wireOp",EDGE,"E129");Q1=makeQuery(id+"F9.boolean.opBoolean","COPY",EDGE,{"disambiguationData":[TD([makeQuery(id+"F9.opExtrude","SWEPT_FACE",FACE,{"disambiguationData":[OSD([subQ5])]})])],"derivedFrom":makeQuery(id+"F9.opExtrude","CAP_EDGE",EDGE,{"disambiguationData":[OSD([subQ4])],"isStart":false})});}
            var Q2;
            {var subQ0=sQuery(id+"F8.wireOp",EDGE,"E137.trimOffspring");var subQ1=sQuery(id+"F6.wireOp",EDGE,"E70.bottom");var subQ2=sQuery(id+"F6.wireOp",EDGE,"E68.top");var subQ3=sQuery(id+"F0.wireOp",EDGE,"E0.right");var subQ4=sQuery(id+"F0.wireOp",EDGE,"E0.top");var subQ5=makeQuery(id+"F9.opExtrude","CAP_FACE",FACE,{"disambiguationData":[OSD([subQ4,subQ3,subQ2,subQ1,sQuery(id+"F8.wireOp",EDGE,"E106"),sQuery(id+"F8.wireOp",EDGE,"E107"),sQuery(id+"F8.wireOp",EDGE,"E110"),sQuery(id+"F8.wireOp",EDGE,"E111"),sQuery(id+"F8.wireOp",EDGE,"E112"),sQuery(id+"F8.wireOp",EDGE,"E114"),sQuery(id+"F8.wireOp",EDGE,"E117"),sQuery(id+"F8.wireOp",EDGE,"E118"),sQuery(id+"F8.wireOp",EDGE,"E119"),sQuery(id+"F8.wireOp",EDGE,"E120"),sQuery(id+"F8.wireOp",EDGE,"E121"),sQuery(id+"F8.wireOp",EDGE,"E123"),sQuery(id+"F8.wireOp",EDGE,"E124"),sQuery(id+"F8.wireOp",EDGE,"E125"),sQuery(id+"F8.wireOp",EDGE,"E126"),sQuery(id+"F8.wireOp",EDGE,"E127"),sQuery(id+"F8.wireOp",EDGE,"E128"),sQuery(id+"F8.wireOp",EDGE,"E129"),sQuery(id+"F8.wireOp",EDGE,"E130"),sQuery(id+"F8.wireOp",EDGE,"E131"),sQuery(id+"F8.wireOp",EDGE,"E132"),sQuery(id+"F8.wireOp",EDGE,"E133"),sQuery(id+"F8.wireOp",EDGE,"E134"),sQuery(id+"F8.wireOp",EDGE,"E135"),sQuery(id+"F8.wireOp",EDGE,"E136.trimOffspring"),subQ0,sQuery(id+"F8.wireOp",EDGE,"E138.trimOffspring"),sQuery(id+"F8.wireOp",EDGE,"E139.trimOffspring"),sQuery(id+"F8.wireOp",EDGE,"E140.trimOffspring"),sQuery(id+"F8.wireOp",EDGE,"E141.trimOffspring"),sQuery(id+"F8.wireOp",EDGE,"E142.trimOffspring")])],"isStart":false});var subQ6=makeQuery(id+"F7.boolean.opBoolean","COPY",FACE,{"derivedFrom":makeQuery(id+"F7.opExtrude","CAP_FACE",FACE,{"disambiguationData":[OSD([sQuery(id+"F0.wireOp",EDGE,"E0.bottom"),subQ4,subQ3,sQuery(id+"F6.wireOp",EDGE,"E63.right"),sQuery(id+"F6.wireOp",EDGE,"E65.right"),sQuery(id+"F6.wireOp",EDGE,"E66.left"),sQuery(id+"F6.wireOp",EDGE,"E66.right"),sQuery(id+"F6.wireOp",EDGE,"E67.right"),subQ2,sQuery(id+"F6.wireOp",EDGE,"E68.right"),sQuery(id+"F6.wireOp",EDGE,"E69.left"),sQuery(id+"F6.wireOp",EDGE,"E69.right"),subQ1,sQuery(id+"F6.wireOp",EDGE,"E70.top"),sQuery(id+"F6.wireOp",EDGE,"E71"),sQuery(id+"F6.wireOp",EDGE,"E72"),sQuery(id+"F6.wireOp",EDGE,"E76.trimOffspring"),sQuery(id+"F6.wireOp",EDGE,"E77.trimOffspring"),sQuery(id+"F6.wireOp",EDGE,"E78.trimOffspring"),sQuery(id+"F6.wireOp",EDGE,"E79.trimOffspring"),sQuery(id+"F6.wireOp",EDGE,"E80.trimOffspring"),sQuery(id+"F6.wireOp",EDGE,"E81.right"),sQuery(id+"F6.wireOp",EDGE,"E82.bottom"),sQuery(id+"F6.wireOp",EDGE,"E83.right"),sQuery(id+"F6.wireOp",EDGE,"E84.left"),sQuery(id+"F6.wireOp",EDGE,"E84.right"),sQuery(id+"F6.wireOp",EDGE,"E85.top"),sQuery(id+"F6.wireOp",EDGE,"E85.right"),sQuery(id+"F6.wireOp",EDGE,"E86.right"),sQuery(id+"F6.wireOp",EDGE,"E87.left"),sQuery(id+"F6.wireOp",EDGE,"E87.right"),sQuery(id+"F6.wireOp",EDGE,"E88.bottom"),sQuery(id+"F6.wireOp",EDGE,"E88.top"),sQuery(id+"F6.wireOp",EDGE,"E90"),sQuery(id+"F6.wireOp",EDGE,"E92.trimOffspring"),sQuery(id+"F6.wireOp",EDGE,"E93.trimOffspring"),sQuery(id+"F6.wireOp",EDGE,"E94.trimOffspring"),sQuery(id+"F6.wireOp",EDGE,"E96.trimOffspring"),sQuery(id+"F6.wireOp",EDGE,"E100"),sQuery(id+"F6.wireOp",EDGE,"E101"),sQuery(id+"F6.wireOp",EDGE,"E102"),sQuery(id+"F6.wireOp",EDGE,"E103"),sQuery(id+"F6.wireOp",EDGE,"E104"),sQuery(id+"F6.wireOp",EDGE,"E105")])],"isStart":false})});Q2=makeQuery(id+"F48.boolean.opBoolean","SPLIT",EDGE,{"disambiguationData":[TD([makeQuery(id+"F48.opExtrude","SWEPT_FACE",FACE,{"disambiguationData":[OSD([sQuery(id+"F47.wireOp",EDGE,"E265")])]})])],"derivedFrom":makeQuery(id+"F9.boolean.opBoolean","INTERSECT",EDGE,{"derivedFrom":[subQ6,subQ5]})});}
            sweep(context, id + "F63", {"operationType" : NewBodyOperationType.ADD, "profiles" : qUnion([Q0]), "path" : qUnion([Q1, Q2])});
        }
        {
            var Q0;
            Q0=makeQuery(id+"F7.boolean.opBoolean","COPY",FACE,{"derivedFrom":makeQuery(id+"F7.opExtrude","SWEPT_FACE",FACE,{"disambiguationData":[OSD([sQuery(id+"F6.wireOp",EDGE,"E69.right"),sQuery(id+"F6.wireOp",EDGE,"E87.right")])]})});
            var sketch = newSketch(context, id + "F64", { "sketchPlane" : qUnion([Q0])});
            skLineSegment(sketch, "E374", {"start": v(-31.75, -30.4) * mm, "end": v(-31.75, -29.38) * mm});
            skLineSegment(sketch, "E375", {"start": v(-31.75, -30.4) * mm, "end": v(-32.77, -30.4) * mm});
            skLineSegment(sketch, "E376", {"start": v(-32.77, -30.4) * mm, "end": v(-31.75, -29.38) * mm});
            skSolve(sketch);
        }
        {
            var Q0;
            Q0=makeQuery(id+"F64.imprint","IMPRINT",FACE,{"disambiguationData":[TD([[makeQuery(id+"F64.imprint","IMPRINT",EDGE,{"derivedFrom":sQuery(id+"F64.wireOp",EDGE,"E374")}),1.0]])]});
            var Q1;
            {var subQ0=sQuery(id+"F6.wireOp",EDGE,"E80.trimOffspring");var subQ1=sQuery(id+"F6.wireOp",EDGE,"E87.right");var subQ2=sQuery(id+"F6.wireOp",EDGE,"E69.right");Q1=makeQuery(id+"F56.boolean.opBoolean","SPLIT",EDGE,{"disambiguationData":[TD([makeQuery(id+"F7.boolean.opBoolean","COPY",FACE,{"derivedFrom":makeQuery(id+"F7.opExtrude","CAP_FACE",FACE,{"disambiguationData":[OSD([sQuery(id+"F0.wireOp",EDGE,"E0.bottom"),sQuery(id+"F0.wireOp",EDGE,"E0.top"),sQuery(id+"F0.wireOp",EDGE,"E0.right"),sQuery(id+"F6.wireOp",EDGE,"E63.right"),sQuery(id+"F6.wireOp",EDGE,"E65.right"),sQuery(id+"F6.wireOp",EDGE,"E66.left"),sQuery(id+"F6.wireOp",EDGE,"E66.right"),sQuery(id+"F6.wireOp",EDGE,"E67.right"),sQuery(id+"F6.wireOp",EDGE,"E68.top"),sQuery(id+"F6.wireOp",EDGE,"E68.right"),sQuery(id+"F6.wireOp",EDGE,"E69.left"),subQ2,sQuery(id+"F6.wireOp",EDGE,"E70.bottom"),sQuery(id+"F6.wireOp",EDGE,"E70.top"),sQuery(id+"F6.wireOp",EDGE,"E71"),sQuery(id+"F6.wireOp",EDGE,"E72"),sQuery(id+"F6.wireOp",EDGE,"E76.trimOffspring"),sQuery(id+"F6.wireOp",EDGE,"E77.trimOffspring"),sQuery(id+"F6.wireOp",EDGE,"E78.trimOffspring"),sQuery(id+"F6.wireOp",EDGE,"E79.trimOffspring"),subQ0,sQuery(id+"F6.wireOp",EDGE,"E81.right"),sQuery(id+"F6.wireOp",EDGE,"E82.bottom"),sQuery(id+"F6.wireOp",EDGE,"E83.right"),sQuery(id+"F6.wireOp",EDGE,"E84.left"),sQuery(id+"F6.wireOp",EDGE,"E84.right"),sQuery(id+"F6.wireOp",EDGE,"E85.top"),sQuery(id+"F6.wireOp",EDGE,"E85.right"),sQuery(id+"F6.wireOp",EDGE,"E86.right"),sQuery(id+"F6.wireOp",EDGE,"E87.left"),subQ1,sQuery(id+"F6.wireOp",EDGE,"E88.bottom"),sQuery(id+"F6.wireOp",EDGE,"E88.top"),sQuery(id+"F6.wireOp",EDGE,"E90"),sQuery(id+"F6.wireOp",EDGE,"E92.trimOffspring"),sQuery(id+"F6.wireOp",EDGE,"E93.trimOffspring"),sQuery(id+"F6.wireOp",EDGE,"E94.trimOffspring"),sQuery(id+"F6.wireOp",EDGE,"E96.trimOffspring"),sQuery(id+"F6.wireOp",EDGE,"E100"),sQuery(id+"F6.wireOp",EDGE,"E101"),sQuery(id+"F6.wireOp",EDGE,"E102"),sQuery(id+"F6.wireOp",EDGE,"E103"),sQuery(id+"F6.wireOp",EDGE,"E104"),sQuery(id+"F6.wireOp",EDGE,"E105")])],"isStart":false})}),makeQuery(id+"F7.boolean.opBoolean","COPY",FACE,{"derivedFrom":makeQuery(id+"F7.opExtrude","SWEPT_FACE",FACE,{"disambiguationData":[OSD([subQ2,subQ1])]})}),makeQuery(id+"F7.boolean.opBoolean","COPY",FACE,{"derivedFrom":makeQuery(id+"F7.opExtrude","SWEPT_FACE",FACE,{"disambiguationData":[OSD([subQ0])]})}),makeQuery(id+"F15.opExtrude","SWEPT_FACE",FACE,{"disambiguationData":[OSD([sQuery(id+"F14.wireOp",EDGE,"E154")])]}),makeQuery(id+"F17.opExtrude","SWEPT_FACE",FACE,{"disambiguationData":[OSD([sQuery(id+"F16.wireOp",EDGE,"E157")])]}),makeQuery(id+"F56.opExtrude","SWEPT_FACE",FACE,{"disambiguationData":[OSD([sQuery(id+"F55.wireOp",EDGE,"E334")])]}),makeQuery(id+"F56.opExtrude","SWEPT_FACE",FACE,{"disambiguationData":[OSD([sQuery(id+"F55.wireOp",EDGE,"E335")])]})])],"derivedFrom":makeQuery(id+"F7.boolean.opBoolean","COPY",EDGE,{"derivedFrom":makeQuery(id+"F7.opExtrude","CAP_EDGE",EDGE,{"disambiguationData":[OSD([subQ0])],"isStart":false})})});}
            sweep(context, id + "F65", {"operationType" : NewBodyOperationType.ADD, "profiles" : qUnion([Q0]), "path" : qUnion([Q1])});
        }
        {
            var Q0;
            Q0=makeQuery(id+"F7.boolean.opBoolean","COPY",FACE,{"derivedFrom":makeQuery(id+"F7.opExtrude","SWEPT_FACE",FACE,{"disambiguationData":[OSD([sQuery(id+"F6.wireOp",EDGE,"E88.bottom")])]})});
            var sketch = newSketch(context, id + "F66", { "sketchPlane" : qUnion([Q0])});
            skLineSegment(sketch, "E377", {"start": v(-31.75, -68.79) * mm, "end": v(-31.75, -67.77) * mm});
            skLineSegment(sketch, "E378", {"start": v(-31.75, -67.77) * mm, "end": v(-32.77, -68.79) * mm});
            skLineSegment(sketch, "E379", {"start": v(-32.77, -68.79) * mm, "end": v(-31.75, -68.79) * mm});
            skSolve(sketch);
        }
        {
            var Q0;
            Q0=makeQuery(id+"F66.imprint","IMPRINT",FACE,{"disambiguationData":[TD([[makeQuery(id+"F66.imprint","IMPRINT",EDGE,{"derivedFrom":sQuery(id+"F66.wireOp",EDGE,"E377")}),1.0]])]});
            var Q1;
            {var subQ0=sQuery(id+"F6.wireOp",EDGE,"E96.trimOffspring");Q1=makeQuery(id+"F7.boolean.opBoolean","COPY",EDGE,{"derivedFrom":makeQuery(id+"F7.opExtrude","CAP_EDGE",EDGE,{"disambiguationData":[OSD([subQ0]),TDD([makeQuery(id+"F6.imprint","IMPRINT",EDGE,{"disambiguationData":[TD([[makeQuery(id+"F6.imprint","INTERSECT",VERTEX,{"derivedFrom":[sQuery(id+"F6.wireOp",EDGE,"E88.bottom"),subQ0]}),1.0]])],"derivedFrom":subQ0})])],"isStart":false})});}
            sweep(context, id + "F67", {"operationType" : NewBodyOperationType.ADD, "profiles" : qUnion([Q0]), "path" : qUnion([Q1])});
        }
        {
            var Q0;
            Q0=makeQuery(id+"F7.boolean.opBoolean","COPY",FACE,{"derivedFrom":makeQuery(id+"F7.opExtrude","SWEPT_FACE",FACE,{"disambiguationData":[OSD([sQuery(id+"F6.wireOp",EDGE,"E70.top")])]})});
            var sketch = newSketch(context, id + "F68", { "sketchPlane" : qUnion([Q0])});
            skLineSegment(sketch, "E380", {"start": v(-31.75, 68.79) * mm, "end": v(-31.75, 67.77) * mm});
            skLineSegment(sketch, "E381", {"start": v(-31.75, 67.77) * mm, "end": v(-32.77, 68.79) * mm});
            skLineSegment(sketch, "E382", {"start": v(-32.77, 68.79) * mm, "end": v(-31.75, 68.79) * mm});
            skSolve(sketch);
        }
        {
            var Q0;
            Q0=makeQuery(id+"F68.imprint","IMPRINT",FACE,{"disambiguationData":[TD([[makeQuery(id+"F68.imprint","IMPRINT",EDGE,{"derivedFrom":sQuery(id+"F68.wireOp",EDGE,"E380")}),-1.0]])]});
            var Q1;
            {var subQ0=sQuery(id+"F6.wireOp",EDGE,"E78.trimOffspring");Q1=makeQuery(id+"F7.boolean.opBoolean","COPY",EDGE,{"derivedFrom":makeQuery(id+"F7.opExtrude","CAP_EDGE",EDGE,{"disambiguationData":[OSD([subQ0]),TDD([makeQuery(id+"F6.imprint","IMPRINT",EDGE,{"disambiguationData":[TD([[makeQuery(id+"F6.imprint","INTERSECT",VERTEX,{"derivedFrom":[sQuery(id+"F6.wireOp",EDGE,"E70.top"),subQ0]}),-1.0]])],"derivedFrom":subQ0})])],"isStart":false})});}
            sweep(context, id + "F69", {"operationType" : NewBodyOperationType.ADD, "profiles" : qUnion([Q0]), "path" : qUnion([Q1])});
        }
        {
            var Q0;
            {var subQ0=sQuery(id+"F8.wireOp",EDGE,"E142.trimOffspring");var subQ1=sQuery(id+"F8.wireOp",EDGE,"E141.trimOffspring");var subQ2=sQuery(id+"F8.wireOp",EDGE,"E140.trimOffspring");var subQ3=sQuery(id+"F8.wireOp",EDGE,"E139.trimOffspring");var subQ4=sQuery(id+"F8.wireOp",EDGE,"E138.trimOffspring");var subQ5=sQuery(id+"F8.wireOp",EDGE,"E137.trimOffspring");var subQ6=sQuery(id+"F8.wireOp",EDGE,"E136.trimOffspring");var subQ7=sQuery(id+"F8.wireOp",EDGE,"E135");var subQ8=sQuery(id+"F8.wireOp",EDGE,"E134");var subQ9=sQuery(id+"F8.wireOp",EDGE,"E133");var subQ10=sQuery(id+"F8.wireOp",EDGE,"E132");var subQ11=sQuery(id+"F8.wireOp",EDGE,"E131");var subQ12=sQuery(id+"F8.wireOp",EDGE,"E130");var subQ13=sQuery(id+"F8.wireOp",EDGE,"E129");var subQ14=sQuery(id+"F8.wireOp",EDGE,"E128");var subQ15=sQuery(id+"F8.wireOp",EDGE,"E127");var subQ16=sQuery(id+"F8.wireOp",EDGE,"E126");var subQ17=sQuery(id+"F8.wireOp",EDGE,"E125");var subQ18=sQuery(id+"F8.wireOp",EDGE,"E124");var subQ19=sQuery(id+"F8.wireOp",EDGE,"E123");var subQ20=sQuery(id+"F8.wireOp",EDGE,"E121");var subQ21=sQuery(id+"F8.wireOp",EDGE,"E120");var subQ22=sQuery(id+"F8.wireOp",EDGE,"E119");var subQ23=sQuery(id+"F8.wireOp",EDGE,"E118");var subQ24=sQuery(id+"F8.wireOp",EDGE,"E117");var subQ25=sQuery(id+"F8.wireOp",EDGE,"E114");var subQ26=sQuery(id+"F8.wireOp",EDGE,"E112");var subQ27=sQuery(id+"F8.wireOp",EDGE,"E111");var subQ28=sQuery(id+"F8.wireOp",EDGE,"E110");var subQ29=sQuery(id+"F8.wireOp",EDGE,"E107");var subQ30=sQuery(id+"F8.wireOp",EDGE,"E106");var subQ31=sQuery(id+"F6.wireOp",EDGE,"E105");var subQ32=sQuery(id+"F6.wireOp",EDGE,"E104");var subQ33=sQuery(id+"F6.wireOp",EDGE,"E103");var subQ34=sQuery(id+"F6.wireOp",EDGE,"E102");var subQ35=sQuery(id+"F6.wireOp",EDGE,"E101");var subQ36=sQuery(id+"F6.wireOp",EDGE,"E100");var subQ37=sQuery(id+"F6.wireOp",EDGE,"E96.trimOffspring");var subQ38=sQuery(id+"F6.wireOp",EDGE,"E94.trimOffspring");var subQ39=sQuery(id+"F6.wireOp",EDGE,"E93.trimOffspring");var subQ40=sQuery(id+"F6.wireOp",EDGE,"E92.trimOffspring");var subQ41=sQuery(id+"F6.wireOp",EDGE,"E90");var subQ42=sQuery(id+"F6.wireOp",EDGE,"E88.top");var subQ43=sQuery(id+"F6.wireOp",EDGE,"E88.bottom");var subQ44=sQuery(id+"F6.wireOp",EDGE,"E87.right");var subQ45=sQuery(id+"F6.wireOp",EDGE,"E87.left");var subQ46=sQuery(id+"F6.wireOp",EDGE,"E86.right");var subQ47=sQuery(id+"F6.wireOp",EDGE,"E85.right");var subQ48=sQuery(id+"F6.wireOp",EDGE,"E85.top");var subQ49=sQuery(id+"F6.wireOp",EDGE,"E84.right");var subQ50=sQuery(id+"F6.wireOp",EDGE,"E84.left");var subQ51=sQuery(id+"F6.wireOp",EDGE,"E83.right");var subQ52=sQuery(id+"F6.wireOp",EDGE,"E82.bottom");var subQ53=sQuery(id+"F6.wireOp",EDGE,"E81.right");var subQ54=sQuery(id+"F6.wireOp",EDGE,"E80.trimOffspring");var subQ55=sQuery(id+"F6.wireOp",EDGE,"E79.trimOffspring");var subQ56=sQuery(id+"F6.wireOp",EDGE,"E78.trimOffspring");var subQ57=sQuery(id+"F6.wireOp",EDGE,"E77.trimOffspring");var subQ58=sQuery(id+"F6.wireOp",EDGE,"E76.trimOffspring");var subQ59=sQuery(id+"F6.wireOp",EDGE,"E72");var subQ60=sQuery(id+"F6.wireOp",EDGE,"E71");var subQ61=sQuery(id+"F6.wireOp",EDGE,"E70.top");var subQ62=sQuery(id+"F6.wireOp",EDGE,"E70.bottom");var subQ63=sQuery(id+"F6.wireOp",EDGE,"E69.right");var subQ64=sQuery(id+"F6.wireOp",EDGE,"E69.left");var subQ65=sQuery(id+"F6.wireOp",EDGE,"E68.right");var subQ66=sQuery(id+"F6.wireOp",EDGE,"E68.top");var subQ67=sQuery(id+"F6.wireOp",EDGE,"E67.right");var subQ68=sQuery(id+"F6.wireOp",EDGE,"E66.right");var subQ69=sQuery(id+"F6.wireOp",EDGE,"E66.left");var subQ70=sQuery(id+"F6.wireOp",EDGE,"E65.right");var subQ71=sQuery(id+"F6.wireOp",EDGE,"E63.right");var subQ72=sQuery(id+"F0.wireOp",EDGE,"E0.right");var subQ73=sQuery(id+"F0.wireOp",EDGE,"E0.top");var subQ74=sQuery(id+"F0.wireOp",EDGE,"E0.bottom");var subQ75=sQuery(id+"F24.wireOp",EDGE,"E212");var subQ76=makeQuery(id+"F17.opExtrude","SWEPT_FACE",FACE,{"disambiguationData":[OSD([sQuery(id+"F16.wireOp",EDGE,"E157")])]});var subQ77=makeQuery(id+"F15.opExtrude","SWEPT_FACE",FACE,{"disambiguationData":[OSD([sQuery(id+"F14.wireOp",EDGE,"E154")])]});var subQ78=makeQuery(id+"F7.boolean.opBoolean","COPY",FACE,{"derivedFrom":makeQuery(id+"F7.opExtrude","CAP_FACE",FACE,{"disambiguationData":[OSD([subQ74,subQ73,subQ72,subQ71,subQ70,subQ69,subQ68,subQ67,subQ66,subQ65,subQ64,subQ63,subQ62,subQ61,subQ60,subQ59,subQ58,subQ57,subQ56,subQ55,subQ54,subQ53,subQ52,subQ51,subQ50,subQ49,subQ48,subQ47,subQ46,subQ45,subQ44,subQ43,subQ42,subQ41,subQ40,subQ39,subQ38,subQ37,subQ36,subQ35,subQ34,subQ33,subQ32,subQ31])],"isStart":false})});Q0=makeQuery(id+"F61.boolean.opBoolean","MERGE",FACE,{"derivedFrom":[makeQuery(id+"F56.boolean.opBoolean","SPLIT",FACE,{"disambiguationData":[TD([makeQuery(id+"F1.opExtrude","SWEPT_FACE",FACE,{"disambiguationData":[OSD([subQ74])]}),subQ78,makeQuery(id+"F7.boolean.opBoolean","COPY",FACE,{"derivedFrom":makeQuery(id+"F7.opExtrude","SWEPT_FACE",FACE,{"disambiguationData":[OSD([subQ68,subQ49])]})}),makeQuery(id+"F7.boolean.opBoolean","COPY",FACE,{"derivedFrom":makeQuery(id+"F7.opExtrude","SWEPT_FACE",FACE,{"disambiguationData":[OSD([subQ67,subQ47])]})}),makeQuery(id+"F7.boolean.opBoolean","COPY",FACE,{"derivedFrom":makeQuery(id+"F7.opExtrude","SWEPT_FACE",FACE,{"disambiguationData":[OSD([subQ62])]})}),makeQuery(id+"F7.boolean.opBoolean","COPY",FACE,{"derivedFrom":makeQuery(id+"F7.opExtrude","SWEPT_FACE",FACE,{"disambiguationData":[OSD([subQ59])]})}),makeQuery(id+"F7.boolean.opBoolean","COPY",FACE,{"derivedFrom":makeQuery(id+"F7.opExtrude","SWEPT_FACE",FACE,{"disambiguationData":[OSD([subQ56]),TDD([makeQuery(id+"F6.imprint","IMPRINT",EDGE,{"disambiguationData":[TD([[makeQuery(id+"F6.imprint","INTERSECT",VERTEX,{"derivedFrom":[subQ62,subQ56]}),1.0]])],"derivedFrom":subQ56})])]})}),makeQuery(id+"F7.boolean.opBoolean","COPY",FACE,{"derivedFrom":makeQuery(id+"F7.opExtrude","SWEPT_FACE",FACE,{"disambiguationData":[OSD([subQ48])]})}),makeQuery(id+"F7.boolean.opBoolean","COPY",FACE,{"derivedFrom":makeQuery(id+"F7.opExtrude","SWEPT_FACE",FACE,{"disambiguationData":[OSD([subQ43])]})}),makeQuery(id+"F7.boolean.opBoolean","COPY",FACE,{"derivedFrom":makeQuery(id+"F7.opExtrude","SWEPT_FACE",FACE,{"disambiguationData":[OSD([subQ40])]})}),makeQuery(id+"F7.boolean.opBoolean","COPY",FACE,{"derivedFrom":makeQuery(id+"F7.opExtrude","SWEPT_FACE",FACE,{"disambiguationData":[OSD([subQ39])]})}),makeQuery(id+"F7.boolean.opBoolean","COPY",FACE,{"derivedFrom":makeQuery(id+"F7.opExtrude","SWEPT_FACE",FACE,{"disambiguationData":[OSD([subQ37]),TDD([makeQuery(id+"F6.imprint","IMPRINT",EDGE,{"disambiguationData":[TD([[makeQuery(id+"F6.imprint","INTERSECT",VERTEX,{"derivedFrom":[subQ43,subQ37]}),1.0]])],"derivedFrom":subQ37})])]})}),makeQuery(id+"F9.boolean.opBoolean","COPY",FACE,{"derivedFrom":makeQuery(id+"F9.opExtrude","CAP_FACE",FACE,{"disambiguationData":[OSD([subQ73,subQ72,subQ66,subQ62,subQ30,subQ29,subQ28,subQ27,subQ26,subQ25,subQ24,subQ23,subQ22,subQ21,subQ20,subQ19,subQ18,subQ17,subQ16,subQ15,subQ14,subQ13,subQ12,subQ11,subQ10,subQ9,subQ8,subQ7,subQ6,subQ5,subQ4,subQ3,subQ2,subQ1,subQ0])],"isStart":false})}),makeQuery(id+"F9.boolean.opBoolean","COPY",FACE,{"derivedFrom":makeQuery(id+"F9.opExtrude","SWEPT_FACE",FACE,{"disambiguationData":[OSD([subQ18])]})}),makeQuery(id+"F9.boolean.opBoolean","COPY",FACE,{"derivedFrom":makeQuery(id+"F9.opExtrude","SWEPT_FACE",FACE,{"disambiguationData":[OSD([subQ5])]})}),makeQuery(id+"F11.opExtrude","SWEPT_FACE",FACE,{"disambiguationData":[OSD([sQuery(id+"F10.wireOp",EDGE,"E146")])]}),makeQuery(id+"F13.opExtrude","SWEPT_FACE",FACE,{"disambiguationData":[OSD([sQuery(id+"F12.wireOp",EDGE,"E150")])]}),subQ77,subQ76,makeQuery(id+"F19.opExtrude","SWEPT_FACE",FACE,{"disambiguationData":[OSD([sQuery(id+"F18.wireOp",EDGE,"E160")])]}),makeQuery(id+"F21.opExtrude","SWEPT_FACE",FACE,{"disambiguationData":[OSD([sQuery(id+"F20.wireOp",EDGE,"E164")])]}),makeQuery(id+"F25.boolean.opBoolean","COPY",FACE,{"derivedFrom":makeQuery(id+"F25.opExtrude","CAP_FACE",FACE,{"disambiguationData":[OSD([subQ74,sQuery(id+"F0.wireOp",EDGE,"E0.left"),subQ72,sQuery(id+"F2.wireOp",EDGE,"E5.bottom"),sQuery(id+"F2.wireOp",EDGE,"E5.right"),sQuery(id+"F4.wireOp",EDGE,"E22.bottom"),sQuery(id+"F4.wireOp",EDGE,"E22.right"),subQ69,subQ67,sQuery(id+"F24.wireOp",EDGE,"E201"),sQuery(id+"F24.wireOp",EDGE,"E202"),sQuery(id+"F24.wireOp",EDGE,"E203"),sQuery(id+"F24.wireOp",EDGE,"E204"),sQuery(id+"F24.wireOp",EDGE,"E205"),sQuery(id+"F24.wireOp",EDGE,"E206"),sQuery(id+"F24.wireOp",EDGE,"E207"),sQuery(id+"F24.wireOp",EDGE,"E208"),sQuery(id+"F24.wireOp",EDGE,"E209"),sQuery(id+"F24.wireOp",EDGE,"E210"),sQuery(id+"F24.wireOp",EDGE,"E211"),subQ75,sQuery(id+"F24.wireOp",EDGE,"E213"),sQuery(id+"F24.wireOp",EDGE,"E214"),sQuery(id+"F24.wireOp",EDGE,"E215"),sQuery(id+"F24.wireOp",EDGE,"E216"),sQuery(id+"F24.wireOp",EDGE,"E217"),sQuery(id+"F24.wireOp",EDGE,"E218"),sQuery(id+"F24.wireOp",EDGE,"E219"),sQuery(id+"F24.wireOp",EDGE,"E220"),sQuery(id+"F24.wireOp",EDGE,"E221"),sQuery(id+"F24.wireOp",EDGE,"E222"),sQuery(id+"F24.wireOp",EDGE,"E223"),sQuery(id+"F24.wireOp",EDGE,"E224"),sQuery(id+"F24.wireOp",EDGE,"E225"),sQuery(id+"F24.wireOp",EDGE,"E226"),sQuery(id+"F24.wireOp",EDGE,"E227.trimOffspring"),sQuery(id+"F24.wireOp",EDGE,"E228.trimOffspring"),sQuery(id+"F24.wireOp",EDGE,"E229.trimOffspring"),sQuery(id+"F24.wireOp",EDGE,"E230.trimOffspring"),sQuery(id+"F24.wireOp",EDGE,"E231.trimOffspring"),sQuery(id+"F24.wireOp",EDGE,"E232.trimOffspring"),sQuery(id+"F24.wireOp",EDGE,"E233.trimOffspring")])],"isStart":false})}),makeQuery(id+"F25.boolean.opBoolean","COPY",FACE,{"derivedFrom":makeQuery(id+"F25.opExtrude","SWEPT_FACE",FACE,{"disambiguationData":[OSD([subQ75])]})}),makeQuery(id+"F27.opExtrude","SWEPT_FACE",FACE,{"disambiguationData":[OSD([sQuery(id+"F26.wireOp",EDGE,"E236")])]}),makeQuery(id+"F29.opExtrude","SWEPT_FACE",FACE,{"disambiguationData":[OSD([sQuery(id+"F28.wireOp",EDGE,"E240")])]}),makeQuery(id+"F31.opExtrude","SWEPT_FACE",FACE,{"disambiguationData":[OSD([sQuery(id+"F30.wireOp",EDGE,"E246")])]}),makeQuery(id+"FIjozfq1HljYPPT_1.opChamfer","BLEND_FACE",FACE,{"disambiguationData":[OSD([subQ30])]}),makeQuery(id+"F48.boolean.opBoolean","COPY",FACE,{"derivedFrom":makeQuery(id+"F48.opExtrude","SWEPT_FACE",FACE,{"disambiguationData":[OSD([sQuery(id+"F47.wireOp",EDGE,"E264")])]})}),makeQuery(id+"F56.opExtrude","SWEPT_FACE",FACE,{"disambiguationData":[OSD([sQuery(id+"F55.wireOp",EDGE,"E339")])]}),makeQuery(id+"F56.opExtrude","SWEPT_FACE",FACE,{"disambiguationData":[OSD([sQuery(id+"F55.wireOp",EDGE,"E342")])]}),makeQuery(id+"F56.opExtrude","SWEPT_FACE",FACE,{"disambiguationData":[OSD([sQuery(id+"F55.wireOp",EDGE,"E344")])]}),makeQuery(id+"F56.opExtrude","SWEPT_FACE",FACE,{"disambiguationData":[OSD([sQuery(id+"F55.wireOp",EDGE,"E345")])]}),makeQuery(id+"F56.opExtrude","SWEPT_FACE",FACE,{"disambiguationData":[OSD([subQ59])]})])],"derivedFrom":makeQuery(id+"F17.boolean.opBoolean","MERGE",FACE,{"derivedFrom":[makeQuery(id+"F15.boolean.opBoolean","MERGE",FACE,{"derivedFrom":[subQ78,subQ77]}),subQ76]})}),makeQuery(id+"F61.opSweep","SWEPT_FACE",FACE,{"disambiguationData":[OSD([subQ74,subQ73,subQ72,subQ71,subQ70,subQ69,subQ68,subQ67,subQ66,subQ65,subQ64,subQ63,subQ62,subQ61,subQ60,subQ59,subQ58,subQ57,subQ56,subQ55,subQ54,subQ53,subQ52,subQ51,subQ50,subQ49,subQ48,subQ47,subQ46,subQ45,subQ44,subQ43,subQ42,subQ41,subQ40,subQ39,subQ38,subQ37,subQ36,subQ35,subQ34,subQ33,subQ32,subQ31,subQ30,subQ29,subQ28,subQ27,subQ26,subQ25,subQ24,subQ23,subQ22,subQ21,subQ20,subQ19,subQ18,subQ17,subQ16,subQ15,subQ14,subQ13,subQ12,subQ11,subQ10,subQ9,subQ8,subQ7,subQ6,subQ5,subQ4,subQ3,subQ2,subQ1,subQ0,sQuery(id+"F60.wireOp",EDGE,"E370")])]})]});}
            var sketch = newSketch(context, id + "F70", { "sketchPlane" : qUnion([Q0])});
            skLineSegment(sketch, "E383", {"start": v(69.96, 2.4) * mm, "end": v(70.05, 1.27) * mm});
            skLineSegment(sketch, "E384", {"start": v(70.05, 1.27) * mm, "end": v(68.96, 1.27) * mm});
            skLineSegment(sketch, "E385", {"start": v(68.96, 1.27) * mm, "end": v(68.96, 2.6) * mm});
            skLineSegment(sketch, "E386", {"start": v(68.96, 2.6) * mm, "end": v(69.96, 2.4) * mm});
            skSolve(sketch);
        }
        {
            var Q0;
            Q0=makeQuery(id+"F67.opSweep","CAP_FACE",FACE,{"disambiguationData":[OSD([sQuery(id+"F0.wireOp",EDGE,"E0.bottom"),sQuery(id+"F0.wireOp",EDGE,"E0.top"),sQuery(id+"F0.wireOp",EDGE,"E0.right"),sQuery(id+"F6.wireOp",EDGE,"E63.right"),sQuery(id+"F6.wireOp",EDGE,"E65.right"),sQuery(id+"F6.wireOp",EDGE,"E66.left"),sQuery(id+"F6.wireOp",EDGE,"E66.right"),sQuery(id+"F6.wireOp",EDGE,"E67.right"),sQuery(id+"F6.wireOp",EDGE,"E68.top"),sQuery(id+"F6.wireOp",EDGE,"E68.right"),sQuery(id+"F6.wireOp",EDGE,"E69.left"),sQuery(id+"F6.wireOp",EDGE,"E69.right"),sQuery(id+"F6.wireOp",EDGE,"E70.bottom"),sQuery(id+"F6.wireOp",EDGE,"E70.top"),sQuery(id+"F6.wireOp",EDGE,"E71"),sQuery(id+"F6.wireOp",EDGE,"E72"),sQuery(id+"F6.wireOp",EDGE,"E76.trimOffspring"),sQuery(id+"F6.wireOp",EDGE,"E77.trimOffspring"),sQuery(id+"F6.wireOp",EDGE,"E78.trimOffspring"),sQuery(id+"F6.wireOp",EDGE,"E79.trimOffspring"),sQuery(id+"F6.wireOp",EDGE,"E80.trimOffspring"),sQuery(id+"F6.wireOp",EDGE,"E81.right"),sQuery(id+"F6.wireOp",EDGE,"E82.bottom"),sQuery(id+"F6.wireOp",EDGE,"E83.right"),sQuery(id+"F6.wireOp",EDGE,"E84.left"),sQuery(id+"F6.wireOp",EDGE,"E84.right"),sQuery(id+"F6.wireOp",EDGE,"E85.top"),sQuery(id+"F6.wireOp",EDGE,"E85.right"),sQuery(id+"F6.wireOp",EDGE,"E86.right"),sQuery(id+"F6.wireOp",EDGE,"E87.left"),sQuery(id+"F6.wireOp",EDGE,"E87.right"),sQuery(id+"F6.wireOp",EDGE,"E88.bottom"),sQuery(id+"F6.wireOp",EDGE,"E88.top"),sQuery(id+"F6.wireOp",EDGE,"E90"),sQuery(id+"F6.wireOp",EDGE,"E92.trimOffspring"),sQuery(id+"F6.wireOp",EDGE,"E93.trimOffspring"),sQuery(id+"F6.wireOp",EDGE,"E94.trimOffspring"),sQuery(id+"F6.wireOp",EDGE,"E96.trimOffspring"),sQuery(id+"F6.wireOp",EDGE,"E100"),sQuery(id+"F6.wireOp",EDGE,"E101"),sQuery(id+"F6.wireOp",EDGE,"E102"),sQuery(id+"F6.wireOp",EDGE,"E103"),sQuery(id+"F6.wireOp",EDGE,"E104"),sQuery(id+"F6.wireOp",EDGE,"E105"),sQuery(id+"F8.wireOp",EDGE,"E137.trimOffspring"),sQuery(id+"F66.wireOp",EDGE,"E377"),sQuery(id+"F66.wireOp",EDGE,"E378"),sQuery(id+"F66.wireOp",EDGE,"E379")])],"isStart":false});
            var sketch = newSketch(context, id + "F71", { "sketchPlane" : qUnion([Q0])});
            skLineSegment(sketch, "E387", {"start": v(-31.75, 67) * mm, "end": v(-31.75, 68) * mm});
            skLineSegment(sketch, "E388", {"start": v(-31.75, 68) * mm, "end": v(-32.77, 68) * mm});
            skLineSegment(sketch, "E389", {"start": v(-32.77, 68) * mm, "end": v(-31.75, 67) * mm});
            skSolve(sketch);
        }
        {
            var Q0;
            Q0=makeQuery(id+"F71.imprint","IMPRINT",FACE,{"disambiguationData":[TD([[makeQuery(id+"F71.imprint","IMPRINT",EDGE,{"derivedFrom":sQuery(id+"F71.wireOp",EDGE,"E387")}),1.0]])]});
            var Q1;
            Q1=sQuery(id+"F70.wireOp",EDGE,"E383");
            sweep(context, id + "F72", {"operationType" : NewBodyOperationType.ADD, "profiles" : qUnion([Q0]), "path" : qUnion([Q1])});
        }
        {
            var Q0;
            {var subQ0=sQuery(id+"F8.wireOp",EDGE,"E142.trimOffspring");var subQ1=sQuery(id+"F8.wireOp",EDGE,"E141.trimOffspring");var subQ2=sQuery(id+"F8.wireOp",EDGE,"E140.trimOffspring");var subQ3=sQuery(id+"F8.wireOp",EDGE,"E139.trimOffspring");var subQ4=sQuery(id+"F8.wireOp",EDGE,"E138.trimOffspring");var subQ5=sQuery(id+"F8.wireOp",EDGE,"E137.trimOffspring");var subQ6=sQuery(id+"F8.wireOp",EDGE,"E136.trimOffspring");var subQ7=sQuery(id+"F8.wireOp",EDGE,"E135");var subQ8=sQuery(id+"F8.wireOp",EDGE,"E134");var subQ9=sQuery(id+"F8.wireOp",EDGE,"E133");var subQ10=sQuery(id+"F8.wireOp",EDGE,"E132");var subQ11=sQuery(id+"F8.wireOp",EDGE,"E131");var subQ12=sQuery(id+"F8.wireOp",EDGE,"E130");var subQ13=sQuery(id+"F8.wireOp",EDGE,"E129");var subQ14=sQuery(id+"F8.wireOp",EDGE,"E128");var subQ15=sQuery(id+"F8.wireOp",EDGE,"E127");var subQ16=sQuery(id+"F8.wireOp",EDGE,"E126");var subQ17=sQuery(id+"F8.wireOp",EDGE,"E125");var subQ18=sQuery(id+"F8.wireOp",EDGE,"E124");var subQ19=sQuery(id+"F8.wireOp",EDGE,"E123");var subQ20=sQuery(id+"F8.wireOp",EDGE,"E121");var subQ21=sQuery(id+"F8.wireOp",EDGE,"E120");var subQ22=sQuery(id+"F8.wireOp",EDGE,"E119");var subQ23=sQuery(id+"F8.wireOp",EDGE,"E118");var subQ24=sQuery(id+"F8.wireOp",EDGE,"E117");var subQ25=sQuery(id+"F8.wireOp",EDGE,"E114");var subQ26=sQuery(id+"F8.wireOp",EDGE,"E112");var subQ27=sQuery(id+"F8.wireOp",EDGE,"E111");var subQ28=sQuery(id+"F8.wireOp",EDGE,"E110");var subQ29=sQuery(id+"F8.wireOp",EDGE,"E107");var subQ30=sQuery(id+"F8.wireOp",EDGE,"E106");var subQ31=sQuery(id+"F6.wireOp",EDGE,"E105");var subQ32=sQuery(id+"F6.wireOp",EDGE,"E104");var subQ33=sQuery(id+"F6.wireOp",EDGE,"E103");var subQ34=sQuery(id+"F6.wireOp",EDGE,"E102");var subQ35=sQuery(id+"F6.wireOp",EDGE,"E101");var subQ36=sQuery(id+"F6.wireOp",EDGE,"E100");var subQ37=sQuery(id+"F6.wireOp",EDGE,"E96.trimOffspring");var subQ38=sQuery(id+"F6.wireOp",EDGE,"E94.trimOffspring");var subQ39=sQuery(id+"F6.wireOp",EDGE,"E93.trimOffspring");var subQ40=sQuery(id+"F6.wireOp",EDGE,"E92.trimOffspring");var subQ41=sQuery(id+"F6.wireOp",EDGE,"E90");var subQ42=sQuery(id+"F6.wireOp",EDGE,"E88.top");var subQ43=sQuery(id+"F6.wireOp",EDGE,"E88.bottom");var subQ44=sQuery(id+"F6.wireOp",EDGE,"E87.right");var subQ45=sQuery(id+"F6.wireOp",EDGE,"E87.left");var subQ46=sQuery(id+"F6.wireOp",EDGE,"E86.right");var subQ47=sQuery(id+"F6.wireOp",EDGE,"E85.right");var subQ48=sQuery(id+"F6.wireOp",EDGE,"E85.top");var subQ49=sQuery(id+"F6.wireOp",EDGE,"E84.right");var subQ50=sQuery(id+"F6.wireOp",EDGE,"E84.left");var subQ51=sQuery(id+"F6.wireOp",EDGE,"E83.right");var subQ52=sQuery(id+"F6.wireOp",EDGE,"E82.bottom");var subQ53=sQuery(id+"F6.wireOp",EDGE,"E81.right");var subQ54=sQuery(id+"F6.wireOp",EDGE,"E80.trimOffspring");var subQ55=sQuery(id+"F6.wireOp",EDGE,"E79.trimOffspring");var subQ56=sQuery(id+"F6.wireOp",EDGE,"E78.trimOffspring");var subQ57=sQuery(id+"F6.wireOp",EDGE,"E77.trimOffspring");var subQ58=sQuery(id+"F6.wireOp",EDGE,"E76.trimOffspring");var subQ59=sQuery(id+"F6.wireOp",EDGE,"E72");var subQ60=sQuery(id+"F6.wireOp",EDGE,"E71");var subQ61=sQuery(id+"F6.wireOp",EDGE,"E70.top");var subQ62=sQuery(id+"F6.wireOp",EDGE,"E70.bottom");var subQ63=sQuery(id+"F6.wireOp",EDGE,"E69.right");var subQ64=sQuery(id+"F6.wireOp",EDGE,"E69.left");var subQ65=sQuery(id+"F6.wireOp",EDGE,"E68.right");var subQ66=sQuery(id+"F6.wireOp",EDGE,"E68.top");var subQ67=sQuery(id+"F6.wireOp",EDGE,"E67.right");var subQ68=sQuery(id+"F6.wireOp",EDGE,"E66.right");var subQ69=sQuery(id+"F6.wireOp",EDGE,"E66.left");var subQ70=sQuery(id+"F6.wireOp",EDGE,"E65.right");var subQ71=sQuery(id+"F6.wireOp",EDGE,"E63.right");var subQ72=sQuery(id+"F0.wireOp",EDGE,"E0.right");var subQ73=sQuery(id+"F0.wireOp",EDGE,"E0.top");var subQ74=sQuery(id+"F0.wireOp",EDGE,"E0.bottom");var subQ75=makeQuery(id+"F17.opExtrude","SWEPT_FACE",FACE,{"disambiguationData":[OSD([sQuery(id+"F16.wireOp",EDGE,"E157")])]});var subQ76=makeQuery(id+"F15.opExtrude","SWEPT_FACE",FACE,{"disambiguationData":[OSD([sQuery(id+"F14.wireOp",EDGE,"E154")])]});var subQ77=makeQuery(id+"F7.boolean.opBoolean","COPY",FACE,{"derivedFrom":makeQuery(id+"F7.opExtrude","CAP_FACE",FACE,{"disambiguationData":[OSD([subQ74,subQ73,subQ72,subQ71,subQ70,subQ69,subQ68,subQ67,subQ66,subQ65,subQ64,subQ63,subQ62,subQ61,subQ60,subQ59,subQ58,subQ57,subQ56,subQ55,subQ54,subQ53,subQ52,subQ51,subQ50,subQ49,subQ48,subQ47,subQ46,subQ45,subQ44,subQ43,subQ42,subQ41,subQ40,subQ39,subQ38,subQ37,subQ36,subQ35,subQ34,subQ33,subQ32,subQ31])],"isStart":false})});var subQ78=sQuery(id+"Flw17BiXidal6mr_1.wireOp",EDGE,"0af28365-1b66-499a-ab2e-de65ff7b6a86");Q0=makeQuery(id+"F63.boolean.opBoolean","MERGE",FACE,{"derivedFrom":[makeQuery(id+"F56.boolean.opBoolean","SPLIT",FACE,{"disambiguationData":[TD([makeQuery(id+"F1.opExtrude","CAP_FACE",FACE,{"disambiguationData":[OSD([subQ74,subQ73,sQuery(id+"F0.wireOp",EDGE,"E0.left"),subQ72])],"isStart":false}),makeQuery(id+"F1.opExtrude","SWEPT_FACE",FACE,{"disambiguationData":[OSD([subQ73])]}),subQ77,makeQuery(id+"F7.boolean.opBoolean","COPY",FACE,{"derivedFrom":makeQuery(id+"F7.opExtrude","SWEPT_FACE",FACE,{"disambiguationData":[OSD([subQ66])]})}),makeQuery(id+"F7.boolean.opBoolean","COPY",FACE,{"derivedFrom":makeQuery(id+"F7.opExtrude","SWEPT_FACE",FACE,{"disambiguationData":[OSD([subQ65,subQ46])]})}),makeQuery(id+"F7.boolean.opBoolean","COPY",FACE,{"derivedFrom":makeQuery(id+"F7.opExtrude","SWEPT_FACE",FACE,{"disambiguationData":[OSD([subQ63,subQ44])]})}),makeQuery(id+"F7.boolean.opBoolean","COPY",FACE,{"derivedFrom":makeQuery(id+"F7.opExtrude","SWEPT_FACE",FACE,{"disambiguationData":[OSD([subQ61])]})}),makeQuery(id+"F7.boolean.opBoolean","COPY",FACE,{"derivedFrom":makeQuery(id+"F7.opExtrude","SWEPT_FACE",FACE,{"disambiguationData":[OSD([subQ59])]})}),makeQuery(id+"F7.boolean.opBoolean","COPY",FACE,{"derivedFrom":makeQuery(id+"F7.opExtrude","SWEPT_FACE",FACE,{"disambiguationData":[OSD([subQ56]),TDD([makeQuery(id+"F6.imprint","IMPRINT",EDGE,{"disambiguationData":[TD([[makeQuery(id+"F6.imprint","INTERSECT",VERTEX,{"derivedFrom":[subQ61,subQ56]}),-1.0]])],"derivedFrom":subQ56})])]})}),makeQuery(id+"F7.boolean.opBoolean","COPY",FACE,{"derivedFrom":makeQuery(id+"F7.opExtrude","SWEPT_FACE",FACE,{"disambiguationData":[OSD([subQ55])]})}),makeQuery(id+"F7.boolean.opBoolean","COPY",FACE,{"derivedFrom":makeQuery(id+"F7.opExtrude","SWEPT_FACE",FACE,{"disambiguationData":[OSD([subQ54])]})}),makeQuery(id+"F7.boolean.opBoolean","COPY",FACE,{"derivedFrom":makeQuery(id+"F7.opExtrude","SWEPT_FACE",FACE,{"disambiguationData":[OSD([subQ42])]})}),makeQuery(id+"F7.boolean.opBoolean","COPY",FACE,{"derivedFrom":makeQuery(id+"F7.opExtrude","SWEPT_FACE",FACE,{"disambiguationData":[OSD([subQ41])]})}),makeQuery(id+"F7.boolean.opBoolean","COPY",FACE,{"derivedFrom":makeQuery(id+"F7.opExtrude","SWEPT_FACE",FACE,{"disambiguationData":[OSD([subQ37]),TDD([makeQuery(id+"F6.imprint","IMPRINT",EDGE,{"disambiguationData":[TD([[makeQuery(id+"F6.imprint","INTERSECT",VERTEX,{"derivedFrom":[subQ42,subQ37]}),-1.0]])],"derivedFrom":subQ37})])]})}),makeQuery(id+"F9.boolean.opBoolean","COPY",FACE,{"derivedFrom":makeQuery(id+"F9.opExtrude","CAP_FACE",FACE,{"disambiguationData":[OSD([subQ73,subQ72,subQ66,subQ62,subQ30,subQ29,subQ28,subQ27,subQ26,subQ25,subQ24,subQ23,subQ22,subQ21,subQ20,subQ19,subQ18,subQ17,subQ16,subQ15,subQ14,subQ13,subQ12,subQ11,subQ10,subQ9,subQ8,subQ7,subQ6,subQ5,subQ4,subQ3,subQ2,subQ1,subQ0])],"isStart":false})}),makeQuery(id+"F9.boolean.opBoolean","COPY",FACE,{"derivedFrom":makeQuery(id+"F9.opExtrude","SWEPT_FACE",FACE,{"disambiguationData":[OSD([subQ13])]})}),makeQuery(id+"F9.boolean.opBoolean","COPY",FACE,{"derivedFrom":makeQuery(id+"F9.opExtrude","SWEPT_FACE",FACE,{"disambiguationData":[OSD([subQ5])]})}),makeQuery(id+"F11.opExtrude","SWEPT_FACE",FACE,{"disambiguationData":[OSD([sQuery(id+"F10.wireOp",EDGE,"E146")])]}),makeQuery(id+"F13.opExtrude","SWEPT_FACE",FACE,{"disambiguationData":[OSD([sQuery(id+"F12.wireOp",EDGE,"E150")])]}),subQ76,subQ75,makeQuery(id+"F19.opExtrude","SWEPT_FACE",FACE,{"disambiguationData":[OSD([sQuery(id+"F18.wireOp",EDGE,"E160")])]}),makeQuery(id+"F21.opExtrude","SWEPT_FACE",FACE,{"disambiguationData":[OSD([sQuery(id+"F20.wireOp",EDGE,"E164")])]}),makeQuery(id+"FmACc5hAtWqNUO1_1.boolean.opBoolean","COPY",FACE,{"derivedFrom":makeQuery(id+"FmACc5hAtWqNUO1_1.opExtrude","CAP_FACE",FACE,{"disambiguationData":[OSD([subQ73,subQ72,subQ46,subQ45,subQ26,subQ19,sQuery(id+"Flw17BiXidal6mr_1.wireOp",EDGE,"20ed3367-6ab1-4e56-8e50-3a7674f5b3ae"),sQuery(id+"Flw17BiXidal6mr_1.wireOp",EDGE,"5031668d-57e3-4508-92f2-52b2a7ebf961"),sQuery(id+"Flw17BiXidal6mr_1.wireOp",EDGE,"b37ea369-2277-42d6-b46c-83231ec1927c"),sQuery(id+"Flw17BiXidal6mr_1.wireOp",EDGE,"6aba5c06-92d8-45b4-a986-68685e58f0db"),sQuery(id+"Flw17BiXidal6mr_1.wireOp",EDGE,"3d538ced-5a6d-4f38-9053-b9a16892e3e1"),sQuery(id+"Flw17BiXidal6mr_1.wireOp",EDGE,"2db6cdb7-c100-47ed-8778-4dabc674b8e0"),sQuery(id+"Flw17BiXidal6mr_1.wireOp",EDGE,"2184db61-b3a4-4b34-af2e-4445c2bfe314"),sQuery(id+"Flw17BiXidal6mr_1.wireOp",EDGE,"0c97e5ae-808c-4e60-a421-af6bff30c0e3"),subQ78,sQuery(id+"Flw17BiXidal6mr_1.wireOp",EDGE,"f03e8806-3266-40d1-9106-97eae4b60223"),sQuery(id+"Flw17BiXidal6mr_1.wireOp",EDGE,"6fcd0532-88b4-4c9f-9bda-6bf5efbccc1e"),sQuery(id+"Flw17BiXidal6mr_1.wireOp",EDGE,"4932e17d-cd2b-41fd-a58d-95cce7f888dc"),sQuery(id+"Flw17BiXidal6mr_1.wireOp",EDGE,"87a31968-b156-4a9a-9b7f-83ceab37d8fc"),sQuery(id+"Flw17BiXidal6mr_1.wireOp",EDGE,"9513ede8-fc51-437c-8b66-3faf9dd2206c"),sQuery(id+"Flw17BiXidal6mr_1.wireOp",EDGE,"377adf44-8487-40f5-b30e-18140566c0db"),sQuery(id+"Flw17BiXidal6mr_1.wireOp",EDGE,"19e0e5b0-a71c-49b9-931e-f36e82718861"),sQuery(id+"Flw17BiXidal6mr_1.wireOp",EDGE,"0883066e-ea23-4f62-bbf1-b5da4cc1089a"),sQuery(id+"Flw17BiXidal6mr_1.wireOp",EDGE,"e5afcdd8-6684-416f-ac6f-a548f6dc78d7"),sQuery(id+"Flw17BiXidal6mr_1.wireOp",EDGE,"115e4ddc-c018-411a-9652-01672927bc3d"),sQuery(id+"Flw17BiXidal6mr_1.wireOp",EDGE,"84795e9d-8fd2-41bb-ba8e-9445e912e342"),sQuery(id+"Flw17BiXidal6mr_1.wireOp",EDGE,"a02ba8a0-ff60-428e-9ec3-190f0482f39f"),sQuery(id+"Flw17BiXidal6mr_1.wireOp",EDGE,"1d4fe523-9ba2-4af5-a417-0059de39a54f"),sQuery(id+"Flw17BiXidal6mr_1.wireOp",EDGE,"2a830c38-a2b9-4629-9e47-600a7330d0ce"),sQuery(id+"Flw17BiXidal6mr_1.wireOp",EDGE,"2132dfcd-bd06-444e-9f49-1a73281b547c"),sQuery(id+"Flw17BiXidal6mr_1.wireOp",EDGE,"6499348c-cc00-47f4-9d11-77e11a1a1294"),sQuery(id+"Flw17BiXidal6mr_1.wireOp",EDGE,"a662d74b-2aa2-4ccc-8d5c-6be1faf658bd"),sQuery(id+"Flw17BiXidal6mr_1.wireOp",EDGE,"d3fdd793-9dba-4860-a2e5-7a596f417945.trimOffspring"),sQuery(id+"Flw17BiXidal6mr_1.wireOp",EDGE,"ffd8cfbb-ef1c-47c0-a142-4cbf59d12af1.trimOffspring"),sQuery(id+"Flw17BiXidal6mr_1.wireOp",EDGE,"666ddb3b-524d-4b42-8c04-9b92ff96bf29.trimOffspring"),sQuery(id+"Flw17BiXidal6mr_1.wireOp",EDGE,"14093485-f8ee-4ea4-acb7-195841529fe2.trimOffspring"),sQuery(id+"Flw17BiXidal6mr_1.wireOp",EDGE,"60b59175-6990-4d3c-a1b5-ad6cb1c0067e.trimOffspring"),sQuery(id+"Flw17BiXidal6mr_1.wireOp",EDGE,"496cf426-abc3-4659-a69b-4c01ce7b3e9e.trimOffspring"),sQuery(id+"Flw17BiXidal6mr_1.wireOp",EDGE,"a21cda65-0813-4859-8d6a-a2c4641910ca.trimOffspring")])],"isStart":false})}),makeQuery(id+"FmACc5hAtWqNUO1_1.boolean.opBoolean","COPY",FACE,{"derivedFrom":makeQuery(id+"FmACc5hAtWqNUO1_1.opExtrude","SWEPT_FACE",FACE,{"disambiguationData":[OSD([subQ78])]})}),makeQuery(id+"FmxpSjMhRZl7OnT_1.opExtrude","SWEPT_FACE",FACE,{"disambiguationData":[OSD([sQuery(id+"F1PQOgr5voJ7vcG_1.wireOp",EDGE,"sixpWMla-wf2q-dhxU-nqy0-X66fETwmPjs1")])]}),makeQuery(id+"Fk1ukvspPKSAlsu_1.opExtrude","SWEPT_FACE",FACE,{"disambiguationData":[OSD([sQuery(id+"FOtCb518LSPuNts_1.wireOp",EDGE,"sHSQaFdY-QJ5v-9IDn-cJL8-as6bCOgNzHlh")])]}),makeQuery(id+"F48.boolean.opBoolean","COPY",FACE,{"derivedFrom":makeQuery(id+"F48.opExtrude","SWEPT_FACE",FACE,{"disambiguationData":[OSD([sQuery(id+"F47.wireOp",EDGE,"E264")])]})}),makeQuery(id+"F48.boolean.opBoolean","COPY",FACE,{"derivedFrom":makeQuery(id+"F48.opExtrude","SWEPT_FACE",FACE,{"disambiguationData":[OSD([sQuery(id+"F47.wireOp",EDGE,"E265")])]})}),makeQuery(id+"F56.opExtrude","SWEPT_FACE",FACE,{"disambiguationData":[OSD([sQuery(id+"F55.wireOp",EDGE,"E334")])]}),makeQuery(id+"F56.opExtrude","SWEPT_FACE",FACE,{"disambiguationData":[OSD([sQuery(id+"F55.wireOp",EDGE,"E335")])]}),makeQuery(id+"F56.opExtrude","SWEPT_FACE",FACE,{"disambiguationData":[OSD([sQuery(id+"F55.wireOp",EDGE,"E339")])]}),makeQuery(id+"F56.opExtrude","SWEPT_FACE",FACE,{"disambiguationData":[OSD([sQuery(id+"F55.wireOp",EDGE,"E340")])]}),makeQuery(id+"F56.opExtrude","SWEPT_FACE",FACE,{"disambiguationData":[OSD([sQuery(id+"F55.wireOp",EDGE,"E342")])]}),makeQuery(id+"F56.opExtrude","SWEPT_FACE",FACE,{"disambiguationData":[OSD([subQ59])]}),makeQuery(id+"F56.opExtrude","SWEPT_FACE",FACE,{"disambiguationData":[OSD([subQ41])]})])],"derivedFrom":makeQuery(id+"F17.boolean.opBoolean","MERGE",FACE,{"derivedFrom":[makeQuery(id+"F15.boolean.opBoolean","MERGE",FACE,{"derivedFrom":[subQ77,subQ76]}),subQ75]})}),makeQuery(id+"F63.opSweep","SWEPT_FACE",FACE,{"disambiguationData":[OSD([subQ74,subQ73,subQ72,subQ71,subQ70,subQ69,subQ68,subQ67,subQ66,subQ65,subQ64,subQ63,subQ62,subQ61,subQ60,subQ59,subQ58,subQ57,subQ56,subQ55,subQ54,subQ53,subQ52,subQ51,subQ50,subQ49,subQ48,subQ47,subQ46,subQ45,subQ44,subQ43,subQ42,subQ41,subQ40,subQ39,subQ38,subQ37,subQ36,subQ35,subQ34,subQ33,subQ32,subQ31,subQ30,subQ29,subQ28,subQ27,subQ26,subQ25,subQ24,subQ23,subQ22,subQ21,subQ20,subQ19,subQ18,subQ17,subQ16,subQ15,subQ14,subQ13,subQ12,subQ11,subQ10,subQ9,subQ8,subQ7,subQ6,subQ5,subQ4,subQ3,subQ2,subQ1,subQ0,sQuery(id+"F62.wireOp",EDGE,"E373")])]})]});}
            var sketch = newSketch(context, id + "F73", { "sketchPlane" : qUnion([Q0])});
            skLineSegment(sketch, "E390", {"start": v(69.95, -2.48) * mm, "end": v(70.05, -1.27) * mm});
            skSolve(sketch);
        }
        {
            var Q0;
            Q0=makeQuery(id+"F69.opSweep","CAP_FACE",FACE,{"disambiguationData":[OSD([sQuery(id+"F0.wireOp",EDGE,"E0.bottom"),sQuery(id+"F0.wireOp",EDGE,"E0.top"),sQuery(id+"F0.wireOp",EDGE,"E0.right"),sQuery(id+"F6.wireOp",EDGE,"E63.right"),sQuery(id+"F6.wireOp",EDGE,"E65.right"),sQuery(id+"F6.wireOp",EDGE,"E66.left"),sQuery(id+"F6.wireOp",EDGE,"E66.right"),sQuery(id+"F6.wireOp",EDGE,"E67.right"),sQuery(id+"F6.wireOp",EDGE,"E68.top"),sQuery(id+"F6.wireOp",EDGE,"E68.right"),sQuery(id+"F6.wireOp",EDGE,"E69.left"),sQuery(id+"F6.wireOp",EDGE,"E69.right"),sQuery(id+"F6.wireOp",EDGE,"E70.bottom"),sQuery(id+"F6.wireOp",EDGE,"E70.top"),sQuery(id+"F6.wireOp",EDGE,"E71"),sQuery(id+"F6.wireOp",EDGE,"E72"),sQuery(id+"F6.wireOp",EDGE,"E76.trimOffspring"),sQuery(id+"F6.wireOp",EDGE,"E77.trimOffspring"),sQuery(id+"F6.wireOp",EDGE,"E78.trimOffspring"),sQuery(id+"F6.wireOp",EDGE,"E79.trimOffspring"),sQuery(id+"F6.wireOp",EDGE,"E80.trimOffspring"),sQuery(id+"F6.wireOp",EDGE,"E81.right"),sQuery(id+"F6.wireOp",EDGE,"E82.bottom"),sQuery(id+"F6.wireOp",EDGE,"E83.right"),sQuery(id+"F6.wireOp",EDGE,"E84.left"),sQuery(id+"F6.wireOp",EDGE,"E84.right"),sQuery(id+"F6.wireOp",EDGE,"E85.top"),sQuery(id+"F6.wireOp",EDGE,"E85.right"),sQuery(id+"F6.wireOp",EDGE,"E86.right"),sQuery(id+"F6.wireOp",EDGE,"E87.left"),sQuery(id+"F6.wireOp",EDGE,"E87.right"),sQuery(id+"F6.wireOp",EDGE,"E88.bottom"),sQuery(id+"F6.wireOp",EDGE,"E88.top"),sQuery(id+"F6.wireOp",EDGE,"E90"),sQuery(id+"F6.wireOp",EDGE,"E92.trimOffspring"),sQuery(id+"F6.wireOp",EDGE,"E93.trimOffspring"),sQuery(id+"F6.wireOp",EDGE,"E94.trimOffspring"),sQuery(id+"F6.wireOp",EDGE,"E96.trimOffspring"),sQuery(id+"F6.wireOp",EDGE,"E100"),sQuery(id+"F6.wireOp",EDGE,"E101"),sQuery(id+"F6.wireOp",EDGE,"E102"),sQuery(id+"F6.wireOp",EDGE,"E103"),sQuery(id+"F6.wireOp",EDGE,"E104"),sQuery(id+"F6.wireOp",EDGE,"E105"),sQuery(id+"F8.wireOp",EDGE,"E137.trimOffspring"),sQuery(id+"F68.wireOp",EDGE,"E380"),sQuery(id+"F68.wireOp",EDGE,"E381"),sQuery(id+"F68.wireOp",EDGE,"E382")])],"isStart":false});
            var sketch = newSketch(context, id + "F74", { "sketchPlane" : qUnion([Q0])});
            skLineSegment(sketch, "E391", {"start": v(-31.75, -67) * mm, "end": v(-31.75, -68.02) * mm});
            skLineSegment(sketch, "E392", {"start": v(-31.75, -68.02) * mm, "end": v(-32.77, -68.02) * mm});
            skLineSegment(sketch, "E393", {"start": v(-32.77, -68.02) * mm, "end": v(-31.75, -67) * mm});
            skSolve(sketch);
        }
        {
            var Q0;
            Q0=makeQuery(id+"F74.imprint","IMPRINT",FACE,{"disambiguationData":[TD([[makeQuery(id+"F74.imprint","IMPRINT",EDGE,{"derivedFrom":sQuery(id+"F74.wireOp",EDGE,"E391")}),1.0]])]});
            var Q1;
            Q1=sQuery(id+"F73.wireOp",EDGE,"E390");
            sweep(context, id + "F75", {"operationType" : NewBodyOperationType.ADD, "profiles" : qUnion([Q0]), "path" : qUnion([Q1])});
        }
        {
            var Q0;
            Q0=makeQuery(id+"F34.opExtrude","CAP_EDGE",EDGE,{"disambiguationData":[OSD([sQuery(id+"F33.wireOp",EDGE,"E251.MirrorCS")])],"isStart":false});
            var Q1;
            Q1=makeQuery(id+"F34.opExtrude","CAP_EDGE",EDGE,{"disambiguationData":[OSD([sQuery(id+"F33.wireOp",EDGE,"E250")])],"isStart":false});
            fillet(context, id + "F76", {"entities" : qUnion([Q0, Q1]), "radius" : 0.76 * mm, "tangentPropagation" : true, "allowEdgeOverflow" : false});
        }
        {
            var Q0;
            {var subQ0=sQuery(id+"F2.wireOp",EDGE,"E12.trimOffspring");var subQ1=sQuery(id+"F2.wireOp",EDGE,"E4.left");Q0=makeQuery(id+"F52.boolean.opBoolean","SPLIT",EDGE,{"disambiguationData":[TD([makeQuery(id+"F3.boolean.opBoolean","COPY",FACE,{"derivedFrom":makeQuery(id+"F3.opExtrude","CAP_FACE",FACE,{"disambiguationData":[OSD([sQuery(id+"F0.wireOp",EDGE,"E0.bottom"),sQuery(id+"F0.wireOp",EDGE,"E0.top"),sQuery(id+"F0.wireOp",EDGE,"E0.left"),sQuery(id+"F2.wireOp",EDGE,"E1.top"),sQuery(id+"F2.wireOp",EDGE,"E1.right"),sQuery(id+"F2.wireOp",EDGE,"E2.bottom"),sQuery(id+"F2.wireOp",EDGE,"E2.top"),sQuery(id+"F2.wireOp",EDGE,"E3.top"),sQuery(id+"F2.wireOp",EDGE,"E3.right"),subQ1,sQuery(id+"F2.wireOp",EDGE,"E4.right"),sQuery(id+"F2.wireOp",EDGE,"E5.top"),sQuery(id+"F2.wireOp",EDGE,"E5.right"),sQuery(id+"F2.wireOp",EDGE,"E6.top"),sQuery(id+"F2.wireOp",EDGE,"E6.right"),sQuery(id+"F2.wireOp",EDGE,"E7.left"),sQuery(id+"F2.wireOp",EDGE,"E7.right"),sQuery(id+"F2.wireOp",EDGE,"E8.bottom"),sQuery(id+"F2.wireOp",EDGE,"E8.top"),sQuery(id+"F2.wireOp",EDGE,"E9"),sQuery(id+"F2.wireOp",EDGE,"E10"),subQ0,sQuery(id+"F2.wireOp",EDGE,"E13.trimOffspring"),sQuery(id+"F2.wireOp",EDGE,"E14.trimOffspring"),sQuery(id+"F2.wireOp",EDGE,"E15.trimOffspring"),sQuery(id+"F2.wireOp",EDGE,"E16.trimOffspring"),sQuery(id+"F2.wireOp",EDGE,"E17.trimOffspring"),sQuery(id+"F2.wireOp",EDGE,"E18.trimOffspring")])],"isStart":false})}),makeQuery(id+"F3.boolean.opBoolean","COPY",FACE,{"derivedFrom":makeQuery(id+"F3.opExtrude","SWEPT_FACE",FACE,{"disambiguationData":[OSD([subQ1])]})}),makeQuery(id+"F3.boolean.opBoolean","COPY",FACE,{"derivedFrom":makeQuery(id+"F3.opExtrude","SWEPT_FACE",FACE,{"disambiguationData":[OSD([subQ0])]})}),makeQuery(id+"F52.opExtrude","SWEPT_FACE",FACE,{"disambiguationData":[OSD([sQuery(id+"F51.wireOp",EDGE,"E301")])]}),makeQuery(id+"F52.opExtrude","SWEPT_FACE",FACE,{"disambiguationData":[OSD([sQuery(id+"F51.wireOp",EDGE,"E305")])]})])],"derivedFrom":makeQuery(id+"F3.boolean.opBoolean","COPY",EDGE,{"derivedFrom":makeQuery(id+"F3.opExtrude","CAP_EDGE",EDGE,{"disambiguationData":[OSD([subQ0])],"isStart":false})})});}
            var Q1;
            {var subQ0=sQuery(id+"F2.wireOp",EDGE,"E12.trimOffspring");var subQ1=sQuery(id+"F2.wireOp",EDGE,"E4.right");Q1=makeQuery(id+"F52.boolean.opBoolean","SPLIT",EDGE,{"disambiguationData":[TD([makeQuery(id+"F3.boolean.opBoolean","COPY",FACE,{"derivedFrom":makeQuery(id+"F3.opExtrude","CAP_FACE",FACE,{"disambiguationData":[OSD([sQuery(id+"F0.wireOp",EDGE,"E0.bottom"),sQuery(id+"F0.wireOp",EDGE,"E0.top"),sQuery(id+"F0.wireOp",EDGE,"E0.left"),sQuery(id+"F2.wireOp",EDGE,"E1.top"),sQuery(id+"F2.wireOp",EDGE,"E1.right"),sQuery(id+"F2.wireOp",EDGE,"E2.bottom"),sQuery(id+"F2.wireOp",EDGE,"E2.top"),sQuery(id+"F2.wireOp",EDGE,"E3.top"),sQuery(id+"F2.wireOp",EDGE,"E3.right"),sQuery(id+"F2.wireOp",EDGE,"E4.left"),subQ1,sQuery(id+"F2.wireOp",EDGE,"E5.top"),sQuery(id+"F2.wireOp",EDGE,"E5.right"),sQuery(id+"F2.wireOp",EDGE,"E6.top"),sQuery(id+"F2.wireOp",EDGE,"E6.right"),sQuery(id+"F2.wireOp",EDGE,"E7.left"),sQuery(id+"F2.wireOp",EDGE,"E7.right"),sQuery(id+"F2.wireOp",EDGE,"E8.bottom"),sQuery(id+"F2.wireOp",EDGE,"E8.top"),sQuery(id+"F2.wireOp",EDGE,"E9"),sQuery(id+"F2.wireOp",EDGE,"E10"),subQ0,sQuery(id+"F2.wireOp",EDGE,"E13.trimOffspring"),sQuery(id+"F2.wireOp",EDGE,"E14.trimOffspring"),sQuery(id+"F2.wireOp",EDGE,"E15.trimOffspring"),sQuery(id+"F2.wireOp",EDGE,"E16.trimOffspring"),sQuery(id+"F2.wireOp",EDGE,"E17.trimOffspring"),sQuery(id+"F2.wireOp",EDGE,"E18.trimOffspring")])],"isStart":false})}),makeQuery(id+"F3.boolean.opBoolean","COPY",FACE,{"derivedFrom":makeQuery(id+"F3.opExtrude","SWEPT_FACE",FACE,{"disambiguationData":[OSD([subQ1])]})}),makeQuery(id+"F3.boolean.opBoolean","COPY",FACE,{"derivedFrom":makeQuery(id+"F3.opExtrude","SWEPT_FACE",FACE,{"disambiguationData":[OSD([subQ0])]})}),makeQuery(id+"F52.opExtrude","SWEPT_FACE",FACE,{"disambiguationData":[OSD([sQuery(id+"F51.wireOp",EDGE,"E302")])]}),makeQuery(id+"F52.opExtrude","SWEPT_FACE",FACE,{"disambiguationData":[OSD([sQuery(id+"F51.wireOp",EDGE,"E305")])]})])],"derivedFrom":makeQuery(id+"F3.boolean.opBoolean","COPY",EDGE,{"derivedFrom":makeQuery(id+"F3.opExtrude","CAP_EDGE",EDGE,{"disambiguationData":[OSD([subQ0])],"isStart":false})})});}
            var Q2;
            {var subQ0=sQuery(id+"F24.wireOp",EDGE,"E231.trimOffspring");var subQ1=sQuery(id+"F24.wireOp",EDGE,"E223");Q2=makeQuery(id+"F58.boolean.opBoolean","SPLIT",EDGE,{"disambiguationData":[TD([makeQuery(id+"F25.boolean.opBoolean","COPY",FACE,{"derivedFrom":makeQuery(id+"F25.opExtrude","CAP_FACE",FACE,{"disambiguationData":[OSD([sQuery(id+"F0.wireOp",EDGE,"E0.bottom"),sQuery(id+"F0.wireOp",EDGE,"E0.left"),sQuery(id+"F0.wireOp",EDGE,"E0.right"),sQuery(id+"F2.wireOp",EDGE,"E5.bottom"),sQuery(id+"F2.wireOp",EDGE,"E5.right"),sQuery(id+"F4.wireOp",EDGE,"E22.bottom"),sQuery(id+"F4.wireOp",EDGE,"E22.right"),sQuery(id+"F6.wireOp",EDGE,"E66.left"),sQuery(id+"F6.wireOp",EDGE,"E67.right"),sQuery(id+"F24.wireOp",EDGE,"E201"),sQuery(id+"F24.wireOp",EDGE,"E202"),sQuery(id+"F24.wireOp",EDGE,"E203"),sQuery(id+"F24.wireOp",EDGE,"E204"),sQuery(id+"F24.wireOp",EDGE,"E205"),sQuery(id+"F24.wireOp",EDGE,"E206"),sQuery(id+"F24.wireOp",EDGE,"E207"),sQuery(id+"F24.wireOp",EDGE,"E208"),sQuery(id+"F24.wireOp",EDGE,"E209"),sQuery(id+"F24.wireOp",EDGE,"E210"),sQuery(id+"F24.wireOp",EDGE,"E211"),sQuery(id+"F24.wireOp",EDGE,"E212"),sQuery(id+"F24.wireOp",EDGE,"E213"),sQuery(id+"F24.wireOp",EDGE,"E214"),sQuery(id+"F24.wireOp",EDGE,"E215"),sQuery(id+"F24.wireOp",EDGE,"E216"),sQuery(id+"F24.wireOp",EDGE,"E217"),sQuery(id+"F24.wireOp",EDGE,"E218"),sQuery(id+"F24.wireOp",EDGE,"E219"),sQuery(id+"F24.wireOp",EDGE,"E220"),sQuery(id+"F24.wireOp",EDGE,"E221"),sQuery(id+"F24.wireOp",EDGE,"E222"),subQ1,sQuery(id+"F24.wireOp",EDGE,"E224"),sQuery(id+"F24.wireOp",EDGE,"E225"),sQuery(id+"F24.wireOp",EDGE,"E226"),sQuery(id+"F24.wireOp",EDGE,"E227.trimOffspring"),sQuery(id+"F24.wireOp",EDGE,"E228.trimOffspring"),sQuery(id+"F24.wireOp",EDGE,"E229.trimOffspring"),sQuery(id+"F24.wireOp",EDGE,"E230.trimOffspring"),subQ0,sQuery(id+"F24.wireOp",EDGE,"E232.trimOffspring"),sQuery(id+"F24.wireOp",EDGE,"E233.trimOffspring")])],"isStart":false})}),makeQuery(id+"F25.boolean.opBoolean","COPY",FACE,{"derivedFrom":makeQuery(id+"F25.opExtrude","SWEPT_FACE",FACE,{"disambiguationData":[OSD([subQ1])]})}),makeQuery(id+"F25.boolean.opBoolean","COPY",FACE,{"derivedFrom":makeQuery(id+"F25.opExtrude","SWEPT_FACE",FACE,{"disambiguationData":[OSD([subQ0])]})}),makeQuery(id+"F27.opExtrude","SWEPT_FACE",FACE,{"disambiguationData":[OSD([sQuery(id+"F26.wireOp",EDGE,"E236")])]}),makeQuery(id+"F29.opExtrude","SWEPT_FACE",FACE,{"disambiguationData":[OSD([sQuery(id+"F28.wireOp",EDGE,"E240")])]}),makeQuery(id+"F31.opExtrude","SWEPT_FACE",FACE,{"disambiguationData":[OSD([sQuery(id+"F30.wireOp",EDGE,"E246")])]}),makeQuery(id+"F58.opExtrude","SWEPT_FACE",FACE,{"disambiguationData":[OSD([sQuery(id+"F57.wireOp",EDGE,"E356")])]}),makeQuery(id+"F58.opExtrude","SWEPT_FACE",FACE,{"disambiguationData":[OSD([sQuery(id+"F57.wireOp",EDGE,"E367")])]})])],"derivedFrom":makeQuery(id+"F25.boolean.opBoolean","COPY",EDGE,{"derivedFrom":makeQuery(id+"F25.opExtrude","CAP_EDGE",EDGE,{"disambiguationData":[OSD([subQ0])],"isStart":false})})});}
            var Q3;
            {var subQ0=sQuery(id+"F24.wireOp",EDGE,"E231.trimOffspring");var subQ1=sQuery(id+"F24.wireOp",EDGE,"E226");Q3=makeQuery(id+"F58.boolean.opBoolean","SPLIT",EDGE,{"disambiguationData":[TD([makeQuery(id+"F25.boolean.opBoolean","COPY",FACE,{"derivedFrom":makeQuery(id+"F25.opExtrude","CAP_FACE",FACE,{"disambiguationData":[OSD([sQuery(id+"F0.wireOp",EDGE,"E0.bottom"),sQuery(id+"F0.wireOp",EDGE,"E0.left"),sQuery(id+"F0.wireOp",EDGE,"E0.right"),sQuery(id+"F2.wireOp",EDGE,"E5.bottom"),sQuery(id+"F2.wireOp",EDGE,"E5.right"),sQuery(id+"F4.wireOp",EDGE,"E22.bottom"),sQuery(id+"F4.wireOp",EDGE,"E22.right"),sQuery(id+"F6.wireOp",EDGE,"E66.left"),sQuery(id+"F6.wireOp",EDGE,"E67.right"),sQuery(id+"F24.wireOp",EDGE,"E201"),sQuery(id+"F24.wireOp",EDGE,"E202"),sQuery(id+"F24.wireOp",EDGE,"E203"),sQuery(id+"F24.wireOp",EDGE,"E204"),sQuery(id+"F24.wireOp",EDGE,"E205"),sQuery(id+"F24.wireOp",EDGE,"E206"),sQuery(id+"F24.wireOp",EDGE,"E207"),sQuery(id+"F24.wireOp",EDGE,"E208"),sQuery(id+"F24.wireOp",EDGE,"E209"),sQuery(id+"F24.wireOp",EDGE,"E210"),sQuery(id+"F24.wireOp",EDGE,"E211"),sQuery(id+"F24.wireOp",EDGE,"E212"),sQuery(id+"F24.wireOp",EDGE,"E213"),sQuery(id+"F24.wireOp",EDGE,"E214"),sQuery(id+"F24.wireOp",EDGE,"E215"),sQuery(id+"F24.wireOp",EDGE,"E216"),sQuery(id+"F24.wireOp",EDGE,"E217"),sQuery(id+"F24.wireOp",EDGE,"E218"),sQuery(id+"F24.wireOp",EDGE,"E219"),sQuery(id+"F24.wireOp",EDGE,"E220"),sQuery(id+"F24.wireOp",EDGE,"E221"),sQuery(id+"F24.wireOp",EDGE,"E222"),sQuery(id+"F24.wireOp",EDGE,"E223"),sQuery(id+"F24.wireOp",EDGE,"E224"),sQuery(id+"F24.wireOp",EDGE,"E225"),subQ1,sQuery(id+"F24.wireOp",EDGE,"E227.trimOffspring"),sQuery(id+"F24.wireOp",EDGE,"E228.trimOffspring"),sQuery(id+"F24.wireOp",EDGE,"E229.trimOffspring"),sQuery(id+"F24.wireOp",EDGE,"E230.trimOffspring"),subQ0,sQuery(id+"F24.wireOp",EDGE,"E232.trimOffspring"),sQuery(id+"F24.wireOp",EDGE,"E233.trimOffspring")])],"isStart":false})}),makeQuery(id+"F25.boolean.opBoolean","COPY",FACE,{"derivedFrom":makeQuery(id+"F25.opExtrude","SWEPT_FACE",FACE,{"disambiguationData":[OSD([subQ1])]})}),makeQuery(id+"F25.boolean.opBoolean","COPY",FACE,{"derivedFrom":makeQuery(id+"F25.opExtrude","SWEPT_FACE",FACE,{"disambiguationData":[OSD([subQ0])]})}),makeQuery(id+"F27.opExtrude","SWEPT_FACE",FACE,{"disambiguationData":[OSD([sQuery(id+"F26.wireOp",EDGE,"E236")])]}),makeQuery(id+"F29.opExtrude","SWEPT_FACE",FACE,{"disambiguationData":[OSD([sQuery(id+"F28.wireOp",EDGE,"E240")])]}),makeQuery(id+"F31.opExtrude","SWEPT_FACE",FACE,{"disambiguationData":[OSD([sQuery(id+"F30.wireOp",EDGE,"E246")])]}),makeQuery(id+"F58.opExtrude","SWEPT_FACE",FACE,{"disambiguationData":[OSD([sQuery(id+"F57.wireOp",EDGE,"E354")])]}),makeQuery(id+"F58.opExtrude","SWEPT_FACE",FACE,{"disambiguationData":[OSD([sQuery(id+"F57.wireOp",EDGE,"E367")])]})])],"derivedFrom":makeQuery(id+"F25.boolean.opBoolean","COPY",EDGE,{"derivedFrom":makeQuery(id+"F25.opExtrude","CAP_EDGE",EDGE,{"disambiguationData":[OSD([subQ0])],"isStart":false})})});}
            var Q4;
            {var subQ0=sQuery(id+"F24.wireOp",EDGE,"E212");var subQ1=sQuery(id+"F24.wireOp",EDGE,"E227.trimOffspring");Q4=makeQuery(id+"F58.boolean.opBoolean","SPLIT",EDGE,{"disambiguationData":[TD([makeQuery(id+"F25.boolean.opBoolean","COPY",FACE,{"derivedFrom":makeQuery(id+"F25.opExtrude","CAP_FACE",FACE,{"disambiguationData":[OSD([sQuery(id+"F0.wireOp",EDGE,"E0.bottom"),sQuery(id+"F0.wireOp",EDGE,"E0.left"),sQuery(id+"F0.wireOp",EDGE,"E0.right"),sQuery(id+"F2.wireOp",EDGE,"E5.bottom"),sQuery(id+"F2.wireOp",EDGE,"E5.right"),sQuery(id+"F4.wireOp",EDGE,"E22.bottom"),sQuery(id+"F4.wireOp",EDGE,"E22.right"),sQuery(id+"F6.wireOp",EDGE,"E66.left"),sQuery(id+"F6.wireOp",EDGE,"E67.right"),sQuery(id+"F24.wireOp",EDGE,"E201"),sQuery(id+"F24.wireOp",EDGE,"E202"),sQuery(id+"F24.wireOp",EDGE,"E203"),sQuery(id+"F24.wireOp",EDGE,"E204"),sQuery(id+"F24.wireOp",EDGE,"E205"),sQuery(id+"F24.wireOp",EDGE,"E206"),sQuery(id+"F24.wireOp",EDGE,"E207"),sQuery(id+"F24.wireOp",EDGE,"E208"),sQuery(id+"F24.wireOp",EDGE,"E209"),sQuery(id+"F24.wireOp",EDGE,"E210"),sQuery(id+"F24.wireOp",EDGE,"E211"),subQ0,sQuery(id+"F24.wireOp",EDGE,"E213"),sQuery(id+"F24.wireOp",EDGE,"E214"),sQuery(id+"F24.wireOp",EDGE,"E215"),sQuery(id+"F24.wireOp",EDGE,"E216"),sQuery(id+"F24.wireOp",EDGE,"E217"),sQuery(id+"F24.wireOp",EDGE,"E218"),sQuery(id+"F24.wireOp",EDGE,"E219"),sQuery(id+"F24.wireOp",EDGE,"E220"),sQuery(id+"F24.wireOp",EDGE,"E221"),sQuery(id+"F24.wireOp",EDGE,"E222"),sQuery(id+"F24.wireOp",EDGE,"E223"),sQuery(id+"F24.wireOp",EDGE,"E224"),sQuery(id+"F24.wireOp",EDGE,"E225"),sQuery(id+"F24.wireOp",EDGE,"E226"),subQ1,sQuery(id+"F24.wireOp",EDGE,"E228.trimOffspring"),sQuery(id+"F24.wireOp",EDGE,"E229.trimOffspring"),sQuery(id+"F24.wireOp",EDGE,"E230.trimOffspring"),sQuery(id+"F24.wireOp",EDGE,"E231.trimOffspring"),sQuery(id+"F24.wireOp",EDGE,"E232.trimOffspring"),sQuery(id+"F24.wireOp",EDGE,"E233.trimOffspring")])],"isStart":false})}),makeQuery(id+"F25.boolean.opBoolean","COPY",FACE,{"derivedFrom":makeQuery(id+"F25.opExtrude","SWEPT_FACE",FACE,{"disambiguationData":[OSD([subQ0])]})}),makeQuery(id+"F25.boolean.opBoolean","COPY",FACE,{"derivedFrom":makeQuery(id+"F25.opExtrude","SWEPT_FACE",FACE,{"disambiguationData":[OSD([subQ1])]})}),makeQuery(id+"F27.opExtrude","SWEPT_FACE",FACE,{"disambiguationData":[OSD([sQuery(id+"F26.wireOp",EDGE,"E236")])]}),makeQuery(id+"F29.opExtrude","SWEPT_FACE",FACE,{"disambiguationData":[OSD([sQuery(id+"F28.wireOp",EDGE,"E240")])]}),makeQuery(id+"F31.opExtrude","SWEPT_FACE",FACE,{"disambiguationData":[OSD([sQuery(id+"F30.wireOp",EDGE,"E246")])]}),makeQuery(id+"F56.boolean.opBoolean","COPY",FACE,{"derivedFrom":makeQuery(id+"F56.opExtrude","SWEPT_FACE",FACE,{"disambiguationData":[OSD([sQuery(id+"F55.wireOp",EDGE,"E344")])]})}),makeQuery(id+"F58.opExtrude","SWEPT_FACE",FACE,{"disambiguationData":[OSD([sQuery(id+"F57.wireOp",EDGE,"E359")])]}),makeQuery(id+"F58.opExtrude","SWEPT_FACE",FACE,{"disambiguationData":[OSD([sQuery(id+"F57.wireOp",EDGE,"E360")])]})])],"derivedFrom":makeQuery(id+"F25.boolean.opBoolean","COPY",EDGE,{"derivedFrom":makeQuery(id+"F25.opExtrude","CAP_EDGE",EDGE,{"disambiguationData":[OSD([subQ1])],"isStart":false})})});}
            var Q5;
            {var subQ0=sQuery(id+"F24.wireOp",EDGE,"E209");var subQ1=sQuery(id+"F24.wireOp",EDGE,"E227.trimOffspring");Q5=makeQuery(id+"F58.boolean.opBoolean","SPLIT",EDGE,{"disambiguationData":[TD([makeQuery(id+"F25.boolean.opBoolean","COPY",FACE,{"derivedFrom":makeQuery(id+"F25.opExtrude","CAP_FACE",FACE,{"disambiguationData":[OSD([sQuery(id+"F0.wireOp",EDGE,"E0.bottom"),sQuery(id+"F0.wireOp",EDGE,"E0.left"),sQuery(id+"F0.wireOp",EDGE,"E0.right"),sQuery(id+"F2.wireOp",EDGE,"E5.bottom"),sQuery(id+"F2.wireOp",EDGE,"E5.right"),sQuery(id+"F4.wireOp",EDGE,"E22.bottom"),sQuery(id+"F4.wireOp",EDGE,"E22.right"),sQuery(id+"F6.wireOp",EDGE,"E66.left"),sQuery(id+"F6.wireOp",EDGE,"E67.right"),sQuery(id+"F24.wireOp",EDGE,"E201"),sQuery(id+"F24.wireOp",EDGE,"E202"),sQuery(id+"F24.wireOp",EDGE,"E203"),sQuery(id+"F24.wireOp",EDGE,"E204"),sQuery(id+"F24.wireOp",EDGE,"E205"),sQuery(id+"F24.wireOp",EDGE,"E206"),sQuery(id+"F24.wireOp",EDGE,"E207"),sQuery(id+"F24.wireOp",EDGE,"E208"),subQ0,sQuery(id+"F24.wireOp",EDGE,"E210"),sQuery(id+"F24.wireOp",EDGE,"E211"),sQuery(id+"F24.wireOp",EDGE,"E212"),sQuery(id+"F24.wireOp",EDGE,"E213"),sQuery(id+"F24.wireOp",EDGE,"E214"),sQuery(id+"F24.wireOp",EDGE,"E215"),sQuery(id+"F24.wireOp",EDGE,"E216"),sQuery(id+"F24.wireOp",EDGE,"E217"),sQuery(id+"F24.wireOp",EDGE,"E218"),sQuery(id+"F24.wireOp",EDGE,"E219"),sQuery(id+"F24.wireOp",EDGE,"E220"),sQuery(id+"F24.wireOp",EDGE,"E221"),sQuery(id+"F24.wireOp",EDGE,"E222"),sQuery(id+"F24.wireOp",EDGE,"E223"),sQuery(id+"F24.wireOp",EDGE,"E224"),sQuery(id+"F24.wireOp",EDGE,"E225"),sQuery(id+"F24.wireOp",EDGE,"E226"),subQ1,sQuery(id+"F24.wireOp",EDGE,"E228.trimOffspring"),sQuery(id+"F24.wireOp",EDGE,"E229.trimOffspring"),sQuery(id+"F24.wireOp",EDGE,"E230.trimOffspring"),sQuery(id+"F24.wireOp",EDGE,"E231.trimOffspring"),sQuery(id+"F24.wireOp",EDGE,"E232.trimOffspring"),sQuery(id+"F24.wireOp",EDGE,"E233.trimOffspring")])],"isStart":false})}),makeQuery(id+"F25.boolean.opBoolean","COPY",FACE,{"derivedFrom":makeQuery(id+"F25.opExtrude","SWEPT_FACE",FACE,{"disambiguationData":[OSD([subQ0])]})}),makeQuery(id+"F25.boolean.opBoolean","COPY",FACE,{"derivedFrom":makeQuery(id+"F25.opExtrude","SWEPT_FACE",FACE,{"disambiguationData":[OSD([subQ1])]})}),makeQuery(id+"F27.opExtrude","SWEPT_FACE",FACE,{"disambiguationData":[OSD([sQuery(id+"F26.wireOp",EDGE,"E236")])]}),makeQuery(id+"F29.opExtrude","SWEPT_FACE",FACE,{"disambiguationData":[OSD([sQuery(id+"F28.wireOp",EDGE,"E240")])]}),makeQuery(id+"F31.opExtrude","SWEPT_FACE",FACE,{"disambiguationData":[OSD([sQuery(id+"F30.wireOp",EDGE,"E246")])]}),makeQuery(id+"F56.boolean.opBoolean","COPY",FACE,{"derivedFrom":makeQuery(id+"F56.opExtrude","SWEPT_FACE",FACE,{"disambiguationData":[OSD([sQuery(id+"F55.wireOp",EDGE,"E346")])]})}),makeQuery(id+"F58.opExtrude","SWEPT_FACE",FACE,{"disambiguationData":[OSD([sQuery(id+"F57.wireOp",EDGE,"E358")])]}),makeQuery(id+"F58.opExtrude","SWEPT_FACE",FACE,{"disambiguationData":[OSD([sQuery(id+"F57.wireOp",EDGE,"E359")])]})])],"derivedFrom":makeQuery(id+"F25.boolean.opBoolean","COPY",EDGE,{"derivedFrom":makeQuery(id+"F25.opExtrude","CAP_EDGE",EDGE,{"disambiguationData":[OSD([subQ1])],"isStart":false})})});}
            var Q6;
            {var subQ0=sQuery(id+"F6.wireOp",EDGE,"E92.trimOffspring");var subQ1=sQuery(id+"F6.wireOp",EDGE,"E84.right");var subQ2=sQuery(id+"F6.wireOp",EDGE,"E66.right");Q6=makeQuery(id+"F56.boolean.opBoolean","SPLIT",EDGE,{"disambiguationData":[TD([makeQuery(id+"F7.boolean.opBoolean","COPY",FACE,{"derivedFrom":makeQuery(id+"F7.opExtrude","CAP_FACE",FACE,{"disambiguationData":[OSD([sQuery(id+"F0.wireOp",EDGE,"E0.bottom"),sQuery(id+"F0.wireOp",EDGE,"E0.top"),sQuery(id+"F0.wireOp",EDGE,"E0.right"),sQuery(id+"F6.wireOp",EDGE,"E63.right"),sQuery(id+"F6.wireOp",EDGE,"E65.right"),sQuery(id+"F6.wireOp",EDGE,"E66.left"),subQ2,sQuery(id+"F6.wireOp",EDGE,"E67.right"),sQuery(id+"F6.wireOp",EDGE,"E68.top"),sQuery(id+"F6.wireOp",EDGE,"E68.right"),sQuery(id+"F6.wireOp",EDGE,"E69.left"),sQuery(id+"F6.wireOp",EDGE,"E69.right"),sQuery(id+"F6.wireOp",EDGE,"E70.bottom"),sQuery(id+"F6.wireOp",EDGE,"E70.top"),sQuery(id+"F6.wireOp",EDGE,"E71"),sQuery(id+"F6.wireOp",EDGE,"E72"),sQuery(id+"F6.wireOp",EDGE,"E76.trimOffspring"),sQuery(id+"F6.wireOp",EDGE,"E77.trimOffspring"),sQuery(id+"F6.wireOp",EDGE,"E78.trimOffspring"),sQuery(id+"F6.wireOp",EDGE,"E79.trimOffspring"),sQuery(id+"F6.wireOp",EDGE,"E80.trimOffspring"),sQuery(id+"F6.wireOp",EDGE,"E81.right"),sQuery(id+"F6.wireOp",EDGE,"E82.bottom"),sQuery(id+"F6.wireOp",EDGE,"E83.right"),sQuery(id+"F6.wireOp",EDGE,"E84.left"),subQ1,sQuery(id+"F6.wireOp",EDGE,"E85.top"),sQuery(id+"F6.wireOp",EDGE,"E85.right"),sQuery(id+"F6.wireOp",EDGE,"E86.right"),sQuery(id+"F6.wireOp",EDGE,"E87.left"),sQuery(id+"F6.wireOp",EDGE,"E87.right"),sQuery(id+"F6.wireOp",EDGE,"E88.bottom"),sQuery(id+"F6.wireOp",EDGE,"E88.top"),sQuery(id+"F6.wireOp",EDGE,"E90"),subQ0,sQuery(id+"F6.wireOp",EDGE,"E93.trimOffspring"),sQuery(id+"F6.wireOp",EDGE,"E94.trimOffspring"),sQuery(id+"F6.wireOp",EDGE,"E96.trimOffspring"),sQuery(id+"F6.wireOp",EDGE,"E100"),sQuery(id+"F6.wireOp",EDGE,"E101"),sQuery(id+"F6.wireOp",EDGE,"E102"),sQuery(id+"F6.wireOp",EDGE,"E103"),sQuery(id+"F6.wireOp",EDGE,"E104"),sQuery(id+"F6.wireOp",EDGE,"E105")])],"isStart":false})}),makeQuery(id+"F7.boolean.opBoolean","COPY",FACE,{"derivedFrom":makeQuery(id+"F7.opExtrude","SWEPT_FACE",FACE,{"disambiguationData":[OSD([subQ2,subQ1])]})}),makeQuery(id+"F7.boolean.opBoolean","COPY",FACE,{"derivedFrom":makeQuery(id+"F7.opExtrude","SWEPT_FACE",FACE,{"disambiguationData":[OSD([subQ0])]})}),makeQuery(id+"F15.opExtrude","SWEPT_FACE",FACE,{"disambiguationData":[OSD([sQuery(id+"F14.wireOp",EDGE,"E154")])]}),makeQuery(id+"F17.opExtrude","SWEPT_FACE",FACE,{"disambiguationData":[OSD([sQuery(id+"F16.wireOp",EDGE,"E157")])]}),makeQuery(id+"F56.opExtrude","SWEPT_FACE",FACE,{"disambiguationData":[OSD([sQuery(id+"F55.wireOp",EDGE,"E344")])]}),makeQuery(id+"F56.opExtrude","SWEPT_FACE",FACE,{"disambiguationData":[OSD([sQuery(id+"F55.wireOp",EDGE,"E345")])]})])],"derivedFrom":makeQuery(id+"F7.boolean.opBoolean","COPY",EDGE,{"derivedFrom":makeQuery(id+"F7.opExtrude","CAP_EDGE",EDGE,{"disambiguationData":[OSD([subQ0])],"isStart":false})})});}
            var Q7;
            {var subQ0=sQuery(id+"F6.wireOp",EDGE,"E92.trimOffspring");var subQ1=sQuery(id+"F6.wireOp",EDGE,"E84.left");var subQ2=sQuery(id+"F6.wireOp",EDGE,"E66.left");Q7=makeQuery(id+"F56.boolean.opBoolean","SPLIT",EDGE,{"disambiguationData":[TD([makeQuery(id+"F7.boolean.opBoolean","COPY",FACE,{"derivedFrom":makeQuery(id+"F7.opExtrude","CAP_FACE",FACE,{"disambiguationData":[OSD([sQuery(id+"F0.wireOp",EDGE,"E0.bottom"),sQuery(id+"F0.wireOp",EDGE,"E0.top"),sQuery(id+"F0.wireOp",EDGE,"E0.right"),sQuery(id+"F6.wireOp",EDGE,"E63.right"),sQuery(id+"F6.wireOp",EDGE,"E65.right"),subQ2,sQuery(id+"F6.wireOp",EDGE,"E66.right"),sQuery(id+"F6.wireOp",EDGE,"E67.right"),sQuery(id+"F6.wireOp",EDGE,"E68.top"),sQuery(id+"F6.wireOp",EDGE,"E68.right"),sQuery(id+"F6.wireOp",EDGE,"E69.left"),sQuery(id+"F6.wireOp",EDGE,"E69.right"),sQuery(id+"F6.wireOp",EDGE,"E70.bottom"),sQuery(id+"F6.wireOp",EDGE,"E70.top"),sQuery(id+"F6.wireOp",EDGE,"E71"),sQuery(id+"F6.wireOp",EDGE,"E72"),sQuery(id+"F6.wireOp",EDGE,"E76.trimOffspring"),sQuery(id+"F6.wireOp",EDGE,"E77.trimOffspring"),sQuery(id+"F6.wireOp",EDGE,"E78.trimOffspring"),sQuery(id+"F6.wireOp",EDGE,"E79.trimOffspring"),sQuery(id+"F6.wireOp",EDGE,"E80.trimOffspring"),sQuery(id+"F6.wireOp",EDGE,"E81.right"),sQuery(id+"F6.wireOp",EDGE,"E82.bottom"),sQuery(id+"F6.wireOp",EDGE,"E83.right"),subQ1,sQuery(id+"F6.wireOp",EDGE,"E84.right"),sQuery(id+"F6.wireOp",EDGE,"E85.top"),sQuery(id+"F6.wireOp",EDGE,"E85.right"),sQuery(id+"F6.wireOp",EDGE,"E86.right"),sQuery(id+"F6.wireOp",EDGE,"E87.left"),sQuery(id+"F6.wireOp",EDGE,"E87.right"),sQuery(id+"F6.wireOp",EDGE,"E88.bottom"),sQuery(id+"F6.wireOp",EDGE,"E88.top"),sQuery(id+"F6.wireOp",EDGE,"E90"),subQ0,sQuery(id+"F6.wireOp",EDGE,"E93.trimOffspring"),sQuery(id+"F6.wireOp",EDGE,"E94.trimOffspring"),sQuery(id+"F6.wireOp",EDGE,"E96.trimOffspring"),sQuery(id+"F6.wireOp",EDGE,"E100"),sQuery(id+"F6.wireOp",EDGE,"E101"),sQuery(id+"F6.wireOp",EDGE,"E102"),sQuery(id+"F6.wireOp",EDGE,"E103"),sQuery(id+"F6.wireOp",EDGE,"E104"),sQuery(id+"F6.wireOp",EDGE,"E105")])],"isStart":false})}),makeQuery(id+"F7.boolean.opBoolean","COPY",FACE,{"derivedFrom":makeQuery(id+"F7.opExtrude","SWEPT_FACE",FACE,{"disambiguationData":[OSD([subQ2,subQ1])]})}),makeQuery(id+"F7.boolean.opBoolean","COPY",FACE,{"derivedFrom":makeQuery(id+"F7.opExtrude","SWEPT_FACE",FACE,{"disambiguationData":[OSD([subQ0])]})}),makeQuery(id+"F15.opExtrude","SWEPT_FACE",FACE,{"disambiguationData":[OSD([sQuery(id+"F14.wireOp",EDGE,"E154")])]}),makeQuery(id+"F17.opExtrude","SWEPT_FACE",FACE,{"disambiguationData":[OSD([sQuery(id+"F16.wireOp",EDGE,"E157")])]}),makeQuery(id+"F56.opExtrude","SWEPT_FACE",FACE,{"disambiguationData":[OSD([sQuery(id+"F55.wireOp",EDGE,"E345")])]}),makeQuery(id+"F56.opExtrude","SWEPT_FACE",FACE,{"disambiguationData":[OSD([sQuery(id+"F55.wireOp",EDGE,"E346")])]})])],"derivedFrom":makeQuery(id+"F7.boolean.opBoolean","COPY",EDGE,{"derivedFrom":makeQuery(id+"F7.opExtrude","CAP_EDGE",EDGE,{"disambiguationData":[OSD([subQ0])],"isStart":false})})});}
            var Q8;
            {var subQ0=sQuery(id+"F24.wireOp",EDGE,"E229.trimOffspring");var subQ1=sQuery(id+"F24.wireOp",EDGE,"E217");Q8=makeQuery(id+"F58.boolean.opBoolean","SPLIT",EDGE,{"disambiguationData":[TD([makeQuery(id+"F25.boolean.opBoolean","COPY",FACE,{"derivedFrom":makeQuery(id+"F25.opExtrude","CAP_FACE",FACE,{"disambiguationData":[OSD([sQuery(id+"F0.wireOp",EDGE,"E0.bottom"),sQuery(id+"F0.wireOp",EDGE,"E0.left"),sQuery(id+"F0.wireOp",EDGE,"E0.right"),sQuery(id+"F2.wireOp",EDGE,"E5.bottom"),sQuery(id+"F2.wireOp",EDGE,"E5.right"),sQuery(id+"F4.wireOp",EDGE,"E22.bottom"),sQuery(id+"F4.wireOp",EDGE,"E22.right"),sQuery(id+"F6.wireOp",EDGE,"E66.left"),sQuery(id+"F6.wireOp",EDGE,"E67.right"),sQuery(id+"F24.wireOp",EDGE,"E201"),sQuery(id+"F24.wireOp",EDGE,"E202"),sQuery(id+"F24.wireOp",EDGE,"E203"),sQuery(id+"F24.wireOp",EDGE,"E204"),sQuery(id+"F24.wireOp",EDGE,"E205"),sQuery(id+"F24.wireOp",EDGE,"E206"),sQuery(id+"F24.wireOp",EDGE,"E207"),sQuery(id+"F24.wireOp",EDGE,"E208"),sQuery(id+"F24.wireOp",EDGE,"E209"),sQuery(id+"F24.wireOp",EDGE,"E210"),sQuery(id+"F24.wireOp",EDGE,"E211"),sQuery(id+"F24.wireOp",EDGE,"E212"),sQuery(id+"F24.wireOp",EDGE,"E213"),sQuery(id+"F24.wireOp",EDGE,"E214"),sQuery(id+"F24.wireOp",EDGE,"E215"),sQuery(id+"F24.wireOp",EDGE,"E216"),subQ1,sQuery(id+"F24.wireOp",EDGE,"E218"),sQuery(id+"F24.wireOp",EDGE,"E219"),sQuery(id+"F24.wireOp",EDGE,"E220"),sQuery(id+"F24.wireOp",EDGE,"E221"),sQuery(id+"F24.wireOp",EDGE,"E222"),sQuery(id+"F24.wireOp",EDGE,"E223"),sQuery(id+"F24.wireOp",EDGE,"E224"),sQuery(id+"F24.wireOp",EDGE,"E225"),sQuery(id+"F24.wireOp",EDGE,"E226"),sQuery(id+"F24.wireOp",EDGE,"E227.trimOffspring"),sQuery(id+"F24.wireOp",EDGE,"E228.trimOffspring"),subQ0,sQuery(id+"F24.wireOp",EDGE,"E230.trimOffspring"),sQuery(id+"F24.wireOp",EDGE,"E231.trimOffspring"),sQuery(id+"F24.wireOp",EDGE,"E232.trimOffspring"),sQuery(id+"F24.wireOp",EDGE,"E233.trimOffspring")])],"isStart":false})}),makeQuery(id+"F25.boolean.opBoolean","COPY",FACE,{"derivedFrom":makeQuery(id+"F25.opExtrude","SWEPT_FACE",FACE,{"disambiguationData":[OSD([subQ1])]})}),makeQuery(id+"F25.boolean.opBoolean","COPY",FACE,{"derivedFrom":makeQuery(id+"F25.opExtrude","SWEPT_FACE",FACE,{"disambiguationData":[OSD([subQ0])]})}),makeQuery(id+"F27.opExtrude","SWEPT_FACE",FACE,{"disambiguationData":[OSD([sQuery(id+"F26.wireOp",EDGE,"E236")])]}),makeQuery(id+"F27.opExtrude","SWEPT_FACE",FACE,{"disambiguationData":[OSD([sQuery(id+"F26.wireOp",EDGE,"E237")])]}),makeQuery(id+"F29.opExtrude","SWEPT_FACE",FACE,{"disambiguationData":[OSD([sQuery(id+"F28.wireOp",EDGE,"E240")])]}),makeQuery(id+"F31.opExtrude","SWEPT_FACE",FACE,{"disambiguationData":[OSD([sQuery(id+"F30.wireOp",EDGE,"E246")])]}),makeQuery(id+"F58.opExtrude","SWEPT_FACE",FACE,{"disambiguationData":[OSD([sQuery(id+"F57.wireOp",EDGE,"E364")])]}),makeQuery(id+"F58.opExtrude","SWEPT_FACE",FACE,{"disambiguationData":[OSD([sQuery(id+"F57.wireOp",EDGE,"E365")])]})])],"derivedFrom":makeQuery(id+"F25.boolean.opBoolean","COPY",EDGE,{"derivedFrom":makeQuery(id+"F25.opExtrude","CAP_EDGE",EDGE,{"disambiguationData":[OSD([subQ0])],"isStart":false})})});}
            var Q9;
            {var subQ0=sQuery(id+"F24.wireOp",EDGE,"E229.trimOffspring");var subQ1=sQuery(id+"F24.wireOp",EDGE,"E220");Q9=makeQuery(id+"F58.boolean.opBoolean","SPLIT",EDGE,{"disambiguationData":[TD([makeQuery(id+"F25.boolean.opBoolean","COPY",FACE,{"derivedFrom":makeQuery(id+"F25.opExtrude","CAP_FACE",FACE,{"disambiguationData":[OSD([sQuery(id+"F0.wireOp",EDGE,"E0.bottom"),sQuery(id+"F0.wireOp",EDGE,"E0.left"),sQuery(id+"F0.wireOp",EDGE,"E0.right"),sQuery(id+"F2.wireOp",EDGE,"E5.bottom"),sQuery(id+"F2.wireOp",EDGE,"E5.right"),sQuery(id+"F4.wireOp",EDGE,"E22.bottom"),sQuery(id+"F4.wireOp",EDGE,"E22.right"),sQuery(id+"F6.wireOp",EDGE,"E66.left"),sQuery(id+"F6.wireOp",EDGE,"E67.right"),sQuery(id+"F24.wireOp",EDGE,"E201"),sQuery(id+"F24.wireOp",EDGE,"E202"),sQuery(id+"F24.wireOp",EDGE,"E203"),sQuery(id+"F24.wireOp",EDGE,"E204"),sQuery(id+"F24.wireOp",EDGE,"E205"),sQuery(id+"F24.wireOp",EDGE,"E206"),sQuery(id+"F24.wireOp",EDGE,"E207"),sQuery(id+"F24.wireOp",EDGE,"E208"),sQuery(id+"F24.wireOp",EDGE,"E209"),sQuery(id+"F24.wireOp",EDGE,"E210"),sQuery(id+"F24.wireOp",EDGE,"E211"),sQuery(id+"F24.wireOp",EDGE,"E212"),sQuery(id+"F24.wireOp",EDGE,"E213"),sQuery(id+"F24.wireOp",EDGE,"E214"),sQuery(id+"F24.wireOp",EDGE,"E215"),sQuery(id+"F24.wireOp",EDGE,"E216"),sQuery(id+"F24.wireOp",EDGE,"E217"),sQuery(id+"F24.wireOp",EDGE,"E218"),sQuery(id+"F24.wireOp",EDGE,"E219"),subQ1,sQuery(id+"F24.wireOp",EDGE,"E221"),sQuery(id+"F24.wireOp",EDGE,"E222"),sQuery(id+"F24.wireOp",EDGE,"E223"),sQuery(id+"F24.wireOp",EDGE,"E224"),sQuery(id+"F24.wireOp",EDGE,"E225"),sQuery(id+"F24.wireOp",EDGE,"E226"),sQuery(id+"F24.wireOp",EDGE,"E227.trimOffspring"),sQuery(id+"F24.wireOp",EDGE,"E228.trimOffspring"),subQ0,sQuery(id+"F24.wireOp",EDGE,"E230.trimOffspring"),sQuery(id+"F24.wireOp",EDGE,"E231.trimOffspring"),sQuery(id+"F24.wireOp",EDGE,"E232.trimOffspring"),sQuery(id+"F24.wireOp",EDGE,"E233.trimOffspring")])],"isStart":false})}),makeQuery(id+"F25.boolean.opBoolean","COPY",FACE,{"derivedFrom":makeQuery(id+"F25.opExtrude","SWEPT_FACE",FACE,{"disambiguationData":[OSD([subQ1])]})}),makeQuery(id+"F25.boolean.opBoolean","COPY",FACE,{"derivedFrom":makeQuery(id+"F25.opExtrude","SWEPT_FACE",FACE,{"disambiguationData":[OSD([subQ0])]})}),makeQuery(id+"F27.opExtrude","SWEPT_FACE",FACE,{"disambiguationData":[OSD([sQuery(id+"F26.wireOp",EDGE,"E236")])]}),makeQuery(id+"F29.opExtrude","SWEPT_FACE",FACE,{"disambiguationData":[OSD([sQuery(id+"F28.wireOp",EDGE,"E240")])]}),makeQuery(id+"F29.opExtrude","SWEPT_FACE",FACE,{"disambiguationData":[OSD([sQuery(id+"F28.wireOp",EDGE,"E241")])]}),makeQuery(id+"F31.opExtrude","SWEPT_FACE",FACE,{"disambiguationData":[OSD([sQuery(id+"F30.wireOp",EDGE,"E246")])]}),makeQuery(id+"F58.opExtrude","SWEPT_FACE",FACE,{"disambiguationData":[OSD([sQuery(id+"F57.wireOp",EDGE,"E363")])]}),makeQuery(id+"F58.opExtrude","SWEPT_FACE",FACE,{"disambiguationData":[OSD([sQuery(id+"F57.wireOp",EDGE,"E364")])]})])],"derivedFrom":makeQuery(id+"F25.boolean.opBoolean","COPY",EDGE,{"derivedFrom":makeQuery(id+"F25.opExtrude","CAP_EDGE",EDGE,{"disambiguationData":[OSD([subQ0])],"isStart":false})})});}
            var Q10;
            {var subQ0=sQuery(id+"F24.wireOp",EDGE,"E233.trimOffspring");var subQ1=sQuery(id+"F24.wireOp",EDGE,"E205");Q10=makeQuery(id+"F58.boolean.opBoolean","SPLIT",EDGE,{"disambiguationData":[TD([makeQuery(id+"F25.boolean.opBoolean","COPY",FACE,{"derivedFrom":makeQuery(id+"F25.opExtrude","CAP_FACE",FACE,{"disambiguationData":[OSD([sQuery(id+"F0.wireOp",EDGE,"E0.bottom"),sQuery(id+"F0.wireOp",EDGE,"E0.left"),sQuery(id+"F0.wireOp",EDGE,"E0.right"),sQuery(id+"F2.wireOp",EDGE,"E5.bottom"),sQuery(id+"F2.wireOp",EDGE,"E5.right"),sQuery(id+"F4.wireOp",EDGE,"E22.bottom"),sQuery(id+"F4.wireOp",EDGE,"E22.right"),sQuery(id+"F6.wireOp",EDGE,"E66.left"),sQuery(id+"F6.wireOp",EDGE,"E67.right"),sQuery(id+"F24.wireOp",EDGE,"E201"),sQuery(id+"F24.wireOp",EDGE,"E202"),sQuery(id+"F24.wireOp",EDGE,"E203"),sQuery(id+"F24.wireOp",EDGE,"E204"),subQ1,sQuery(id+"F24.wireOp",EDGE,"E206"),sQuery(id+"F24.wireOp",EDGE,"E207"),sQuery(id+"F24.wireOp",EDGE,"E208"),sQuery(id+"F24.wireOp",EDGE,"E209"),sQuery(id+"F24.wireOp",EDGE,"E210"),sQuery(id+"F24.wireOp",EDGE,"E211"),sQuery(id+"F24.wireOp",EDGE,"E212"),sQuery(id+"F24.wireOp",EDGE,"E213"),sQuery(id+"F24.wireOp",EDGE,"E214"),sQuery(id+"F24.wireOp",EDGE,"E215"),sQuery(id+"F24.wireOp",EDGE,"E216"),sQuery(id+"F24.wireOp",EDGE,"E217"),sQuery(id+"F24.wireOp",EDGE,"E218"),sQuery(id+"F24.wireOp",EDGE,"E219"),sQuery(id+"F24.wireOp",EDGE,"E220"),sQuery(id+"F24.wireOp",EDGE,"E221"),sQuery(id+"F24.wireOp",EDGE,"E222"),sQuery(id+"F24.wireOp",EDGE,"E223"),sQuery(id+"F24.wireOp",EDGE,"E224"),sQuery(id+"F24.wireOp",EDGE,"E225"),sQuery(id+"F24.wireOp",EDGE,"E226"),sQuery(id+"F24.wireOp",EDGE,"E227.trimOffspring"),sQuery(id+"F24.wireOp",EDGE,"E228.trimOffspring"),sQuery(id+"F24.wireOp",EDGE,"E229.trimOffspring"),sQuery(id+"F24.wireOp",EDGE,"E230.trimOffspring"),sQuery(id+"F24.wireOp",EDGE,"E231.trimOffspring"),sQuery(id+"F24.wireOp",EDGE,"E232.trimOffspring"),subQ0])],"isStart":false})}),makeQuery(id+"F25.boolean.opBoolean","COPY",FACE,{"derivedFrom":makeQuery(id+"F25.opExtrude","SWEPT_FACE",FACE,{"disambiguationData":[OSD([subQ1])]})}),makeQuery(id+"F25.boolean.opBoolean","COPY",FACE,{"derivedFrom":makeQuery(id+"F25.opExtrude","SWEPT_FACE",FACE,{"disambiguationData":[OSD([subQ0])]})}),makeQuery(id+"F27.opExtrude","SWEPT_FACE",FACE,{"disambiguationData":[OSD([sQuery(id+"F26.wireOp",EDGE,"E236")])]}),makeQuery(id+"F29.opExtrude","SWEPT_FACE",FACE,{"disambiguationData":[OSD([sQuery(id+"F28.wireOp",EDGE,"E240")])]}),makeQuery(id+"F31.opExtrude","SWEPT_FACE",FACE,{"disambiguationData":[OSD([sQuery(id+"F30.wireOp",EDGE,"E246")])]}),makeQuery(id+"F58.opExtrude","SWEPT_FACE",FACE,{"disambiguationData":[OSD([sQuery(id+"F57.wireOp",EDGE,"E350")])]}),makeQuery(id+"F58.opExtrude","SWEPT_FACE",FACE,{"disambiguationData":[OSD([sQuery(id+"F57.wireOp",EDGE,"E351")])]})])],"derivedFrom":makeQuery(id+"F25.boolean.opBoolean","COPY",EDGE,{"derivedFrom":makeQuery(id+"F25.opExtrude","CAP_EDGE",EDGE,{"disambiguationData":[OSD([subQ0])],"isStart":false})})});}
            var Q11;
            {var subQ0=sQuery(id+"F24.wireOp",EDGE,"E233.trimOffspring");var subQ1=sQuery(id+"F24.wireOp",EDGE,"E208");Q11=makeQuery(id+"F58.boolean.opBoolean","SPLIT",EDGE,{"disambiguationData":[TD([makeQuery(id+"F25.boolean.opBoolean","COPY",FACE,{"derivedFrom":makeQuery(id+"F25.opExtrude","CAP_FACE",FACE,{"disambiguationData":[OSD([sQuery(id+"F0.wireOp",EDGE,"E0.bottom"),sQuery(id+"F0.wireOp",EDGE,"E0.left"),sQuery(id+"F0.wireOp",EDGE,"E0.right"),sQuery(id+"F2.wireOp",EDGE,"E5.bottom"),sQuery(id+"F2.wireOp",EDGE,"E5.right"),sQuery(id+"F4.wireOp",EDGE,"E22.bottom"),sQuery(id+"F4.wireOp",EDGE,"E22.right"),sQuery(id+"F6.wireOp",EDGE,"E66.left"),sQuery(id+"F6.wireOp",EDGE,"E67.right"),sQuery(id+"F24.wireOp",EDGE,"E201"),sQuery(id+"F24.wireOp",EDGE,"E202"),sQuery(id+"F24.wireOp",EDGE,"E203"),sQuery(id+"F24.wireOp",EDGE,"E204"),sQuery(id+"F24.wireOp",EDGE,"E205"),sQuery(id+"F24.wireOp",EDGE,"E206"),sQuery(id+"F24.wireOp",EDGE,"E207"),subQ1,sQuery(id+"F24.wireOp",EDGE,"E209"),sQuery(id+"F24.wireOp",EDGE,"E210"),sQuery(id+"F24.wireOp",EDGE,"E211"),sQuery(id+"F24.wireOp",EDGE,"E212"),sQuery(id+"F24.wireOp",EDGE,"E213"),sQuery(id+"F24.wireOp",EDGE,"E214"),sQuery(id+"F24.wireOp",EDGE,"E215"),sQuery(id+"F24.wireOp",EDGE,"E216"),sQuery(id+"F24.wireOp",EDGE,"E217"),sQuery(id+"F24.wireOp",EDGE,"E218"),sQuery(id+"F24.wireOp",EDGE,"E219"),sQuery(id+"F24.wireOp",EDGE,"E220"),sQuery(id+"F24.wireOp",EDGE,"E221"),sQuery(id+"F24.wireOp",EDGE,"E222"),sQuery(id+"F24.wireOp",EDGE,"E223"),sQuery(id+"F24.wireOp",EDGE,"E224"),sQuery(id+"F24.wireOp",EDGE,"E225"),sQuery(id+"F24.wireOp",EDGE,"E226"),sQuery(id+"F24.wireOp",EDGE,"E227.trimOffspring"),sQuery(id+"F24.wireOp",EDGE,"E228.trimOffspring"),sQuery(id+"F24.wireOp",EDGE,"E229.trimOffspring"),sQuery(id+"F24.wireOp",EDGE,"E230.trimOffspring"),sQuery(id+"F24.wireOp",EDGE,"E231.trimOffspring"),sQuery(id+"F24.wireOp",EDGE,"E232.trimOffspring"),subQ0])],"isStart":false})}),makeQuery(id+"F25.boolean.opBoolean","COPY",FACE,{"derivedFrom":makeQuery(id+"F25.opExtrude","SWEPT_FACE",FACE,{"disambiguationData":[OSD([subQ1])]})}),makeQuery(id+"F25.boolean.opBoolean","COPY",FACE,{"derivedFrom":makeQuery(id+"F25.opExtrude","SWEPT_FACE",FACE,{"disambiguationData":[OSD([subQ0])]})}),makeQuery(id+"F27.opExtrude","SWEPT_FACE",FACE,{"disambiguationData":[OSD([sQuery(id+"F26.wireOp",EDGE,"E236")])]}),makeQuery(id+"F29.opExtrude","SWEPT_FACE",FACE,{"disambiguationData":[OSD([sQuery(id+"F28.wireOp",EDGE,"E240")])]}),makeQuery(id+"F31.opExtrude","SWEPT_FACE",FACE,{"disambiguationData":[OSD([sQuery(id+"F30.wireOp",EDGE,"E243")])]}),makeQuery(id+"F31.opExtrude","SWEPT_FACE",FACE,{"disambiguationData":[OSD([sQuery(id+"F30.wireOp",EDGE,"E246")])]}),makeQuery(id+"F58.opExtrude","SWEPT_FACE",FACE,{"disambiguationData":[OSD([sQuery(id+"F57.wireOp",EDGE,"E349")])]}),makeQuery(id+"F58.opExtrude","SWEPT_FACE",FACE,{"disambiguationData":[OSD([sQuery(id+"F57.wireOp",EDGE,"E350")])]})])],"derivedFrom":makeQuery(id+"F25.boolean.opBoolean","COPY",EDGE,{"derivedFrom":makeQuery(id+"F25.opExtrude","CAP_EDGE",EDGE,{"disambiguationData":[OSD([subQ0])],"isStart":false})})});}
            var Q12;
            {var subQ0=sQuery(id+"F8.wireOp",EDGE,"E136.trimOffspring");var subQ1=sQuery(id+"F8.wireOp",EDGE,"E119");Q12=makeQuery(id+"F50.boolean.opBoolean","SPLIT",EDGE,{"disambiguationData":[TD([makeQuery(id+"F9.boolean.opBoolean","COPY",FACE,{"derivedFrom":makeQuery(id+"F9.opExtrude","CAP_FACE",FACE,{"disambiguationData":[OSD([sQuery(id+"F0.wireOp",EDGE,"E0.top"),sQuery(id+"F0.wireOp",EDGE,"E0.right"),sQuery(id+"F6.wireOp",EDGE,"E68.top"),sQuery(id+"F6.wireOp",EDGE,"E70.bottom"),sQuery(id+"F8.wireOp",EDGE,"E106"),sQuery(id+"F8.wireOp",EDGE,"E107"),sQuery(id+"F8.wireOp",EDGE,"E110"),sQuery(id+"F8.wireOp",EDGE,"E111"),sQuery(id+"F8.wireOp",EDGE,"E112"),sQuery(id+"F8.wireOp",EDGE,"E114"),sQuery(id+"F8.wireOp",EDGE,"E117"),sQuery(id+"F8.wireOp",EDGE,"E118"),subQ1,sQuery(id+"F8.wireOp",EDGE,"E120"),sQuery(id+"F8.wireOp",EDGE,"E121"),sQuery(id+"F8.wireOp",EDGE,"E123"),sQuery(id+"F8.wireOp",EDGE,"E124"),sQuery(id+"F8.wireOp",EDGE,"E125"),sQuery(id+"F8.wireOp",EDGE,"E126"),sQuery(id+"F8.wireOp",EDGE,"E127"),sQuery(id+"F8.wireOp",EDGE,"E128"),sQuery(id+"F8.wireOp",EDGE,"E129"),sQuery(id+"F8.wireOp",EDGE,"E130"),sQuery(id+"F8.wireOp",EDGE,"E131"),sQuery(id+"F8.wireOp",EDGE,"E132"),sQuery(id+"F8.wireOp",EDGE,"E133"),sQuery(id+"F8.wireOp",EDGE,"E134"),sQuery(id+"F8.wireOp",EDGE,"E135"),subQ0,sQuery(id+"F8.wireOp",EDGE,"E137.trimOffspring"),sQuery(id+"F8.wireOp",EDGE,"E138.trimOffspring"),sQuery(id+"F8.wireOp",EDGE,"E139.trimOffspring"),sQuery(id+"F8.wireOp",EDGE,"E140.trimOffspring"),sQuery(id+"F8.wireOp",EDGE,"E141.trimOffspring"),sQuery(id+"F8.wireOp",EDGE,"E142.trimOffspring")])],"isStart":false})}),makeQuery(id+"F9.boolean.opBoolean","COPY",FACE,{"derivedFrom":makeQuery(id+"F9.opExtrude","SWEPT_FACE",FACE,{"disambiguationData":[OSD([subQ1])]})}),makeQuery(id+"F9.boolean.opBoolean","COPY",FACE,{"derivedFrom":makeQuery(id+"F9.opExtrude","SWEPT_FACE",FACE,{"disambiguationData":[OSD([subQ0])]})}),makeQuery(id+"F11.opExtrude","SWEPT_FACE",FACE,{"disambiguationData":[OSD([sQuery(id+"F10.wireOp",EDGE,"E146")])]}),makeQuery(id+"F13.opExtrude","SWEPT_FACE",FACE,{"disambiguationData":[OSD([sQuery(id+"F12.wireOp",EDGE,"E150")])]}),makeQuery(id+"F19.opExtrude","SWEPT_FACE",FACE,{"disambiguationData":[OSD([sQuery(id+"F18.wireOp",EDGE,"E160")])]}),makeQuery(id+"F19.opExtrude","SWEPT_FACE",FACE,{"disambiguationData":[OSD([sQuery(id+"F18.wireOp",EDGE,"E161")])]}),makeQuery(id+"F21.opExtrude","SWEPT_FACE",FACE,{"disambiguationData":[OSD([sQuery(id+"F20.wireOp",EDGE,"E164")])]}),makeQuery(id+"F50.opExtrude","SWEPT_FACE",FACE,{"disambiguationData":[OSD([sQuery(id+"F49.wireOp",EDGE,"E271")])]}),makeQuery(id+"F50.opExtrude","SWEPT_FACE",FACE,{"disambiguationData":[OSD([sQuery(id+"F49.wireOp",EDGE,"E272")])]})])],"derivedFrom":makeQuery(id+"F9.boolean.opBoolean","COPY",EDGE,{"derivedFrom":makeQuery(id+"F9.opExtrude","CAP_EDGE",EDGE,{"disambiguationData":[OSD([subQ0])],"isStart":false})})});}
            var Q13;
            {var subQ0=sQuery(id+"F8.wireOp",EDGE,"E136.trimOffspring");var subQ1=sQuery(id+"F8.wireOp",EDGE,"E121");Q13=makeQuery(id+"F50.boolean.opBoolean","SPLIT",EDGE,{"disambiguationData":[TD([makeQuery(id+"F9.boolean.opBoolean","COPY",FACE,{"derivedFrom":makeQuery(id+"F9.opExtrude","CAP_FACE",FACE,{"disambiguationData":[OSD([sQuery(id+"F0.wireOp",EDGE,"E0.top"),sQuery(id+"F0.wireOp",EDGE,"E0.right"),sQuery(id+"F6.wireOp",EDGE,"E68.top"),sQuery(id+"F6.wireOp",EDGE,"E70.bottom"),sQuery(id+"F8.wireOp",EDGE,"E106"),sQuery(id+"F8.wireOp",EDGE,"E107"),sQuery(id+"F8.wireOp",EDGE,"E110"),sQuery(id+"F8.wireOp",EDGE,"E111"),sQuery(id+"F8.wireOp",EDGE,"E112"),sQuery(id+"F8.wireOp",EDGE,"E114"),sQuery(id+"F8.wireOp",EDGE,"E117"),sQuery(id+"F8.wireOp",EDGE,"E118"),sQuery(id+"F8.wireOp",EDGE,"E119"),sQuery(id+"F8.wireOp",EDGE,"E120"),subQ1,sQuery(id+"F8.wireOp",EDGE,"E123"),sQuery(id+"F8.wireOp",EDGE,"E124"),sQuery(id+"F8.wireOp",EDGE,"E125"),sQuery(id+"F8.wireOp",EDGE,"E126"),sQuery(id+"F8.wireOp",EDGE,"E127"),sQuery(id+"F8.wireOp",EDGE,"E128"),sQuery(id+"F8.wireOp",EDGE,"E129"),sQuery(id+"F8.wireOp",EDGE,"E130"),sQuery(id+"F8.wireOp",EDGE,"E131"),sQuery(id+"F8.wireOp",EDGE,"E132"),sQuery(id+"F8.wireOp",EDGE,"E133"),sQuery(id+"F8.wireOp",EDGE,"E134"),sQuery(id+"F8.wireOp",EDGE,"E135"),subQ0,sQuery(id+"F8.wireOp",EDGE,"E137.trimOffspring"),sQuery(id+"F8.wireOp",EDGE,"E138.trimOffspring"),sQuery(id+"F8.wireOp",EDGE,"E139.trimOffspring"),sQuery(id+"F8.wireOp",EDGE,"E140.trimOffspring"),sQuery(id+"F8.wireOp",EDGE,"E141.trimOffspring"),sQuery(id+"F8.wireOp",EDGE,"E142.trimOffspring")])],"isStart":false})}),makeQuery(id+"F9.boolean.opBoolean","COPY",FACE,{"derivedFrom":makeQuery(id+"F9.opExtrude","SWEPT_FACE",FACE,{"disambiguationData":[OSD([subQ1])]})}),makeQuery(id+"F9.boolean.opBoolean","COPY",FACE,{"derivedFrom":makeQuery(id+"F9.opExtrude","SWEPT_FACE",FACE,{"disambiguationData":[OSD([subQ0])]})}),makeQuery(id+"F11.opExtrude","SWEPT_FACE",FACE,{"disambiguationData":[OSD([sQuery(id+"F10.wireOp",EDGE,"E146")])]}),makeQuery(id+"F13.opExtrude","SWEPT_FACE",FACE,{"disambiguationData":[OSD([sQuery(id+"F12.wireOp",EDGE,"E150")])]}),makeQuery(id+"F19.opExtrude","SWEPT_FACE",FACE,{"disambiguationData":[OSD([sQuery(id+"F18.wireOp",EDGE,"E160")])]}),makeQuery(id+"F21.opExtrude","SWEPT_FACE",FACE,{"disambiguationData":[OSD([sQuery(id+"F20.wireOp",EDGE,"E163")])]}),makeQuery(id+"F21.opExtrude","SWEPT_FACE",FACE,{"disambiguationData":[OSD([sQuery(id+"F20.wireOp",EDGE,"E164")])]}),makeQuery(id+"F50.opExtrude","SWEPT_FACE",FACE,{"disambiguationData":[OSD([sQuery(id+"F49.wireOp",EDGE,"E272")])]}),makeQuery(id+"F50.opExtrude","SWEPT_FACE",FACE,{"disambiguationData":[OSD([sQuery(id+"F49.wireOp",EDGE,"E273")])]})])],"derivedFrom":makeQuery(id+"F9.boolean.opBoolean","COPY",EDGE,{"derivedFrom":makeQuery(id+"F9.opExtrude","CAP_EDGE",EDGE,{"disambiguationData":[OSD([subQ0])],"isStart":false})})});}
            var Q14;
            {var subQ0=sQuery(id+"F4.wireOp",EDGE,"E48.trimOffspring");var subQ1=sQuery(id+"F4.wireOp",EDGE,"E40.right");var subQ2=sQuery(id+"F4.wireOp",EDGE,"E22.right");Q14=makeQuery(id+"F54.boolean.opBoolean","SPLIT",EDGE,{"disambiguationData":[TD([makeQuery(id+"F5.boolean.opBoolean","COPY",FACE,{"derivedFrom":makeQuery(id+"F5.opExtrude","CAP_FACE",FACE,{"disambiguationData":[OSD([sQuery(id+"F0.wireOp",EDGE,"E0.bottom"),sQuery(id+"F0.wireOp",EDGE,"E0.top"),sQuery(id+"F0.wireOp",EDGE,"E0.right"),sQuery(id+"F4.wireOp",EDGE,"E19.right"),sQuery(id+"F4.wireOp",EDGE,"E21.right"),sQuery(id+"F4.wireOp",EDGE,"E22.left"),subQ2,sQuery(id+"F4.wireOp",EDGE,"E23.right"),sQuery(id+"F4.wireOp",EDGE,"E24.top"),sQuery(id+"F4.wireOp",EDGE,"E24.right"),sQuery(id+"F4.wireOp",EDGE,"E25.left"),sQuery(id+"F4.wireOp",EDGE,"E25.right"),sQuery(id+"F4.wireOp",EDGE,"E26.bottom"),sQuery(id+"F4.wireOp",EDGE,"E26.top"),sQuery(id+"F4.wireOp",EDGE,"E27"),sQuery(id+"F4.wireOp",EDGE,"E28"),sQuery(id+"F4.wireOp",EDGE,"E32.trimOffspring"),sQuery(id+"F4.wireOp",EDGE,"E33.trimOffspring"),sQuery(id+"F4.wireOp",EDGE,"E34.trimOffspring"),sQuery(id+"F4.wireOp",EDGE,"E35.trimOffspring"),sQuery(id+"F4.wireOp",EDGE,"E36.trimOffspring"),sQuery(id+"F4.wireOp",EDGE,"E37.right"),sQuery(id+"F4.wireOp",EDGE,"E38.bottom"),sQuery(id+"F4.wireOp",EDGE,"E39.right"),sQuery(id+"F4.wireOp",EDGE,"E40.left"),subQ1,sQuery(id+"F4.wireOp",EDGE,"E41.top"),sQuery(id+"F4.wireOp",EDGE,"E41.right"),sQuery(id+"F4.wireOp",EDGE,"E42.right"),sQuery(id+"F4.wireOp",EDGE,"E43.left"),sQuery(id+"F4.wireOp",EDGE,"E43.right"),sQuery(id+"F4.wireOp",EDGE,"E44.bottom"),sQuery(id+"F4.wireOp",EDGE,"E44.top"),sQuery(id+"F4.wireOp",EDGE,"E46"),subQ0,sQuery(id+"F4.wireOp",EDGE,"E49.trimOffspring"),sQuery(id+"F4.wireOp",EDGE,"E50.trimOffspring"),sQuery(id+"F4.wireOp",EDGE,"E52.trimOffspring"),sQuery(id+"F4.wireOp",EDGE,"E56"),sQuery(id+"F4.wireOp",EDGE,"E57"),sQuery(id+"F4.wireOp",EDGE,"E58"),sQuery(id+"F4.wireOp",EDGE,"E59"),sQuery(id+"F4.wireOp",EDGE,"E60"),sQuery(id+"F4.wireOp",EDGE,"E61")])],"isStart":false})}),makeQuery(id+"F5.boolean.opBoolean","COPY",FACE,{"derivedFrom":makeQuery(id+"F5.opExtrude","SWEPT_FACE",FACE,{"disambiguationData":[OSD([subQ2,subQ1])]})}),makeQuery(id+"F5.boolean.opBoolean","COPY",FACE,{"derivedFrom":makeQuery(id+"F5.opExtrude","SWEPT_FACE",FACE,{"disambiguationData":[OSD([subQ0])]})}),makeQuery(id+"F54.opExtrude","SWEPT_FACE",FACE,{"disambiguationData":[OSD([sQuery(id+"F53.wireOp",EDGE,"E309")])]}),makeQuery(id+"F54.opExtrude","SWEPT_FACE",FACE,{"disambiguationData":[OSD([sQuery(id+"F53.wireOp",EDGE,"E328")])]})])],"derivedFrom":makeQuery(id+"F5.boolean.opBoolean","COPY",EDGE,{"derivedFrom":makeQuery(id+"F5.opExtrude","CAP_EDGE",EDGE,{"disambiguationData":[OSD([subQ0])],"isStart":false})})});}
            var Q15;
            {var subQ0=sQuery(id+"F4.wireOp",EDGE,"E48.trimOffspring");var subQ1=sQuery(id+"F4.wireOp",EDGE,"E40.left");var subQ2=sQuery(id+"F4.wireOp",EDGE,"E22.left");Q15=makeQuery(id+"F54.boolean.opBoolean","SPLIT",EDGE,{"disambiguationData":[TD([makeQuery(id+"F5.boolean.opBoolean","COPY",FACE,{"derivedFrom":makeQuery(id+"F5.opExtrude","CAP_FACE",FACE,{"disambiguationData":[OSD([sQuery(id+"F0.wireOp",EDGE,"E0.bottom"),sQuery(id+"F0.wireOp",EDGE,"E0.top"),sQuery(id+"F0.wireOp",EDGE,"E0.right"),sQuery(id+"F4.wireOp",EDGE,"E19.right"),sQuery(id+"F4.wireOp",EDGE,"E21.right"),subQ2,sQuery(id+"F4.wireOp",EDGE,"E22.right"),sQuery(id+"F4.wireOp",EDGE,"E23.right"),sQuery(id+"F4.wireOp",EDGE,"E24.top"),sQuery(id+"F4.wireOp",EDGE,"E24.right"),sQuery(id+"F4.wireOp",EDGE,"E25.left"),sQuery(id+"F4.wireOp",EDGE,"E25.right"),sQuery(id+"F4.wireOp",EDGE,"E26.bottom"),sQuery(id+"F4.wireOp",EDGE,"E26.top"),sQuery(id+"F4.wireOp",EDGE,"E27"),sQuery(id+"F4.wireOp",EDGE,"E28"),sQuery(id+"F4.wireOp",EDGE,"E32.trimOffspring"),sQuery(id+"F4.wireOp",EDGE,"E33.trimOffspring"),sQuery(id+"F4.wireOp",EDGE,"E34.trimOffspring"),sQuery(id+"F4.wireOp",EDGE,"E35.trimOffspring"),sQuery(id+"F4.wireOp",EDGE,"E36.trimOffspring"),sQuery(id+"F4.wireOp",EDGE,"E37.right"),sQuery(id+"F4.wireOp",EDGE,"E38.bottom"),sQuery(id+"F4.wireOp",EDGE,"E39.right"),subQ1,sQuery(id+"F4.wireOp",EDGE,"E40.right"),sQuery(id+"F4.wireOp",EDGE,"E41.top"),sQuery(id+"F4.wireOp",EDGE,"E41.right"),sQuery(id+"F4.wireOp",EDGE,"E42.right"),sQuery(id+"F4.wireOp",EDGE,"E43.left"),sQuery(id+"F4.wireOp",EDGE,"E43.right"),sQuery(id+"F4.wireOp",EDGE,"E44.bottom"),sQuery(id+"F4.wireOp",EDGE,"E44.top"),sQuery(id+"F4.wireOp",EDGE,"E46"),subQ0,sQuery(id+"F4.wireOp",EDGE,"E49.trimOffspring"),sQuery(id+"F4.wireOp",EDGE,"E50.trimOffspring"),sQuery(id+"F4.wireOp",EDGE,"E52.trimOffspring"),sQuery(id+"F4.wireOp",EDGE,"E56"),sQuery(id+"F4.wireOp",EDGE,"E57"),sQuery(id+"F4.wireOp",EDGE,"E58"),sQuery(id+"F4.wireOp",EDGE,"E59"),sQuery(id+"F4.wireOp",EDGE,"E60"),sQuery(id+"F4.wireOp",EDGE,"E61")])],"isStart":false})}),makeQuery(id+"F5.boolean.opBoolean","COPY",FACE,{"derivedFrom":makeQuery(id+"F5.opExtrude","SWEPT_FACE",FACE,{"disambiguationData":[OSD([subQ2,subQ1])]})}),makeQuery(id+"F5.boolean.opBoolean","COPY",FACE,{"derivedFrom":makeQuery(id+"F5.opExtrude","SWEPT_FACE",FACE,{"disambiguationData":[OSD([subQ0])]})}),makeQuery(id+"F54.opExtrude","SWEPT_FACE",FACE,{"disambiguationData":[OSD([sQuery(id+"F53.wireOp",EDGE,"E310")])]}),makeQuery(id+"F54.opExtrude","SWEPT_FACE",FACE,{"disambiguationData":[OSD([sQuery(id+"F53.wireOp",EDGE,"E328")])]})])],"derivedFrom":makeQuery(id+"F5.boolean.opBoolean","COPY",EDGE,{"derivedFrom":makeQuery(id+"F5.opExtrude","CAP_EDGE",EDGE,{"disambiguationData":[OSD([subQ0])],"isStart":false})})});}
            var Q16;
            Q16=makeQuery(id+"F5.boolean.opBoolean","COPY",EDGE,{"derivedFrom":makeQuery(id+"F5.opExtrude","CAP_EDGE",EDGE,{"disambiguationData":[OSD([sQuery(id+"F4.wireOp",EDGE,"E36.trimOffspring")])],"isStart":false})});
            var Q17;
            {var subQ0=sQuery(id+"F2.wireOp",EDGE,"E18.trimOffspring");var subQ1=sQuery(id+"F2.wireOp",EDGE,"E7.right");Q17=makeQuery(id+"F52.boolean.opBoolean","SPLIT",EDGE,{"disambiguationData":[TD([makeQuery(id+"F3.boolean.opBoolean","COPY",FACE,{"derivedFrom":makeQuery(id+"F3.opExtrude","CAP_FACE",FACE,{"disambiguationData":[OSD([sQuery(id+"F0.wireOp",EDGE,"E0.bottom"),sQuery(id+"F0.wireOp",EDGE,"E0.top"),sQuery(id+"F0.wireOp",EDGE,"E0.left"),sQuery(id+"F2.wireOp",EDGE,"E1.top"),sQuery(id+"F2.wireOp",EDGE,"E1.right"),sQuery(id+"F2.wireOp",EDGE,"E2.bottom"),sQuery(id+"F2.wireOp",EDGE,"E2.top"),sQuery(id+"F2.wireOp",EDGE,"E3.top"),sQuery(id+"F2.wireOp",EDGE,"E3.right"),sQuery(id+"F2.wireOp",EDGE,"E4.left"),sQuery(id+"F2.wireOp",EDGE,"E4.right"),sQuery(id+"F2.wireOp",EDGE,"E5.top"),sQuery(id+"F2.wireOp",EDGE,"E5.right"),sQuery(id+"F2.wireOp",EDGE,"E6.top"),sQuery(id+"F2.wireOp",EDGE,"E6.right"),sQuery(id+"F2.wireOp",EDGE,"E7.left"),subQ1,sQuery(id+"F2.wireOp",EDGE,"E8.bottom"),sQuery(id+"F2.wireOp",EDGE,"E8.top"),sQuery(id+"F2.wireOp",EDGE,"E9"),sQuery(id+"F2.wireOp",EDGE,"E10"),sQuery(id+"F2.wireOp",EDGE,"E12.trimOffspring"),sQuery(id+"F2.wireOp",EDGE,"E13.trimOffspring"),sQuery(id+"F2.wireOp",EDGE,"E14.trimOffspring"),sQuery(id+"F2.wireOp",EDGE,"E15.trimOffspring"),sQuery(id+"F2.wireOp",EDGE,"E16.trimOffspring"),sQuery(id+"F2.wireOp",EDGE,"E17.trimOffspring"),subQ0])],"isStart":false})}),makeQuery(id+"F3.boolean.opBoolean","COPY",FACE,{"derivedFrom":makeQuery(id+"F3.opExtrude","SWEPT_FACE",FACE,{"disambiguationData":[OSD([subQ1])]})}),makeQuery(id+"F3.boolean.opBoolean","COPY",FACE,{"derivedFrom":makeQuery(id+"F3.opExtrude","SWEPT_FACE",FACE,{"disambiguationData":[OSD([subQ0])]})}),makeQuery(id+"F52.opExtrude","SWEPT_FACE",FACE,{"disambiguationData":[OSD([sQuery(id+"F51.wireOp",EDGE,"E293")])]}),makeQuery(id+"F52.opExtrude","SWEPT_FACE",FACE,{"disambiguationData":[OSD([sQuery(id+"F51.wireOp",EDGE,"E307")])]})])],"derivedFrom":makeQuery(id+"F3.boolean.opBoolean","COPY",EDGE,{"derivedFrom":makeQuery(id+"F3.opExtrude","CAP_EDGE",EDGE,{"disambiguationData":[OSD([subQ0])],"isStart":false})})});}
            var Q18;
            {var subQ0=sQuery(id+"F2.wireOp",EDGE,"E18.trimOffspring");var subQ1=sQuery(id+"F2.wireOp",EDGE,"E7.left");Q18=makeQuery(id+"F52.boolean.opBoolean","SPLIT",EDGE,{"disambiguationData":[TD([makeQuery(id+"F3.boolean.opBoolean","COPY",FACE,{"derivedFrom":makeQuery(id+"F3.opExtrude","CAP_FACE",FACE,{"disambiguationData":[OSD([sQuery(id+"F0.wireOp",EDGE,"E0.bottom"),sQuery(id+"F0.wireOp",EDGE,"E0.top"),sQuery(id+"F0.wireOp",EDGE,"E0.left"),sQuery(id+"F2.wireOp",EDGE,"E1.top"),sQuery(id+"F2.wireOp",EDGE,"E1.right"),sQuery(id+"F2.wireOp",EDGE,"E2.bottom"),sQuery(id+"F2.wireOp",EDGE,"E2.top"),sQuery(id+"F2.wireOp",EDGE,"E3.top"),sQuery(id+"F2.wireOp",EDGE,"E3.right"),sQuery(id+"F2.wireOp",EDGE,"E4.left"),sQuery(id+"F2.wireOp",EDGE,"E4.right"),sQuery(id+"F2.wireOp",EDGE,"E5.top"),sQuery(id+"F2.wireOp",EDGE,"E5.right"),sQuery(id+"F2.wireOp",EDGE,"E6.top"),sQuery(id+"F2.wireOp",EDGE,"E6.right"),subQ1,sQuery(id+"F2.wireOp",EDGE,"E7.right"),sQuery(id+"F2.wireOp",EDGE,"E8.bottom"),sQuery(id+"F2.wireOp",EDGE,"E8.top"),sQuery(id+"F2.wireOp",EDGE,"E9"),sQuery(id+"F2.wireOp",EDGE,"E10"),sQuery(id+"F2.wireOp",EDGE,"E12.trimOffspring"),sQuery(id+"F2.wireOp",EDGE,"E13.trimOffspring"),sQuery(id+"F2.wireOp",EDGE,"E14.trimOffspring"),sQuery(id+"F2.wireOp",EDGE,"E15.trimOffspring"),sQuery(id+"F2.wireOp",EDGE,"E16.trimOffspring"),sQuery(id+"F2.wireOp",EDGE,"E17.trimOffspring"),subQ0])],"isStart":false})}),makeQuery(id+"F3.boolean.opBoolean","COPY",FACE,{"derivedFrom":makeQuery(id+"F3.opExtrude","SWEPT_FACE",FACE,{"disambiguationData":[OSD([subQ1])]})}),makeQuery(id+"F3.boolean.opBoolean","COPY",FACE,{"derivedFrom":makeQuery(id+"F3.opExtrude","SWEPT_FACE",FACE,{"disambiguationData":[OSD([subQ0])]})}),makeQuery(id+"F52.opExtrude","SWEPT_FACE",FACE,{"disambiguationData":[OSD([sQuery(id+"F51.wireOp",EDGE,"E291")])]}),makeQuery(id+"F52.opExtrude","SWEPT_FACE",FACE,{"disambiguationData":[OSD([sQuery(id+"F51.wireOp",EDGE,"E307")])]})])],"derivedFrom":makeQuery(id+"F3.boolean.opBoolean","COPY",EDGE,{"derivedFrom":makeQuery(id+"F3.opExtrude","CAP_EDGE",EDGE,{"disambiguationData":[OSD([subQ0])],"isStart":false})})});}
            var Q19;
            {var subQ0=sQuery(id+"F8.wireOp",EDGE,"E140.trimOffspring");var subQ1=sQuery(id+"F8.wireOp",EDGE,"E123");Q19=makeQuery(id+"F50.boolean.opBoolean","SPLIT",EDGE,{"disambiguationData":[TD([makeQuery(id+"F9.boolean.opBoolean","COPY",FACE,{"derivedFrom":makeQuery(id+"F9.opExtrude","SWEPT_FACE",FACE,{"disambiguationData":[OSD([subQ1])]})})])],"derivedFrom":makeQuery(id+"F9.boolean.opBoolean","COPY",EDGE,{"derivedFrom":makeQuery(id+"F9.opExtrude","CAP_EDGE",EDGE,{"disambiguationData":[OSD([subQ0])],"isStart":false})})});}
            var Q20;
            {var subQ0=sQuery(id+"F8.wireOp",EDGE,"E140.trimOffspring");var subQ1=sQuery(id+"F8.wireOp",EDGE,"E117");Q20=makeQuery(id+"F50.boolean.opBoolean","SPLIT",EDGE,{"disambiguationData":[TD([makeQuery(id+"F9.boolean.opBoolean","COPY",FACE,{"derivedFrom":makeQuery(id+"F9.opExtrude","SWEPT_FACE",FACE,{"disambiguationData":[OSD([subQ1])]})})])],"derivedFrom":makeQuery(id+"F9.boolean.opBoolean","COPY",EDGE,{"derivedFrom":makeQuery(id+"F9.opExtrude","CAP_EDGE",EDGE,{"disambiguationData":[OSD([subQ0])],"isStart":false})})});}
            var Q21;
            {var subQ0=sQuery(id+"F6.wireOp",EDGE,"E87.left");var subQ1=sQuery(id+"F6.wireOp",EDGE,"E69.left");var subQ2=sQuery(id+"F6.wireOp",EDGE,"E80.trimOffspring");Q21=makeQuery(id+"F56.boolean.opBoolean","SPLIT",EDGE,{"disambiguationData":[TD([makeQuery(id+"F7.boolean.opBoolean","COPY",FACE,{"derivedFrom":makeQuery(id+"F7.opExtrude","CAP_FACE",FACE,{"disambiguationData":[OSD([sQuery(id+"F0.wireOp",EDGE,"E0.bottom"),sQuery(id+"F0.wireOp",EDGE,"E0.top"),sQuery(id+"F0.wireOp",EDGE,"E0.right"),sQuery(id+"F6.wireOp",EDGE,"E63.right"),sQuery(id+"F6.wireOp",EDGE,"E65.right"),sQuery(id+"F6.wireOp",EDGE,"E66.left"),sQuery(id+"F6.wireOp",EDGE,"E66.right"),sQuery(id+"F6.wireOp",EDGE,"E67.right"),sQuery(id+"F6.wireOp",EDGE,"E68.top"),sQuery(id+"F6.wireOp",EDGE,"E68.right"),subQ1,sQuery(id+"F6.wireOp",EDGE,"E69.right"),sQuery(id+"F6.wireOp",EDGE,"E70.bottom"),sQuery(id+"F6.wireOp",EDGE,"E70.top"),sQuery(id+"F6.wireOp",EDGE,"E71"),sQuery(id+"F6.wireOp",EDGE,"E72"),sQuery(id+"F6.wireOp",EDGE,"E76.trimOffspring"),sQuery(id+"F6.wireOp",EDGE,"E77.trimOffspring"),sQuery(id+"F6.wireOp",EDGE,"E78.trimOffspring"),sQuery(id+"F6.wireOp",EDGE,"E79.trimOffspring"),subQ2,sQuery(id+"F6.wireOp",EDGE,"E81.right"),sQuery(id+"F6.wireOp",EDGE,"E82.bottom"),sQuery(id+"F6.wireOp",EDGE,"E83.right"),sQuery(id+"F6.wireOp",EDGE,"E84.left"),sQuery(id+"F6.wireOp",EDGE,"E84.right"),sQuery(id+"F6.wireOp",EDGE,"E85.top"),sQuery(id+"F6.wireOp",EDGE,"E85.right"),sQuery(id+"F6.wireOp",EDGE,"E86.right"),subQ0,sQuery(id+"F6.wireOp",EDGE,"E87.right"),sQuery(id+"F6.wireOp",EDGE,"E88.bottom"),sQuery(id+"F6.wireOp",EDGE,"E88.top"),sQuery(id+"F6.wireOp",EDGE,"E90"),sQuery(id+"F6.wireOp",EDGE,"E92.trimOffspring"),sQuery(id+"F6.wireOp",EDGE,"E93.trimOffspring"),sQuery(id+"F6.wireOp",EDGE,"E94.trimOffspring"),sQuery(id+"F6.wireOp",EDGE,"E96.trimOffspring"),sQuery(id+"F6.wireOp",EDGE,"E100"),sQuery(id+"F6.wireOp",EDGE,"E101"),sQuery(id+"F6.wireOp",EDGE,"E102"),sQuery(id+"F6.wireOp",EDGE,"E103"),sQuery(id+"F6.wireOp",EDGE,"E104"),sQuery(id+"F6.wireOp",EDGE,"E105")])],"isStart":false})}),makeQuery(id+"F7.boolean.opBoolean","COPY",FACE,{"derivedFrom":makeQuery(id+"F7.opExtrude","SWEPT_FACE",FACE,{"disambiguationData":[OSD([subQ1,subQ0])]})}),makeQuery(id+"F7.boolean.opBoolean","COPY",FACE,{"derivedFrom":makeQuery(id+"F7.opExtrude","SWEPT_FACE",FACE,{"disambiguationData":[OSD([subQ2])]})}),makeQuery(id+"F15.opExtrude","SWEPT_FACE",FACE,{"disambiguationData":[OSD([sQuery(id+"F14.wireOp",EDGE,"E154")])]}),makeQuery(id+"F17.opExtrude","SWEPT_FACE",FACE,{"disambiguationData":[OSD([sQuery(id+"F16.wireOp",EDGE,"E157")])]}),makeQuery(id+"F56.opExtrude","SWEPT_FACE",FACE,{"disambiguationData":[OSD([sQuery(id+"F55.wireOp",EDGE,"E335")])]}),makeQuery(id+"F56.opExtrude","SWEPT_FACE",FACE,{"disambiguationData":[OSD([sQuery(id+"F55.wireOp",EDGE,"E336")])]})])],"derivedFrom":makeQuery(id+"F7.boolean.opBoolean","COPY",EDGE,{"derivedFrom":makeQuery(id+"F7.opExtrude","CAP_EDGE",EDGE,{"disambiguationData":[OSD([subQ2])],"isStart":false})})});}
            chamfer(context, id + "F77", {"entities" : qUnion([Q0, Q1, Q2, Q3, Q4, Q5, Q6, Q7, Q8, Q9, Q10, Q11, Q12, Q13, Q14, Q15, Q16, Q17, Q18, Q19, Q20, Q21]), "width" : 0.76 * mm, "tangentPropagation" : true});
        }
        {
            var Q0;
            Q0=makeQuery(id+"F5.boolean.opBoolean","COPY",EDGE,{"derivedFrom":makeQuery(id+"F5.opExtrude","CAP_EDGE",EDGE,{"disambiguationData":[OSD([sQuery(id+"F4.wireOp",EDGE,"E28")])],"isStart":true})});
            var Q1;
            Q1=makeQuery(id+"F5.boolean.opBoolean","COPY",EDGE,{"derivedFrom":makeQuery(id+"F5.opExtrude","CAP_EDGE",EDGE,{"disambiguationData":[OSD([sQuery(id+"F4.wireOp",EDGE,"E46")])],"isStart":true})});
            var Q2;
            Q2=makeQuery(id+"F25.boolean.opBoolean","COPY",EDGE,{"derivedFrom":makeQuery(id+"F25.opExtrude","CAP_EDGE",EDGE,{"disambiguationData":[OSD([sQuery(id+"F24.wireOp",EDGE,"E201")])],"isStart":true})});
            var Q3;
            Q3=makeQuery(id+"F7.boolean.opBoolean","COPY",EDGE,{"derivedFrom":makeQuery(id+"F7.opExtrude","CAP_EDGE",EDGE,{"disambiguationData":[OSD([sQuery(id+"F6.wireOp",EDGE,"E72")])],"isStart":true})});
            var Q4;
            Q4=makeQuery(id+"F9.boolean.opBoolean","COPY",EDGE,{"derivedFrom":makeQuery(id+"F9.opExtrude","CAP_EDGE",EDGE,{"disambiguationData":[OSD([sQuery(id+"F8.wireOp",EDGE,"E107")])],"isStart":true})});
            var Q5;
            Q5=makeQuery(id+"F3.boolean.opBoolean","COPY",EDGE,{"derivedFrom":makeQuery(id+"F3.opExtrude","CAP_EDGE",EDGE,{"disambiguationData":[OSD([sQuery(id+"F2.wireOp",EDGE,"E10")])],"isStart":true})});
            chamfer(context, id + "F78", {"entities" : qUnion([Q0, Q1, Q2, Q3, Q4, Q5]), "width" : 5.08 * mm, "tangentPropagation" : true});
        }
    });
